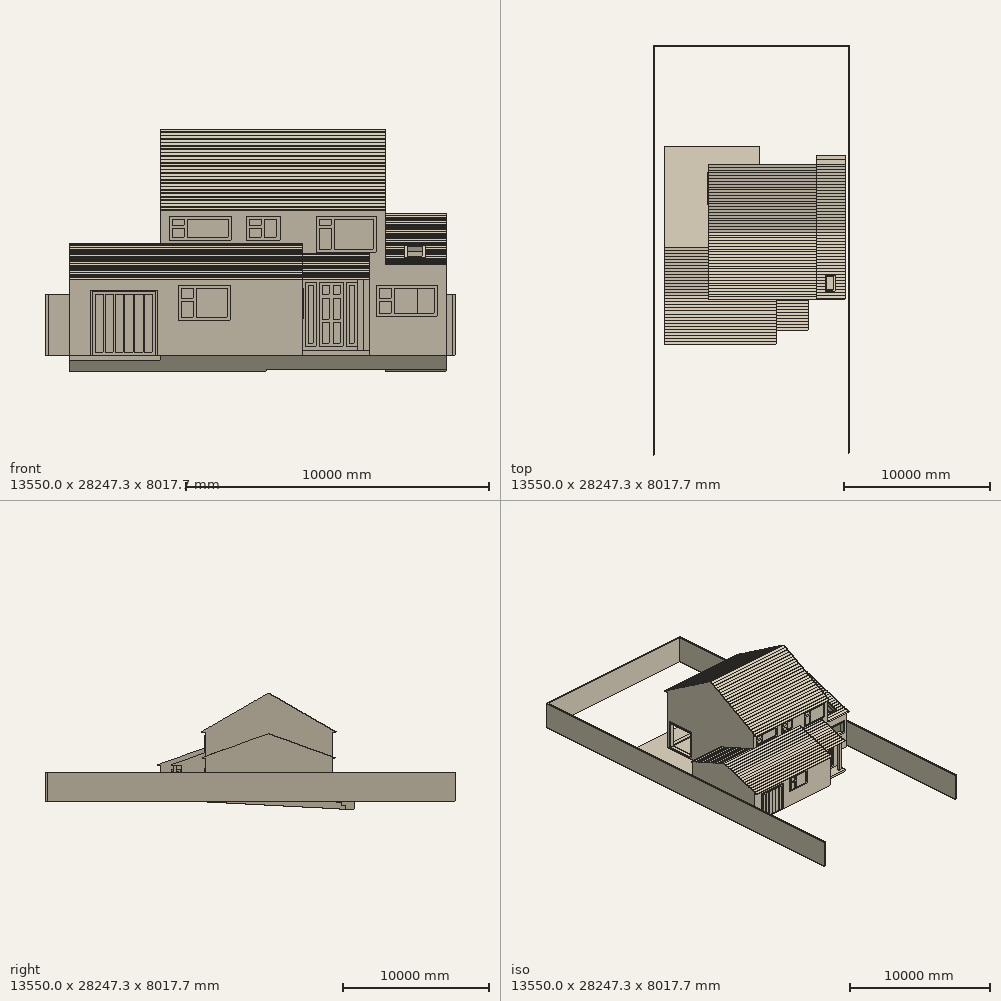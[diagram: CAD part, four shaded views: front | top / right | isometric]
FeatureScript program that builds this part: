
annotation { "Feature Type Name" : "Feature", "Feature Type Description" : "" }
export const myFeature = defineFeature(function(context is Context, id is Id, definition is map)
    precondition{}
    {
        {
            var Q0;
            Q0=qCreatedBy(makeId("Top.planeOp"),FACE);
            var sketch = newSketch(context, id + "F0", { "sketchPlane" : qUnion([Q0])});
            skLineSegment(sketch, "E0", {"start": v(-7450, 3230) * mm, "end": v(-10450, 3230) * mm});
            skLineSegment(sketch, "E1", {"start": v(-10450, 3230) * mm, "end": v(-10450, -3070) * mm});
            skLineSegment(sketch, "E2", {"start": v(-10450, -3070) * mm, "end": v(-2750, -3070) * mm});
            skLineSegment(sketch, "E3", {"start": v(-2750, -3070) * mm, "end": v(-2750, -1320) * mm});
            skLineSegment(sketch, "E4", {"start": v(-2750, 0) * mm, "end": v(0, 0) * mm});
            skLineSegment(sketch, "E5", {"start": v(0, 0) * mm, "end": v(0, 3000) * mm});
            skLineSegment(sketch, "E6", {"start": v(0, 8780) * mm, "end": v(-7450, 8780) * mm});
            skLineSegment(sketch, "E7", {"start": v(-7450, 8780) * mm, "end": v(-7450, 3230) * mm});
            skLineSegment(sketch, "E8", {"start": v(-7450, 2980) * mm, "end": v(-10200, 2980) * mm});
            skLineSegment(sketch, "E9", {"start": v(-10200, 2980) * mm, "end": v(-10200, -2820) * mm});
            skLineSegment(sketch, "E10", {"start": v(-10200, -2820) * mm, "end": v(-7450, -2820) * mm});
            skLineSegment(sketch, "E11", {"start": v(-7450, -2820) * mm, "end": v(-7450, 1280) * mm});
            skLineSegment(sketch, "E12", {"start": v(-7200, 2480) * mm, "end": v(-4870, 2480) * mm});
            skLineSegment(sketch, "E13", {"start": v(-4870, 2480) * mm, "end": v(-4870, -270) * mm});
            skLineSegment(sketch, "E14", {"start": v(-4870, -2820) * mm, "end": v(-7200, -2820) * mm});
            skLineSegment(sketch, "E15", {"start": v(-7200, -2820) * mm, "end": v(-7200, 1280) * mm});
            skLineSegment(sketch, "E16", {"start": v(-3000, -2820) * mm, "end": v(-3000, -1620) * mm});
            skLineSegment(sketch, "E17", {"start": v(-3000, -1620) * mm, "end": v(-3920, -1620) * mm});
            skLineSegment(sketch, "E18", {"start": v(-7200, 2580) * mm, "end": v(-4720, 2580) * mm});
            skLineSegment(sketch, "E19", {"start": v(-3800, 2580) * mm, "end": v(-3800, 6100) * mm});
            skLineSegment(sketch, "E20", {"start": v(-3800, 8530) * mm, "end": v(-7200, 8530) * mm});
            skLineSegment(sketch, "E21", {"start": v(-7200, 8530) * mm, "end": v(-7200, 2580) * mm});
            skLineSegment(sketch, "E22", {"start": v(-250, 8530) * mm, "end": v(-3700, 8530) * mm});
            skLineSegment(sketch, "E23", {"start": v(-3700, 6100) * mm, "end": v(-3700, 4600) * mm});
            skLineSegment(sketch, "E24", {"start": v(-3700, 4600) * mm, "end": v(-3650, 4600) * mm});
            skLineSegment(sketch, "E25", {"start": v(-250, 4600) * mm, "end": v(-250, 8530) * mm});
            skLineSegment(sketch, "E26", {"start": v(-2750, 3043.27) * mm, "end": v(-2750, 4500) * mm});
            skLineSegment(sketch, "E27", {"start": v(-2750, 4500) * mm, "end": v(-2800, 4500) * mm});
            skLineSegment(sketch, "E28", {"start": v(-3700, 4500) * mm, "end": v(-3700, 3043.27) * mm});
            skLineSegment(sketch, "E29", {"start": v(-250, 250) * mm, "end": v(-2650, 250) * mm});
            skLineSegment(sketch, "E30", {"start": v(-2650, 250) * mm, "end": v(-2650, 900) * mm});
            skLineSegment(sketch, "E31", {"start": v(-2650, 4500) * mm, "end": v(-1650, 4500) * mm});
            skLineSegment(sketch, "E32", {"start": v(-250, 4500) * mm, "end": v(-250, 3800) * mm});
            skLineSegment(sketch, "E33", {"start": v(-4770, 2480) * mm, "end": v(-4720, 2480) * mm});
            skLineSegment(sketch, "E34", {"start": v(-2750, 2480) * mm, "end": v(-2750, 1650) * mm});
            skLineSegment(sketch, "E35", {"start": v(-2750, 250) * mm, "end": v(-3000, 250) * mm});
            skLineSegment(sketch, "E36", {"start": v(-3000, -1520) * mm, "end": v(-3920, -1520) * mm});
            skLineSegment(sketch, "E37", {"start": v(-4770, -1520) * mm, "end": v(-4770, -1020) * mm});
            skLineSegment(sketch, "E38", {"start": v(-3000, -620) * mm, "end": v(-2750, -620) * mm, "construction": true});
            skLineSegment(sketch, "E39", {"start": v(-3000, -1320) * mm, "end": v(-2750, -1320) * mm, "construction": true});
            skLineSegment(sketch, "E40.trimOffspring", {"start": v(-2750, -620) * mm, "end": v(-2750, 0) * mm});
            skLineSegment(sketch, "E41.trimOffspring", {"start": v(-3000, -1320) * mm, "end": v(-3000, -1520) * mm});
            skLineSegment(sketch, "E42", {"start": v(-4720, 2580) * mm, "end": v(-4720, 2480) * mm});
            skLineSegment(sketch, "E43", {"start": v(-3970, 2580) * mm, "end": v(-3970, 2480) * mm});
            skLineSegment(sketch, "E44.trimOffspring", {"start": v(-3970, 2580) * mm, "end": v(-3800, 2580) * mm});
            skLineSegment(sketch, "E45.trimOffspring", {"start": v(-3970, 2480) * mm, "end": v(-3700, 2480) * mm});
            skLineSegment(sketch, "E46", {"start": v(-4770, -1620) * mm, "end": v(-4770, -2820) * mm});
            skLineSegment(sketch, "E47", {"start": v(-3000, -2820) * mm, "end": v(-4770, -2820) * mm});
            skLineSegment(sketch, "E48", {"start": v(-4670, -1520) * mm, "end": v(-4670, -1620) * mm});
            skLineSegment(sketch, "E49", {"start": v(-3920, -1620) * mm, "end": v(-3920, -1520) * mm});
            skLineSegment(sketch, "E50.trimOffspring", {"start": v(-4670, -1620) * mm, "end": v(-4770, -1620) * mm});
            skLineSegment(sketch, "E51.trimOffspring", {"start": v(-4670, -1520) * mm, "end": v(-4770, -1520) * mm});
            skLineSegment(sketch, "E52", {"start": v(-4870, -1020) * mm, "end": v(-4770, -1020) * mm});
            skLineSegment(sketch, "E53", {"start": v(-4870, -270) * mm, "end": v(-4770, -270) * mm});
            skLineSegment(sketch, "E54.trimOffspring", {"start": v(-4870, -1020) * mm, "end": v(-4870, -2820) * mm});
            skLineSegment(sketch, "E55.trimOffspring", {"start": v(-4770, -270) * mm, "end": v(-4770, 2480) * mm});
            skLineSegment(sketch, "E56", {"start": v(-3800, 8530) * mm, "end": v(-3700, 8530) * mm});
            skLineSegment(sketch, "E57", {"start": v(-3800, 6100) * mm, "end": v(-3700, 6100) * mm});
            skLineSegment(sketch, "E58", {"start": v(-3650, 4600) * mm, "end": v(-3650, 4500) * mm});
            skLineSegment(sketch, "E59", {"start": v(-2800, 4600) * mm, "end": v(-2800, 4500) * mm});
            skLineSegment(sketch, "E60.trimOffspring", {"start": v(-2800, 4600) * mm, "end": v(-1650, 4600) * mm});
            skLineSegment(sketch, "E61.trimOffspring", {"start": v(-3650, 4500) * mm, "end": v(-3700, 4500) * mm});
            skLineSegment(sketch, "E62", {"start": v(-1650, 4600) * mm, "end": v(-1650, 4500) * mm});
            skLineSegment(sketch, "E63", {"start": v(-950, 4600) * mm, "end": v(-950, 4500) * mm});
            skLineSegment(sketch, "E64.trimOffspring", {"start": v(-950, 4600) * mm, "end": v(-250, 4600) * mm});
            skLineSegment(sketch, "E65.trimOffspring", {"start": v(-950, 4500) * mm, "end": v(-250, 4500) * mm});
            skLineSegment(sketch, "E66", {"start": v(-3000, 250) * mm, "end": v(-3000, -620) * mm});
            skLineSegment(sketch, "E67", {"start": v(-2750, 900) * mm, "end": v(-2650, 900) * mm});
            skLineSegment(sketch, "E68", {"start": v(-2750, 1650) * mm, "end": v(-2650, 1650) * mm});
            skLineSegment(sketch, "E69.trimOffspring", {"start": v(-2750, 900) * mm, "end": v(-2750, 250) * mm});
            skLineSegment(sketch, "E70.trimOffspring", {"start": v(-2650, 1650) * mm, "end": v(-2650, 4500) * mm});
            skLineSegment(sketch, "E71", {"start": v(-7450, 2080) * mm, "end": v(-7200, 2080) * mm});
            skLineSegment(sketch, "E72", {"start": v(-7450, 1280) * mm, "end": v(-7200, 1280) * mm});
            skLineSegment(sketch, "E73.trimOffspring", {"start": v(-7200, 2080) * mm, "end": v(-7200, 2480) * mm});
            skLineSegment(sketch, "E74.trimOffspring", {"start": v(-7450, 2080) * mm, "end": v(-7450, 2980) * mm});
            skLineSegment(sketch, "E75", {"start": v(-250, 3800) * mm, "end": v(0, 3800) * mm});
            skLineSegment(sketch, "E76", {"start": v(-250, 3000) * mm, "end": v(0, 3000) * mm});
            skLineSegment(sketch, "E77.trimOffspring", {"start": v(0, 3800) * mm, "end": v(0, 8780) * mm});
            skLineSegment(sketch, "E78.trimOffspring", {"start": v(-250, 3000) * mm, "end": v(-250, 250) * mm});
            skLineSegment(sketch, "E79", {"start": v(-3000, -620) * mm, "end": v(-3000, -1320) * mm});
            skLineSegment(sketch, "E80", {"start": v(-2750, -620) * mm, "end": v(-2750, -1320) * mm});
            skLineSegment(sketch, "E81", {"start": v(-3700, 3043.27) * mm, "end": v(-3700, 2480) * mm});
            skLineSegment(sketch, "E82", {"start": v(-2750, 2480) * mm, "end": v(-2750, 3043.27) * mm});
            skSolve(sketch);
        }
        {
            var Q0;
            Q0=qSketchRegion(id+"F0",true);
            extrude(context, id + "F1", {"entities" : qUnion([Q0]), "offsetDistance" : 25 * mm, "depth" : 2500 * mm});
        }
        {
            var Q0;
            Q0=makeQuery(id+"F1.opExtrude","CAP_FACE",FACE,{"disambiguationData":[OSD([sQuery(id+"F0.wireOp",EDGE,"E0"),sQuery(id+"F0.wireOp",EDGE,"E1"),sQuery(id+"F0.wireOp",EDGE,"E2"),sQuery(id+"F0.wireOp",EDGE,"E3"),sQuery(id+"F0.wireOp",EDGE,"E6"),sQuery(id+"F0.wireOp",EDGE,"E7"),sQuery(id+"F0.wireOp",EDGE,"E8"),sQuery(id+"F0.wireOp",EDGE,"E9"),sQuery(id+"F0.wireOp",EDGE,"E10"),sQuery(id+"F0.wireOp",EDGE,"E11"),sQuery(id+"F0.wireOp",EDGE,"E12"),sQuery(id+"F0.wireOp",EDGE,"E13"),sQuery(id+"F0.wireOp",EDGE,"E14"),sQuery(id+"F0.wireOp",EDGE,"E15"),sQuery(id+"F0.wireOp",EDGE,"E16"),sQuery(id+"F0.wireOp",EDGE,"E17"),sQuery(id+"F0.wireOp",EDGE,"E18"),sQuery(id+"F0.wireOp",EDGE,"E20"),sQuery(id+"F0.wireOp",EDGE,"E21"),sQuery(id+"F0.wireOp",EDGE,"E22"),sQuery(id+"F0.wireOp",EDGE,"E25"),sQuery(id+"F0.wireOp",EDGE,"E32"),sQuery(id+"F0.wireOp",EDGE,"E33"),sQuery(id+"F0.wireOp",EDGE,"E36"),sQuery(id+"F0.wireOp",EDGE,"E37"),sQuery(id+"F0.wireOp",EDGE,"E39"),sQuery(id+"F0.wireOp",EDGE,"E41.trimOffspring"),sQuery(id+"F0.wireOp",EDGE,"E42"),sQuery(id+"F0.wireOp",EDGE,"E46"),sQuery(id+"F0.wireOp",EDGE,"E47"),sQuery(id+"F0.wireOp",EDGE,"E48"),sQuery(id+"F0.wireOp",EDGE,"E49"),sQuery(id+"F0.wireOp",EDGE,"E50.trimOffspring"),sQuery(id+"F0.wireOp",EDGE,"E51.trimOffspring"),sQuery(id+"F0.wireOp",EDGE,"E52"),sQuery(id+"F0.wireOp",EDGE,"E53"),sQuery(id+"F0.wireOp",EDGE,"E54.trimOffspring"),sQuery(id+"F0.wireOp",EDGE,"E55.trimOffspring"),sQuery(id+"F0.wireOp",EDGE,"E56"),sQuery(id+"F0.wireOp",EDGE,"E63"),sQuery(id+"F0.wireOp",EDGE,"E64.trimOffspring"),sQuery(id+"F0.wireOp",EDGE,"E65.trimOffspring"),sQuery(id+"F0.wireOp",EDGE,"E71"),sQuery(id+"F0.wireOp",EDGE,"E72"),sQuery(id+"F0.wireOp",EDGE,"E73.trimOffspring"),sQuery(id+"F0.wireOp",EDGE,"E74.trimOffspring"),sQuery(id+"F0.wireOp",EDGE,"E75"),sQuery(id+"F0.wireOp",EDGE,"E77.trimOffspring")])],"isStart":false});
            var sketch = newSketch(context, id + "F2", { "sketchPlane" : qUnion([Q0])});
            skLineSegment(sketch, "E83.bottom", {"start": v(-7450, 8780) * mm, "end": v(0, 8780) * mm});
            skLineSegment(sketch, "E83.top", {"start": v(-7450, 0) * mm, "end": v(0, 0) * mm});
            skLineSegment(sketch, "E83.left", {"start": v(-7450, 8780) * mm, "end": v(-7450, 0) * mm});
            skLineSegment(sketch, "E83.right", {"start": v(0, 8780) * mm, "end": v(0, 0) * mm});
            skLineSegment(sketch, "E84.bottom", {"start": v(-7200, 8530) * mm, "end": v(-250, 8530) * mm});
            skLineSegment(sketch, "E84.top", {"start": v(-7200, 250) * mm, "end": v(-250, 250) * mm});
            skLineSegment(sketch, "E84.left", {"start": v(-7200, 8530) * mm, "end": v(-7200, 250) * mm});
            skLineSegment(sketch, "E84.right", {"start": v(-250, 8530) * mm, "end": v(-250, 250) * mm});
            skSolve(sketch);
        }
        {
            var Q0;
            Q0 = qSketchRegion(id + "F2", true);
            extrude(context, id + "F3", {"entities" : qUnion([Q0]), "operationType" : NewBodyOperationType.ADD, "depth" : 2300 * mm, "offsetDistance" : 25 * mm});
        }
        {
            var Q0;
            Q0=makeQuery(id+"F1.opExtrude","SWEPT_FACE",FACE,{"disambiguationData":[OSD([sQuery(id+"F0.wireOp",EDGE,"E1")])]});
            var sketch = newSketch(context, id + "F4", { "sketchPlane" : qUnion([Q0])});
            skLineSegment(sketch, "E85", {"start": v(3320, 2500) * mm, "end": v(0, 3708.38) * mm, "construction": true});
            skLineSegment(sketch, "E86", {"start": v(0, 3708.38) * mm, "end": v(-3320, 2500) * mm, "construction": true});
            skLineSegment(sketch, "E87", {"start": v(-3320, 2500) * mm, "end": v(3320, 2500) * mm});
            skLineSegment(sketch, "E88", {"start": v(0, 3708.38) * mm, "end": v(207.5, 3660.48) * mm});
            skLineSegment(sketch, "E89", {"start": v(207.5, 3660.48) * mm, "end": v(207.5, 3632.86) * mm});
            skLineSegment(sketch, "E90", {"start": v(207.5, 3632.86) * mm, "end": v(415, 3584.95) * mm});
            skLineSegment(sketch, "E91", {"start": v(415, 3584.95) * mm, "end": v(415, 3557.33) * mm});
            skLineSegment(sketch, "E92", {"start": v(415, 3557.33) * mm, "end": v(622.5, 3509.43) * mm});
            skLineSegment(sketch, "E93", {"start": v(622.5, 3509.43) * mm, "end": v(622.5, 3481.8) * mm});
            skLineSegment(sketch, "E94", {"start": v(622.5, 3481.8) * mm, "end": v(830, 3433.9) * mm});
            skLineSegment(sketch, "E95", {"start": v(830, 3433.9) * mm, "end": v(830, 3406.29) * mm});
            skLineSegment(sketch, "E96", {"start": v(830, 3406.29) * mm, "end": v(1037.5, 3358.38) * mm});
            skLineSegment(sketch, "E97", {"start": v(1037.5, 3358.38) * mm, "end": v(1037.5, 3330.76) * mm});
            skLineSegment(sketch, "E98", {"start": v(1037.5, 3330.76) * mm, "end": v(1245, 3282.86) * mm});
            skLineSegment(sketch, "E99", {"start": v(1245, 3282.86) * mm, "end": v(1245, 3255.24) * mm});
            skLineSegment(sketch, "E100", {"start": v(1245, 3255.24) * mm, "end": v(1452.5, 3207.33) * mm});
            skLineSegment(sketch, "E101", {"start": v(1452.5, 3207.33) * mm, "end": v(1452.5, 3179.71) * mm});
            skLineSegment(sketch, "E102", {"start": v(1452.5, 3179.71) * mm, "end": v(1660, 3131.8) * mm});
            skLineSegment(sketch, "E103", {"start": v(1660, 3131.8) * mm, "end": v(1660, 3104.2) * mm});
            skLineSegment(sketch, "E104", {"start": v(1660, 3104.2) * mm, "end": v(1867.5, 3056.29) * mm});
            skLineSegment(sketch, "E105", {"start": v(1867.5, 3056.29) * mm, "end": v(1867.5, 3028.67) * mm});
            skLineSegment(sketch, "E106", {"start": v(1867.5, 3028.67) * mm, "end": v(2075, 2980.76) * mm});
            skLineSegment(sketch, "E107", {"start": v(2075, 2980.76) * mm, "end": v(2075, 2953.14) * mm});
            skLineSegment(sketch, "E108", {"start": v(2075, 2953.14) * mm, "end": v(2282.5, 2905.24) * mm});
            skLineSegment(sketch, "E109", {"start": v(2282.5, 2905.24) * mm, "end": v(2282.5, 2877.62) * mm});
            skLineSegment(sketch, "E110", {"start": v(2282.5, 2877.62) * mm, "end": v(2490, 2829.71) * mm});
            skLineSegment(sketch, "E111", {"start": v(2490, 2829.71) * mm, "end": v(2490, 2802.1) * mm});
            skLineSegment(sketch, "E112", {"start": v(2490, 2802.1) * mm, "end": v(2697.5, 2754.2) * mm});
            skLineSegment(sketch, "E113", {"start": v(2697.5, 2754.2) * mm, "end": v(2697.5, 2726.57) * mm});
            skLineSegment(sketch, "E114", {"start": v(2697.5, 2726.57) * mm, "end": v(2905, 2678.67) * mm});
            skLineSegment(sketch, "E115", {"start": v(2905, 2678.67) * mm, "end": v(2905, 2651.05) * mm});
            skLineSegment(sketch, "E116", {"start": v(2905, 2651.05) * mm, "end": v(3112.5, 2603.14) * mm});
            skLineSegment(sketch, "E117", {"start": v(3112.5, 2603.14) * mm, "end": v(3112.5, 2575.52) * mm});
            skLineSegment(sketch, "E118", {"start": v(3112.5, 2575.52) * mm, "end": v(3320, 2527.62) * mm});
            skLineSegment(sketch, "E119", {"start": v(3320, 2527.62) * mm, "end": v(3320, 2500) * mm});
            skLineSegment(sketch, "E120", {"start": v(0, 3708.38) * mm, "end": v(0, 3821.25) * mm, "construction": true});
            skLineSegment(sketch, "E121.MirrorCS", {"start": v(-207.5, 3660.48) * mm, "end": v(-207.5, 3632.86) * mm});
            skLineSegment(sketch, "E122.MirrorCS", {"start": v(-2905, 2678.67) * mm, "end": v(-2905, 2651.05) * mm});
            skLineSegment(sketch, "E123.MirrorCS", {"start": v(-3320, 2527.62) * mm, "end": v(-3320, 2500) * mm});
            skLineSegment(sketch, "E124.MirrorCS", {"start": v(-3112.5, 2603.14) * mm, "end": v(-3112.5, 2575.52) * mm});
            skLineSegment(sketch, "E125.MirrorCS", {"start": v(0, 3708.38) * mm, "end": v(-207.5, 3660.48) * mm});
            skLineSegment(sketch, "E126.MirrorCS", {"start": v(-1452.5, 3207.33) * mm, "end": v(-1452.5, 3179.71) * mm});
            skLineSegment(sketch, "E127.MirrorCS", {"start": v(-2697.5, 2754.2) * mm, "end": v(-2697.5, 2726.57) * mm});
            skLineSegment(sketch, "E128.MirrorCS", {"start": v(-2075, 2953.14) * mm, "end": v(-2282.5, 2905.24) * mm});
            skLineSegment(sketch, "E129.MirrorCS", {"start": v(-3112.5, 2575.52) * mm, "end": v(-3320, 2527.62) * mm});
            skLineSegment(sketch, "E130.MirrorCS", {"start": v(-1245, 3255.24) * mm, "end": v(-1452.5, 3207.33) * mm});
            skLineSegment(sketch, "E131.MirrorCS", {"start": v(-1037.5, 3358.38) * mm, "end": v(-1037.5, 3330.76) * mm});
            skLineSegment(sketch, "E132.MirrorCS", {"start": v(-830, 3406.29) * mm, "end": v(-1037.5, 3358.38) * mm});
            skLineSegment(sketch, "E133.MirrorCS", {"start": v(-2282.5, 2905.24) * mm, "end": v(-2282.5, 2877.62) * mm});
            skLineSegment(sketch, "E134.MirrorCS", {"start": v(-1037.5, 3330.76) * mm, "end": v(-1245, 3282.86) * mm});
            skLineSegment(sketch, "E135.MirrorCS", {"start": v(-2490, 2802.1) * mm, "end": v(-2697.5, 2754.2) * mm});
            skLineSegment(sketch, "E136.MirrorCS", {"start": v(-2490, 2829.71) * mm, "end": v(-2490, 2802.1) * mm});
            skLineSegment(sketch, "E137.MirrorCS", {"start": v(-830, 3433.9) * mm, "end": v(-830, 3406.29) * mm});
            skLineSegment(sketch, "E138.MirrorCS", {"start": v(-1660, 3104.2) * mm, "end": v(-1867.5, 3056.29) * mm});
            skLineSegment(sketch, "E139.MirrorCS", {"start": v(-1660, 3131.8) * mm, "end": v(-1660, 3104.2) * mm});
            skLineSegment(sketch, "E140.MirrorCS", {"start": v(-1867.5, 3056.29) * mm, "end": v(-1867.5, 3028.67) * mm});
            skLineSegment(sketch, "E141.MirrorCS", {"start": v(-622.5, 3509.43) * mm, "end": v(-622.5, 3481.8) * mm});
            skLineSegment(sketch, "E142.MirrorCS", {"start": v(-2905, 2651.05) * mm, "end": v(-3112.5, 2603.14) * mm});
            skLineSegment(sketch, "E143.MirrorCS", {"start": v(-2282.5, 2877.62) * mm, "end": v(-2490, 2829.71) * mm});
            skLineSegment(sketch, "E144.MirrorCS", {"start": v(-415, 3557.33) * mm, "end": v(-622.5, 3509.43) * mm});
            skLineSegment(sketch, "E145.MirrorCS", {"start": v(-415, 3584.95) * mm, "end": v(-415, 3557.33) * mm});
            skLineSegment(sketch, "E146.MirrorCS", {"start": v(-622.5, 3481.8) * mm, "end": v(-830, 3433.9) * mm});
            skLineSegment(sketch, "E147.MirrorCS", {"start": v(-1867.5, 3028.67) * mm, "end": v(-2075, 2980.76) * mm});
            skLineSegment(sketch, "E148.MirrorCS", {"start": v(-207.5, 3632.86) * mm, "end": v(-415, 3584.95) * mm});
            skLineSegment(sketch, "E149.MirrorCS", {"start": v(-1245, 3282.86) * mm, "end": v(-1245, 3255.24) * mm});
            skLineSegment(sketch, "E150.MirrorCS", {"start": v(-2697.5, 2726.57) * mm, "end": v(-2905, 2678.67) * mm});
            skLineSegment(sketch, "E151.MirrorCS", {"start": v(-1452.5, 3179.71) * mm, "end": v(-1660, 3131.8) * mm});
            skLineSegment(sketch, "E152.MirrorCS", {"start": v(-2075, 2980.76) * mm, "end": v(-2075, 2953.14) * mm});
            skSolve(sketch);
        }
        {
            var Q0;
            Q0 = qSketchRegion(id + "F4", true);
            var Q1;
            Q1=makeQuery(id+"F3.boolean.opBoolean","MERGE",FACE,{"derivedFrom":[makeQuery(id+"F1.opExtrude","SWEPT_FACE",FACE,{"disambiguationData":[OSD([sQuery(id+"F0.wireOp",EDGE,"E7")])]}),makeQuery(id+"F1.opExtrude","SWEPT_FACE",FACE,{"disambiguationData":[OSD([sQuery(id+"F0.wireOp",EDGE,"E11")])]}),makeQuery(id+"F1.opExtrude","SWEPT_FACE",FACE,{"disambiguationData":[OSD([sQuery(id+"F0.wireOp",EDGE,"E74.trimOffspring")])]}),makeQuery(id+"F3.opExtrude","SWEPT_FACE",FACE,{"disambiguationData":[OSD([sQuery(id+"F2.wireOp",EDGE,"E83.left")])]})]});
            extrude(context, id + "F5", {"entities" : qUnion([Q0]), "operationType" : NewBodyOperationType.ADD, "oppositeDirection" : true, "depth" : 3250 * mm, "endBoundEntityFace" : qUnion([Q1]), "offsetDistance" : 25 * mm});
        }
        {
            var Q0;
            Q0=makeQuery(id+"F5.boolean.opBoolean","MERGE",FACE,{"derivedFrom":[makeQuery(id+"F3.boolean.opBoolean","MERGE",FACE,{"derivedFrom":[makeQuery(id+"F1.opExtrude","SWEPT_FACE",FACE,{"disambiguationData":[OSD([sQuery(id+"F0.wireOp",EDGE,"E15")])]}),makeQuery(id+"F1.opExtrude","SWEPT_FACE",FACE,{"disambiguationData":[OSD([sQuery(id+"F0.wireOp",EDGE,"E21")])]}),makeQuery(id+"F1.opExtrude","SWEPT_FACE",FACE,{"disambiguationData":[OSD([sQuery(id+"F0.wireOp",EDGE,"E73.trimOffspring")])]}),makeQuery(id+"F3.opExtrude","SWEPT_FACE",FACE,{"disambiguationData":[OSD([sQuery(id+"F2.wireOp",EDGE,"E84.left")])]})]}),makeQuery(id+"F5.opExtrude","CAP_FACE",FACE,{"disambiguationData":[OSD([sQuery(id+"F4.wireOp",EDGE,"E85"),sQuery(id+"F4.wireOp",EDGE,"E86"),sQuery(id+"F4.wireOp",EDGE,"E87")])],"isStart":false})]});
            var sketch = newSketch(context, id + "F6", { "sketchPlane" : qUnion([Q0])});
            skLineSegment(sketch, "E153", {"start": v(0, 2500) * mm, "end": v(0, 3708.38) * mm});
            skLineSegment(sketch, "E154", {"start": v(0, 3708.38) * mm, "end": v(-3320, 2500) * mm, "construction": true});
            skLineSegment(sketch, "E155", {"start": v(-3320, 2500) * mm, "end": v(-3070, 2500) * mm});
            skLineSegment(sketch, "E156", {"start": v(-3070, 2500) * mm, "end": v(-3070, 2300) * mm});
            skLineSegment(sketch, "E157", {"start": v(-3070, 2300) * mm, "end": v(0, 2300) * mm});
            skLineSegment(sketch, "E158", {"start": v(0, 2300) * mm, "end": v(0, 2500) * mm});
            skLineSegment(sketch, "E159.0", {"start": v(0, 3708.38) * mm, "end": v(-207.5, 3660.48) * mm});
            skLineSegment(sketch, "E160.0", {"start": v(-207.5, 3660.48) * mm, "end": v(-207.5, 3632.86) * mm});
            skLineSegment(sketch, "E160.1", {"start": v(-207.5, 3632.86) * mm, "end": v(-415, 3584.95) * mm});
            skLineSegment(sketch, "E160.2", {"start": v(-415, 3584.95) * mm, "end": v(-415, 3557.33) * mm});
            skLineSegment(sketch, "E160.3", {"start": v(-415, 3557.33) * mm, "end": v(-622.5, 3509.43) * mm});
            skLineSegment(sketch, "E160.4", {"start": v(-622.5, 3509.43) * mm, "end": v(-622.5, 3481.8) * mm});
            skLineSegment(sketch, "E161.0", {"start": v(-622.5, 3481.8) * mm, "end": v(-830, 3433.9) * mm});
            skLineSegment(sketch, "E161.1", {"start": v(-830, 3433.9) * mm, "end": v(-830, 3406.29) * mm});
            skLineSegment(sketch, "E161.2", {"start": v(-830, 3406.29) * mm, "end": v(-1037.5, 3358.38) * mm});
            skLineSegment(sketch, "E161.3", {"start": v(-1037.5, 3358.38) * mm, "end": v(-1037.5, 3330.76) * mm});
            skLineSegment(sketch, "E162.0", {"start": v(-1037.5, 3330.76) * mm, "end": v(-1245, 3282.86) * mm});
            skLineSegment(sketch, "E162.1", {"start": v(-1245, 3282.86) * mm, "end": v(-1245, 3255.24) * mm});
            skLineSegment(sketch, "E162.2", {"start": v(-1245, 3255.24) * mm, "end": v(-1452.5, 3207.33) * mm});
            skLineSegment(sketch, "E162.3", {"start": v(-1452.5, 3207.33) * mm, "end": v(-1452.5, 3179.71) * mm});
            skLineSegment(sketch, "E163.0", {"start": v(-1452.5, 3179.71) * mm, "end": v(-1660, 3131.8) * mm});
            skLineSegment(sketch, "E163.1", {"start": v(-1660, 3131.8) * mm, "end": v(-1660, 3104.2) * mm});
            skLineSegment(sketch, "E163.2", {"start": v(-1660, 3104.2) * mm, "end": v(-1867.5, 3056.29) * mm});
            skLineSegment(sketch, "E163.3", {"start": v(-1867.5, 3056.29) * mm, "end": v(-1867.5, 3028.67) * mm});
            skLineSegment(sketch, "E164.0", {"start": v(-1867.5, 3028.67) * mm, "end": v(-2075, 2980.76) * mm});
            skLineSegment(sketch, "E164.1", {"start": v(-2075, 2980.76) * mm, "end": v(-2075, 2953.14) * mm});
            skLineSegment(sketch, "E164.2", {"start": v(-2075, 2953.14) * mm, "end": v(-2282.5, 2905.24) * mm});
            skLineSegment(sketch, "E164.3", {"start": v(-2282.5, 2905.24) * mm, "end": v(-2282.5, 2877.62) * mm});
            skLineSegment(sketch, "E164.4", {"start": v(-2282.5, 2877.62) * mm, "end": v(-2490, 2829.71) * mm});
            skLineSegment(sketch, "E164.5", {"start": v(-2490, 2829.71) * mm, "end": v(-2490, 2802.1) * mm});
            skLineSegment(sketch, "E164.6", {"start": v(-2490, 2802.1) * mm, "end": v(-2697.5, 2754.2) * mm});
            skLineSegment(sketch, "E165.0", {"start": v(-2697.5, 2754.2) * mm, "end": v(-2697.5, 2726.57) * mm});
            skLineSegment(sketch, "E165.1", {"start": v(-2697.5, 2726.57) * mm, "end": v(-2905, 2678.67) * mm});
            skLineSegment(sketch, "E165.2", {"start": v(-2905, 2678.67) * mm, "end": v(-2905, 2651.05) * mm});
            skLineSegment(sketch, "E165.3", {"start": v(-2905, 2651.05) * mm, "end": v(-3112.5, 2603.14) * mm});
            skLineSegment(sketch, "E165.4", {"start": v(-3112.5, 2603.14) * mm, "end": v(-3112.5, 2575.52) * mm});
            skLineSegment(sketch, "E165.5", {"start": v(-3112.5, 2575.52) * mm, "end": v(-3320, 2527.62) * mm});
            skLineSegment(sketch, "E165.6", {"start": v(-3320, 2527.62) * mm, "end": v(-3320, 2500) * mm});
            skSolve(sketch);
        }
        {
            var Q0;
            Q0 = qSketchRegion(id + "F6", true);
            var Q1;
            Q1=makeQuery(id+"F1.opExtrude","SWEPT_FACE",FACE,{"disambiguationData":[OSD([sQuery(id+"F0.wireOp",EDGE,"E40.trimOffspring")])]});
            extrude(context, id + "F7", {"entities" : qUnion([Q0]), "operationType" : NewBodyOperationType.ADD, "endBound" : BoundingType.UP_TO_SURFACE, "depth" : 25 * mm, "endBoundEntityFace" : qUnion([Q1]), "offsetDistance" : 25 * mm, "hasSecondDirection" : true, "secondDirectionOppositeDirection" : true, "secondDirectionDepth" : 250 * mm});
        }
        {
            var Q0;
            Q0=makeQuery(id+"F3.boolean.opBoolean","MERGE",FACE,{"derivedFrom":[makeQuery(id+"F1.opExtrude","SWEPT_FACE",FACE,{"disambiguationData":[OSD([sQuery(id+"F0.wireOp",EDGE,"E5")])]}),makeQuery(id+"F1.opExtrude","SWEPT_FACE",FACE,{"disambiguationData":[OSD([sQuery(id+"F0.wireOp",EDGE,"E77.trimOffspring")])]}),makeQuery(id+"F3.opExtrude","SWEPT_FACE",FACE,{"disambiguationData":[OSD([sQuery(id+"F2.wireOp",EDGE,"E83.right")])]})]});
            var sketch = newSketch(context, id + "F8", { "sketchPlane" : qUnion([Q0])});
            skLineSegment(sketch, "E166", {"start": v(4390, 7478.9) * mm, "end": v(-250, 4800) * mm, "construction": true});
            skLineSegment(sketch, "E167", {"start": v(-250, 4800) * mm, "end": v(9030, 4800) * mm});
            skLineSegment(sketch, "E168", {"start": v(9030, 4800) * mm, "end": v(4390, 7478.9) * mm, "construction": true});
            skLineSegment(sketch, "E169", {"start": v(4390, 7478.9) * mm, "end": v(4390, 6580.18) * mm, "construction": true});
            skLineSegment(sketch, "E170", {"start": v(4390, 7478.9) * mm, "end": v(4195.45, 7392.29) * mm});
            skLineSegment(sketch, "E171", {"start": v(4195.45, 7392.29) * mm, "end": v(4195.45, 7366.58) * mm});
            skLineSegment(sketch, "E172", {"start": v(4195.45, 7366.58) * mm, "end": v(4000.9, 7279.97) * mm});
            skLineSegment(sketch, "E173", {"start": v(4000.9, 7279.97) * mm, "end": v(4000.9, 7254.26) * mm});
            skLineSegment(sketch, "E174", {"start": v(4000.9, 7254.26) * mm, "end": v(3806.36, 7167.64) * mm});
            skLineSegment(sketch, "E175", {"start": v(3806.36, 7167.64) * mm, "end": v(3806.36, 7141.94) * mm});
            skLineSegment(sketch, "E176", {"start": v(3806.36, 7141.94) * mm, "end": v(3611.81, 7055.32) * mm});
            skLineSegment(sketch, "E177", {"start": v(3611.81, 7055.32) * mm, "end": v(3611.81, 7029.62) * mm});
            skLineSegment(sketch, "E178", {"start": v(3611.81, 7029.62) * mm, "end": v(3417.27, 6943) * mm});
            skLineSegment(sketch, "E179", {"start": v(3417.27, 6943) * mm, "end": v(3417.27, 6917.3) * mm});
            skLineSegment(sketch, "E180", {"start": v(3417.27, 6917.3) * mm, "end": v(3222.72, 6830.68) * mm});
            skLineSegment(sketch, "E181", {"start": v(3222.72, 6830.68) * mm, "end": v(3222.72, 6804.97) * mm});
            skLineSegment(sketch, "E182", {"start": v(3222.72, 6804.97) * mm, "end": v(3028.17, 6718.36) * mm});
            skLineSegment(sketch, "E183", {"start": v(3028.17, 6718.36) * mm, "end": v(3028.17, 6692.65) * mm});
            skLineSegment(sketch, "E184", {"start": v(3028.17, 6692.65) * mm, "end": v(2833.62, 6606.04) * mm});
            skLineSegment(sketch, "E185", {"start": v(2833.62, 6606.04) * mm, "end": v(2833.62, 6580.33) * mm});
            skLineSegment(sketch, "E186", {"start": v(2833.62, 6580.33) * mm, "end": v(2639.08, 6493.71) * mm});
            skLineSegment(sketch, "E187", {"start": v(2639.08, 6493.71) * mm, "end": v(2639.08, 6468) * mm});
            skLineSegment(sketch, "E188", {"start": v(2639.08, 6468) * mm, "end": v(2444.53, 6381.4) * mm});
            skLineSegment(sketch, "E189", {"start": v(2444.53, 6381.4) * mm, "end": v(2444.53, 6355.69) * mm});
            skLineSegment(sketch, "E190", {"start": v(2444.53, 6355.69) * mm, "end": v(2249.98, 6269.07) * mm});
            skLineSegment(sketch, "E191", {"start": v(2249.98, 6269.07) * mm, "end": v(2249.98, 6243.37) * mm});
            skLineSegment(sketch, "E192", {"start": v(2249.98, 6243.37) * mm, "end": v(2055.44, 6156.75) * mm});
            skLineSegment(sketch, "E193", {"start": v(2055.44, 6156.75) * mm, "end": v(2055.44, 6131.04) * mm});
            skLineSegment(sketch, "E194", {"start": v(2055.44, 6131.04) * mm, "end": v(1860.9, 6044.43) * mm});
            skLineSegment(sketch, "E195", {"start": v(1860.9, 6044.43) * mm, "end": v(1860.9, 6018.72) * mm});
            skLineSegment(sketch, "E196", {"start": v(1860.9, 6018.72) * mm, "end": v(1666.34, 5932.1) * mm});
            skLineSegment(sketch, "E197", {"start": v(1666.34, 5932.1) * mm, "end": v(1666.34, 5906.4) * mm});
            skLineSegment(sketch, "E198", {"start": v(1666.34, 5906.4) * mm, "end": v(1471.8, 5819.78) * mm});
            skLineSegment(sketch, "E199", {"start": v(1471.8, 5819.78) * mm, "end": v(1471.8, 5794.08) * mm});
            skLineSegment(sketch, "E200", {"start": v(1471.8, 5794.08) * mm, "end": v(1277.25, 5707.46) * mm});
            skLineSegment(sketch, "E201", {"start": v(1277.25, 5707.46) * mm, "end": v(1277.25, 5681.76) * mm});
            skLineSegment(sketch, "E202", {"start": v(1277.25, 5681.76) * mm, "end": v(1082.7, 5595.14) * mm});
            skLineSegment(sketch, "E203", {"start": v(1082.7, 5595.14) * mm, "end": v(1082.7, 5569.44) * mm});
            skLineSegment(sketch, "E204", {"start": v(1082.7, 5569.44) * mm, "end": v(888.16, 5482.82) * mm});
            skLineSegment(sketch, "E205", {"start": v(888.16, 5482.82) * mm, "end": v(888.16, 5457.11) * mm});
            skLineSegment(sketch, "E206", {"start": v(888.16, 5457.11) * mm, "end": v(693.6, 5370.5) * mm});
            skLineSegment(sketch, "E207", {"start": v(693.6, 5370.5) * mm, "end": v(693.6, 5344.8) * mm});
            skLineSegment(sketch, "E208", {"start": v(693.6, 5344.8) * mm, "end": v(499.06, 5258.17) * mm});
            skLineSegment(sketch, "E209", {"start": v(499.06, 5258.17) * mm, "end": v(499.06, 5232.47) * mm});
            skLineSegment(sketch, "E210", {"start": v(499.06, 5232.47) * mm, "end": v(304.51, 5145.85) * mm});
            skLineSegment(sketch, "E211", {"start": v(304.51, 5145.85) * mm, "end": v(304.51, 5120.15) * mm});
            skLineSegment(sketch, "E212", {"start": v(304.51, 5120.15) * mm, "end": v(109.97, 5033.53) * mm});
            skLineSegment(sketch, "E213", {"start": v(109.97, 5033.53) * mm, "end": v(109.97, 5007.83) * mm});
            skLineSegment(sketch, "E214", {"start": v(109.97, 5007.83) * mm, "end": v(-70.02, 4927.7) * mm});
            skLineSegment(sketch, "E215", {"start": v(-70.02, 4927.7) * mm, "end": v(-70.02, 4903.91) * mm});
            skLineSegment(sketch, "E216", {"start": v(-70.02, 4903.91) * mm, "end": v(-250, 4823.78) * mm});
            skLineSegment(sketch, "E217", {"start": v(-250, 4823.78) * mm, "end": v(-250, 4800) * mm});
            skLineSegment(sketch, "E218.MirrorCS", {"start": v(7697.3, 5595.14) * mm, "end": v(7697.3, 5569.44) * mm});
            skLineSegment(sketch, "E219.MirrorCS", {"start": v(6724.56, 6156.75) * mm, "end": v(6724.56, 6131.04) * mm});
            skLineSegment(sketch, "E220.MirrorCS", {"start": v(5751.83, 6718.36) * mm, "end": v(5751.83, 6692.65) * mm});
            skLineSegment(sketch, "E221.MirrorCS", {"start": v(9030, 4823.78) * mm, "end": v(9030, 4800) * mm});
            skLineSegment(sketch, "E222.MirrorCS", {"start": v(5557.28, 6830.68) * mm, "end": v(5557.28, 6804.97) * mm});
            skLineSegment(sketch, "E223.MirrorCS", {"start": v(4973.64, 7167.64) * mm, "end": v(4973.64, 7141.94) * mm});
            skLineSegment(sketch, "E224.MirrorCS", {"start": v(4584.55, 7392.29) * mm, "end": v(4584.55, 7366.58) * mm});
            skLineSegment(sketch, "E225.MirrorCS", {"start": v(8850.02, 4903.91) * mm, "end": v(9030, 4823.78) * mm});
            skLineSegment(sketch, "E226.MirrorCS", {"start": v(8850.02, 4927.7) * mm, "end": v(8850.02, 4903.91) * mm});
            skLineSegment(sketch, "E227.MirrorCS", {"start": v(5946.38, 6606.04) * mm, "end": v(5946.38, 6580.33) * mm});
            skLineSegment(sketch, "E228.MirrorCS", {"start": v(6919.1, 6044.43) * mm, "end": v(6919.1, 6018.72) * mm});
            skLineSegment(sketch, "E229.MirrorCS", {"start": v(7308.2, 5794.08) * mm, "end": v(7502.75, 5707.46) * mm});
            skLineSegment(sketch, "E230.MirrorCS", {"start": v(6140.92, 6468) * mm, "end": v(6335.47, 6381.4) * mm});
            skLineSegment(sketch, "E231.MirrorCS", {"start": v(6919.1, 6018.72) * mm, "end": v(7113.66, 5932.1) * mm});
            skLineSegment(sketch, "E232.MirrorCS", {"start": v(4779.1, 7279.97) * mm, "end": v(4779.1, 7254.26) * mm});
            skLineSegment(sketch, "E233.MirrorCS", {"start": v(7502.75, 5707.46) * mm, "end": v(7502.75, 5681.76) * mm});
            skLineSegment(sketch, "E234.MirrorCS", {"start": v(7113.66, 5906.4) * mm, "end": v(7308.2, 5819.78) * mm});
            skLineSegment(sketch, "E235.MirrorCS", {"start": v(4390, 7478.9) * mm, "end": v(4584.55, 7392.29) * mm});
            skLineSegment(sketch, "E236.MirrorCS", {"start": v(8280.94, 5258.17) * mm, "end": v(8280.94, 5232.47) * mm});
            skLineSegment(sketch, "E237.MirrorCS", {"start": v(5751.83, 6692.65) * mm, "end": v(5946.38, 6606.04) * mm});
            skLineSegment(sketch, "E238.MirrorCS", {"start": v(5362.73, 6943) * mm, "end": v(5362.73, 6917.3) * mm});
            skLineSegment(sketch, "E239.MirrorCS", {"start": v(4779.1, 7254.26) * mm, "end": v(4973.64, 7167.64) * mm});
            skLineSegment(sketch, "E240.MirrorCS", {"start": v(8670.03, 5033.53) * mm, "end": v(8670.03, 5007.83) * mm});
            skLineSegment(sketch, "E241.MirrorCS", {"start": v(5557.28, 6804.97) * mm, "end": v(5751.83, 6718.36) * mm});
            skLineSegment(sketch, "E242.MirrorCS", {"start": v(4584.55, 7366.58) * mm, "end": v(4779.1, 7279.97) * mm});
            skLineSegment(sketch, "E243.MirrorCS", {"start": v(4973.64, 7141.94) * mm, "end": v(5168.19, 7055.32) * mm});
            skLineSegment(sketch, "E244.MirrorCS", {"start": v(8086.4, 5370.5) * mm, "end": v(8086.4, 5344.8) * mm});
            skLineSegment(sketch, "E245.MirrorCS", {"start": v(7502.75, 5681.76) * mm, "end": v(7697.3, 5595.14) * mm});
            skLineSegment(sketch, "E246.MirrorCS", {"start": v(7308.2, 5819.78) * mm, "end": v(7308.2, 5794.08) * mm});
            skLineSegment(sketch, "E247.MirrorCS", {"start": v(5362.73, 6917.3) * mm, "end": v(5557.28, 6830.68) * mm});
            skLineSegment(sketch, "E248.MirrorCS", {"start": v(8086.4, 5344.8) * mm, "end": v(8280.94, 5258.17) * mm});
            skLineSegment(sketch, "E249.MirrorCS", {"start": v(8670.03, 5007.83) * mm, "end": v(8850.02, 4927.7) * mm});
            skLineSegment(sketch, "E250.MirrorCS", {"start": v(6530.02, 6269.07) * mm, "end": v(6530.02, 6243.37) * mm});
            skLineSegment(sketch, "E251.MirrorCS", {"start": v(8475.49, 5145.85) * mm, "end": v(8475.49, 5120.15) * mm});
            skLineSegment(sketch, "E252.MirrorCS", {"start": v(6140.92, 6493.71) * mm, "end": v(6140.92, 6468) * mm});
            skLineSegment(sketch, "E253.MirrorCS", {"start": v(5168.19, 7055.32) * mm, "end": v(5168.19, 7029.62) * mm});
            skLineSegment(sketch, "E254.MirrorCS", {"start": v(7891.84, 5482.82) * mm, "end": v(7891.84, 5457.11) * mm});
            skLineSegment(sketch, "E255.MirrorCS", {"start": v(6530.02, 6243.37) * mm, "end": v(6724.56, 6156.75) * mm});
            skLineSegment(sketch, "E256.MirrorCS", {"start": v(7891.84, 5457.11) * mm, "end": v(8086.4, 5370.5) * mm});
            skLineSegment(sketch, "E257.MirrorCS", {"start": v(7113.66, 5932.1) * mm, "end": v(7113.66, 5906.4) * mm});
            skLineSegment(sketch, "E258.MirrorCS", {"start": v(6335.47, 6355.69) * mm, "end": v(6530.02, 6269.07) * mm});
            skLineSegment(sketch, "E259.MirrorCS", {"start": v(6335.47, 6381.4) * mm, "end": v(6335.47, 6355.69) * mm});
            skLineSegment(sketch, "E260.MirrorCS", {"start": v(8280.94, 5232.47) * mm, "end": v(8475.49, 5145.85) * mm});
            skLineSegment(sketch, "E261.MirrorCS", {"start": v(7697.3, 5569.44) * mm, "end": v(7891.84, 5482.82) * mm});
            skLineSegment(sketch, "E262.MirrorCS", {"start": v(8475.49, 5120.15) * mm, "end": v(8670.03, 5033.53) * mm});
            skLineSegment(sketch, "E263.MirrorCS", {"start": v(5168.19, 7029.62) * mm, "end": v(5362.73, 6943) * mm});
            skLineSegment(sketch, "E264.MirrorCS", {"start": v(6724.56, 6131.04) * mm, "end": v(6919.1, 6044.43) * mm});
            skLineSegment(sketch, "E265.MirrorCS", {"start": v(5946.38, 6580.33) * mm, "end": v(6140.92, 6493.71) * mm});
            skSolve(sketch);
        }
        {
            var Q0;
            Q0 = qSketchRegion(id + "F8", true);
            var Q1;
            {var subQ0=sQuery(id+"F0.wireOp",EDGE,"E74.trimOffspring");var subQ1=sQuery(id+"F0.wireOp",EDGE,"E11");var subQ2=sQuery(id+"F0.wireOp",EDGE,"E7");var subQ4=sQuery(id+"F0.wireOp",EDGE,"E0");var subQ6=sQuery(id+"F2.wireOp",EDGE,"E83.left");Q1=makeQuery(id+"F5.boolean.opBoolean","SPLIT",FACE,{"disambiguationData":[TD([makeQuery(id+"F1.opExtrude","SWEPT_FACE",FACE,{"disambiguationData":[OSD([subQ4])]})])],"derivedFrom":makeQuery(id+"F3.boolean.opBoolean","MERGE",FACE,{"derivedFrom":[makeQuery(id+"F1.opExtrude","SWEPT_FACE",FACE,{"disambiguationData":[OSD([subQ2])]}),makeQuery(id+"F1.opExtrude","SWEPT_FACE",FACE,{"disambiguationData":[OSD([subQ1])]}),makeQuery(id+"F1.opExtrude","SWEPT_FACE",FACE,{"disambiguationData":[OSD([subQ0])]}),makeQuery(id+"F3.opExtrude","SWEPT_FACE",FACE,{"disambiguationData":[OSD([subQ6])]})]})});}
            extrude(context, id + "F9", {"entities" : qUnion([Q0]), "operationType" : NewBodyOperationType.ADD, "endBound" : BoundingType.UP_TO_SURFACE, "oppositeDirection" : true, "depth" : 25 * mm, "endBoundEntityFace" : qUnion([Q1]), "offsetDistance" : 25 * mm});
        }
        {
            var Q0;
            Q0=qCreatedBy(makeId("Top.planeOp"),FACE);
            var sketch = newSketch(context, id + "F10", { "sketchPlane" : qUnion([Q0])});
            skLineSegment(sketch, "E266.bottom", {"start": v(0, 0) * mm, "end": v(2000, 0) * mm});
            skLineSegment(sketch, "E266.top", {"start": v(0, 8780) * mm, "end": v(2000, 8780) * mm});
            skLineSegment(sketch, "E266.right", {"start": v(2000, 0) * mm, "end": v(2000, 8780) * mm});
            skLineSegment(sketch, "E267.bottom", {"start": v(0, 8530) * mm, "end": v(1750, 8530) * mm});
            skLineSegment(sketch, "E267.top", {"start": v(0, 250) * mm, "end": v(1750, 250) * mm});
            skLineSegment(sketch, "E267.right", {"start": v(1750, 8530) * mm, "end": v(1750, 250) * mm});
            skLineSegment(sketch, "E268", {"start": v(0, 8530) * mm, "end": v(0, 8780) * mm});
            skLineSegment(sketch, "E269", {"start": v(0, 0) * mm, "end": v(0, 250) * mm});
            skSolve(sketch);
        }
        {
            var Q0;
            Q0 = qSketchRegion(id + "F10", true);
            extrude(context, id + "F11", {"entities" : qUnion([Q0]), "operationType" : NewBodyOperationType.ADD, "depth" : 3000 * mm, "offsetDistance" : 25 * mm});
        }
        {
            var Q0;
            Q0=makeQuery(id+"F11.opExtrude","SWEPT_FACE",FACE,{"disambiguationData":[OSD([sQuery(id+"F10.wireOp",EDGE,"E266.right")])]});
            var sketch = newSketch(context, id + "F12", { "sketchPlane" : qUnion([Q0])});
            skLineSegment(sketch, "E270", {"start": v(4390, 4688.82) * mm, "end": v(-250, 3000) * mm, "construction": true});
            skLineSegment(sketch, "E271", {"start": v(-250, 3000) * mm, "end": v(9030, 3000) * mm});
            skLineSegment(sketch, "E272", {"start": v(9030, 3000) * mm, "end": v(4390, 4688.82) * mm, "construction": true});
            skLineSegment(sketch, "E273", {"start": v(4390, 4688.82) * mm, "end": v(4390, 3754.6) * mm, "construction": true});
            skLineSegment(sketch, "E274", {"start": v(4390, 4688.82) * mm, "end": v(4183.37, 4637.3) * mm});
            skLineSegment(sketch, "E275", {"start": v(4183.37, 4637.3) * mm, "end": v(4183.37, 4613.61) * mm});
            skLineSegment(sketch, "E276", {"start": v(4183.37, 4613.61) * mm, "end": v(3976.74, 4562.1) * mm});
            skLineSegment(sketch, "E277", {"start": v(3976.74, 4562.1) * mm, "end": v(3976.74, 4538.4) * mm});
            skLineSegment(sketch, "E278", {"start": v(3976.74, 4538.4) * mm, "end": v(3770.1, 4486.89) * mm});
            skLineSegment(sketch, "E279", {"start": v(3770.1, 4486.89) * mm, "end": v(3770.1, 4463.2) * mm});
            skLineSegment(sketch, "E280", {"start": v(3770.1, 4463.2) * mm, "end": v(3563.47, 4411.68) * mm});
            skLineSegment(sketch, "E281", {"start": v(3563.47, 4411.68) * mm, "end": v(3563.47, 4387.99) * mm});
            skLineSegment(sketch, "E282", {"start": v(3563.47, 4387.99) * mm, "end": v(3356.84, 4336.47) * mm});
            skLineSegment(sketch, "E283", {"start": v(3356.84, 4336.47) * mm, "end": v(3356.84, 4312.78) * mm});
            skLineSegment(sketch, "E284", {"start": v(3356.84, 4312.78) * mm, "end": v(3150.2, 4261.26) * mm});
            skLineSegment(sketch, "E285", {"start": v(3150.2, 4261.26) * mm, "end": v(3150.2, 4237.57) * mm});
            skLineSegment(sketch, "E286", {"start": v(3150.2, 4237.57) * mm, "end": v(2943.57, 4186.05) * mm});
            skLineSegment(sketch, "E287", {"start": v(2943.57, 4186.05) * mm, "end": v(2943.57, 4162.37) * mm});
            skLineSegment(sketch, "E288", {"start": v(2943.57, 4162.37) * mm, "end": v(2736.94, 4110.85) * mm});
            skLineSegment(sketch, "E289", {"start": v(2736.94, 4110.85) * mm, "end": v(2736.94, 4087.16) * mm});
            skLineSegment(sketch, "E290", {"start": v(2736.94, 4087.16) * mm, "end": v(2530.3, 4035.64) * mm});
            skLineSegment(sketch, "E291", {"start": v(2530.3, 4035.64) * mm, "end": v(2530.3, 4011.95) * mm});
            skLineSegment(sketch, "E292", {"start": v(2530.3, 4011.95) * mm, "end": v(2323.68, 3960.43) * mm});
            skLineSegment(sketch, "E293", {"start": v(2323.68, 3960.43) * mm, "end": v(2323.68, 3936.74) * mm});
            skLineSegment(sketch, "E294", {"start": v(2323.68, 3936.74) * mm, "end": v(2117.04, 3885.22) * mm});
            skLineSegment(sketch, "E295", {"start": v(2117.04, 3885.22) * mm, "end": v(2117.04, 3861.53) * mm});
            skLineSegment(sketch, "E296", {"start": v(2117.04, 3861.53) * mm, "end": v(1910.41, 3810.01) * mm});
            skLineSegment(sketch, "E297", {"start": v(1910.41, 3810.01) * mm, "end": v(1910.41, 3786.33) * mm});
            skLineSegment(sketch, "E298", {"start": v(1910.41, 3786.33) * mm, "end": v(1703.78, 3734.8) * mm});
            skLineSegment(sketch, "E299", {"start": v(1703.78, 3734.8) * mm, "end": v(1703.78, 3711.12) * mm});
            skLineSegment(sketch, "E300", {"start": v(1703.78, 3711.12) * mm, "end": v(1497.15, 3659.6) * mm});
            skLineSegment(sketch, "E301", {"start": v(1497.15, 3659.6) * mm, "end": v(1497.15, 3635.9) * mm});
            skLineSegment(sketch, "E302", {"start": v(1497.15, 3635.9) * mm, "end": v(1290.51, 3584.4) * mm});
            skLineSegment(sketch, "E303", {"start": v(1290.51, 3584.4) * mm, "end": v(1290.51, 3560.7) * mm});
            skLineSegment(sketch, "E304", {"start": v(1290.51, 3560.7) * mm, "end": v(1083.88, 3509.18) * mm});
            skLineSegment(sketch, "E305", {"start": v(1083.88, 3509.18) * mm, "end": v(1083.88, 3485.5) * mm});
            skLineSegment(sketch, "E306", {"start": v(1083.88, 3485.5) * mm, "end": v(877.25, 3433.97) * mm});
            skLineSegment(sketch, "E307", {"start": v(877.25, 3433.97) * mm, "end": v(877.25, 3410.29) * mm});
            skLineSegment(sketch, "E308", {"start": v(877.25, 3410.29) * mm, "end": v(670.62, 3358.77) * mm});
            skLineSegment(sketch, "E309", {"start": v(670.62, 3358.77) * mm, "end": v(670.62, 3335.08) * mm});
            skLineSegment(sketch, "E310", {"start": v(670.62, 3335.08) * mm, "end": v(463.99, 3283.56) * mm});
            skLineSegment(sketch, "E311", {"start": v(463.99, 3283.56) * mm, "end": v(463.99, 3259.87) * mm});
            skLineSegment(sketch, "E312", {"start": v(463.99, 3259.87) * mm, "end": v(257.35, 3208.35) * mm});
            skLineSegment(sketch, "E313", {"start": v(257.35, 3208.35) * mm, "end": v(257.35, 3184.66) * mm});
            skLineSegment(sketch, "E314", {"start": v(257.35, 3184.66) * mm, "end": v(50.72, 3133.14) * mm});
            skLineSegment(sketch, "E315", {"start": v(50.72, 3133.14) * mm, "end": v(50.72, 3109.45) * mm});
            skLineSegment(sketch, "E316", {"start": v(50.72, 3109.45) * mm, "end": v(-155.91, 3057.93) * mm});
            skLineSegment(sketch, "E317", {"start": v(-155.91, 3057.93) * mm, "end": v(-155.91, 3034.25) * mm});
            skLineSegment(sketch, "E318", {"start": v(-155.91, 3034.25) * mm, "end": v(-250, 3010.79) * mm});
            skLineSegment(sketch, "E319", {"start": v(-250, 3010.79) * mm, "end": v(-250, 3000) * mm});
            skLineSegment(sketch, "E320.MirrorCS", {"start": v(6456.32, 3960.43) * mm, "end": v(6456.32, 3936.74) * mm});
            skLineSegment(sketch, "E321.MirrorCS", {"start": v(5423.16, 4312.78) * mm, "end": v(5629.8, 4261.26) * mm});
            skLineSegment(sketch, "E322.MirrorCS", {"start": v(5629.8, 4261.26) * mm, "end": v(5629.8, 4237.57) * mm});
            skLineSegment(sketch, "E323.MirrorCS", {"start": v(6456.32, 3936.74) * mm, "end": v(6662.96, 3885.22) * mm});
            skLineSegment(sketch, "E324.MirrorCS", {"start": v(5836.43, 4162.37) * mm, "end": v(6043.06, 4110.85) * mm});
            skLineSegment(sketch, "E325.MirrorCS", {"start": v(9030, 3010.79) * mm, "end": v(9030, 3000) * mm});
            skLineSegment(sketch, "E326.MirrorCS", {"start": v(6043.06, 4110.85) * mm, "end": v(6043.06, 4087.16) * mm});
            skLineSegment(sketch, "E327.MirrorCS", {"start": v(6249.7, 4011.95) * mm, "end": v(6456.32, 3960.43) * mm});
            skLineSegment(sketch, "E328.MirrorCS", {"start": v(5423.16, 4336.47) * mm, "end": v(5423.16, 4312.78) * mm});
            skLineSegment(sketch, "E329.MirrorCS", {"start": v(6869.59, 3786.33) * mm, "end": v(7076.22, 3734.8) * mm});
            skLineSegment(sketch, "E330.MirrorCS", {"start": v(6662.96, 3885.22) * mm, "end": v(6662.96, 3861.53) * mm});
            skLineSegment(sketch, "E331.MirrorCS", {"start": v(5216.53, 4411.68) * mm, "end": v(5216.53, 4387.99) * mm});
            skLineSegment(sketch, "E332.MirrorCS", {"start": v(6869.59, 3810.01) * mm, "end": v(6869.59, 3786.33) * mm});
            skLineSegment(sketch, "E333.MirrorCS", {"start": v(7076.22, 3734.8) * mm, "end": v(7076.22, 3711.12) * mm});
            skLineSegment(sketch, "E334.MirrorCS", {"start": v(5216.53, 4387.99) * mm, "end": v(5423.16, 4336.47) * mm});
            skLineSegment(sketch, "E335.MirrorCS", {"start": v(5836.43, 4186.05) * mm, "end": v(5836.43, 4162.37) * mm});
            skLineSegment(sketch, "E336.MirrorCS", {"start": v(5629.8, 4237.57) * mm, "end": v(5836.43, 4186.05) * mm});
            skLineSegment(sketch, "E337.MirrorCS", {"start": v(6043.06, 4087.16) * mm, "end": v(6249.7, 4035.64) * mm});
            skLineSegment(sketch, "E338.MirrorCS", {"start": v(6249.7, 4035.64) * mm, "end": v(6249.7, 4011.95) * mm});
            skLineSegment(sketch, "E339.MirrorCS", {"start": v(6662.96, 3861.53) * mm, "end": v(6869.59, 3810.01) * mm});
            skLineSegment(sketch, "E340.MirrorCS", {"start": v(8109.38, 3358.77) * mm, "end": v(8109.38, 3335.08) * mm});
            skLineSegment(sketch, "E341.MirrorCS", {"start": v(8935.91, 3034.25) * mm, "end": v(9030, 3010.79) * mm});
            skLineSegment(sketch, "E342.MirrorCS", {"start": v(8522.65, 3208.35) * mm, "end": v(8522.65, 3184.66) * mm});
            skLineSegment(sketch, "E343.MirrorCS", {"start": v(7902.75, 3433.97) * mm, "end": v(7902.75, 3410.29) * mm});
            skLineSegment(sketch, "E344.MirrorCS", {"start": v(8935.91, 3057.93) * mm, "end": v(8935.91, 3034.25) * mm});
            skLineSegment(sketch, "E345.MirrorCS", {"start": v(8316.01, 3283.56) * mm, "end": v(8316.01, 3259.87) * mm});
            skLineSegment(sketch, "E346.MirrorCS", {"start": v(8109.38, 3335.08) * mm, "end": v(8316.01, 3283.56) * mm});
            skLineSegment(sketch, "E347.MirrorCS", {"start": v(7489.49, 3584.4) * mm, "end": v(7489.49, 3560.7) * mm});
            skLineSegment(sketch, "E348.MirrorCS", {"start": v(7076.22, 3711.12) * mm, "end": v(7282.85, 3659.6) * mm});
            skLineSegment(sketch, "E349.MirrorCS", {"start": v(4596.63, 4637.3) * mm, "end": v(4596.63, 4613.61) * mm});
            skLineSegment(sketch, "E350.MirrorCS", {"start": v(7489.49, 3560.7) * mm, "end": v(7696.12, 3509.18) * mm});
            skLineSegment(sketch, "E351.MirrorCS", {"start": v(4390, 4688.82) * mm, "end": v(4596.63, 4637.3) * mm});
            skLineSegment(sketch, "E352.MirrorCS", {"start": v(5009.9, 4463.2) * mm, "end": v(5216.53, 4411.68) * mm});
            skLineSegment(sketch, "E353.MirrorCS", {"start": v(7696.12, 3485.5) * mm, "end": v(7902.75, 3433.97) * mm});
            skLineSegment(sketch, "E354.MirrorCS", {"start": v(8729.28, 3133.14) * mm, "end": v(8729.28, 3109.45) * mm});
            skLineSegment(sketch, "E355.MirrorCS", {"start": v(7282.85, 3635.9) * mm, "end": v(7489.49, 3584.4) * mm});
            skLineSegment(sketch, "E356.MirrorCS", {"start": v(8729.28, 3109.45) * mm, "end": v(8935.91, 3057.93) * mm});
            skLineSegment(sketch, "E357.MirrorCS", {"start": v(5009.9, 4486.89) * mm, "end": v(5009.9, 4463.2) * mm});
            skLineSegment(sketch, "E358.MirrorCS", {"start": v(8316.01, 3259.87) * mm, "end": v(8522.65, 3208.35) * mm});
            skLineSegment(sketch, "E359.MirrorCS", {"start": v(4596.63, 4613.61) * mm, "end": v(4803.26, 4562.1) * mm});
            skLineSegment(sketch, "E360.MirrorCS", {"start": v(4803.26, 4538.4) * mm, "end": v(5009.9, 4486.89) * mm});
            skLineSegment(sketch, "E361.MirrorCS", {"start": v(8522.65, 3184.66) * mm, "end": v(8729.28, 3133.14) * mm});
            skLineSegment(sketch, "E362.MirrorCS", {"start": v(7696.12, 3509.18) * mm, "end": v(7696.12, 3485.5) * mm});
            skLineSegment(sketch, "E363.MirrorCS", {"start": v(4803.26, 4562.1) * mm, "end": v(4803.26, 4538.4) * mm});
            skLineSegment(sketch, "E364.MirrorCS", {"start": v(7282.85, 3659.6) * mm, "end": v(7282.85, 3635.9) * mm});
            skLineSegment(sketch, "E365.MirrorCS", {"start": v(7902.75, 3410.29) * mm, "end": v(8109.38, 3358.77) * mm});
            skSolve(sketch);
        }
        {
            var Q0;
            Q0 = qSketchRegion(id + "F12", true);
            var Q1;
            Q1=makeQuery(id+"F9.boolean.opBoolean","MERGE",FACE,{"derivedFrom":[makeQuery(id+"F3.boolean.opBoolean","MERGE",FACE,{"derivedFrom":[makeQuery(id+"F1.opExtrude","SWEPT_FACE",FACE,{"disambiguationData":[OSD([sQuery(id+"F0.wireOp",EDGE,"E5")])]}),makeQuery(id+"F1.opExtrude","SWEPT_FACE",FACE,{"disambiguationData":[OSD([sQuery(id+"F0.wireOp",EDGE,"E77.trimOffspring")])]}),makeQuery(id+"F3.opExtrude","SWEPT_FACE",FACE,{"disambiguationData":[OSD([sQuery(id+"F2.wireOp",EDGE,"E83.right")])]})]}),makeQuery(id+"F9.opExtrude","CAP_FACE",FACE,{"disambiguationData":[OSD([sQuery(id+"F8.wireOp",EDGE,"E166"),sQuery(id+"F8.wireOp",EDGE,"E167"),sQuery(id+"F8.wireOp",EDGE,"E168")])],"isStart":true})]});
            extrude(context, id + "F13", {"entities" : qUnion([Q0]), "operationType" : NewBodyOperationType.ADD, "endBound" : BoundingType.UP_TO_SURFACE, "oppositeDirection" : true, "depth" : 25 * mm, "endBoundEntityFace" : qUnion([Q1]), "offsetDistance" : 25 * mm});
        }
        {
            var Q0;
            Q0=makeQuery(id+"F3.boolean.opBoolean","MERGE",FACE,{"derivedFrom":[makeQuery(id+"F1.opExtrude","SWEPT_FACE",FACE,{"disambiguationData":[OSD([sQuery(id+"F0.wireOp",EDGE,"E4")])]}),makeQuery(id+"F3.opExtrude","SWEPT_FACE",FACE,{"disambiguationData":[OSD([sQuery(id+"F2.wireOp",EDGE,"E83.top")])]})]});
            var sketch = newSketch(context, id + "F14", { "sketchPlane" : qUnion([Q0])});
            skLineSegment(sketch, "E366.bottom", {"start": v(-7150, 4600) * mm, "end": v(-5100, 4600) * mm});
            skLineSegment(sketch, "E366.top", {"start": v(-7150, 3800) * mm, "end": v(-5100, 3800) * mm});
            skLineSegment(sketch, "E366.left", {"start": v(-7150, 4600) * mm, "end": v(-7150, 3800) * mm});
            skLineSegment(sketch, "E366.right", {"start": v(-5100, 4600) * mm, "end": v(-5100, 3800) * mm});
            skLineSegment(sketch, "E367.bottom", {"start": v(-4600, 4600) * mm, "end": v(-3500, 4600) * mm});
            skLineSegment(sketch, "E367.top", {"start": v(-4600, 3800) * mm, "end": v(-3500, 3800) * mm});
            skLineSegment(sketch, "E367.left", {"start": v(-4600, 4600) * mm, "end": v(-4600, 3800) * mm});
            skLineSegment(sketch, "E367.right", {"start": v(-3500, 4600) * mm, "end": v(-3500, 3800) * mm});
            skLineSegment(sketch, "E368.bottom", {"start": v(-2300, 4600) * mm, "end": v(-300, 4600) * mm});
            skLineSegment(sketch, "E368.top", {"start": v(-2300, 3400) * mm, "end": v(-300, 3400) * mm});
            skLineSegment(sketch, "E368.left", {"start": v(-2300, 4600) * mm, "end": v(-2300, 3400) * mm});
            skLineSegment(sketch, "E368.right", {"start": v(-300, 4600) * mm, "end": v(-300, 3400) * mm});
            skLineSegment(sketch, "E369.bottom", {"start": v(-300, 2300) * mm, "end": v(1700, 2300) * mm});
            skLineSegment(sketch, "E369.top", {"start": v(-300, 1300) * mm, "end": v(1700, 1300) * mm});
            skLineSegment(sketch, "E369.left", {"start": v(-300, 2300) * mm, "end": v(-300, 1300) * mm});
            skLineSegment(sketch, "E369.right", {"start": v(1700, 2300) * mm, "end": v(1700, 1300) * mm});
            skPoint(sketch, "E370", {"position": v(-5100, 3708.38) * mm});
            skLineSegment(sketch, "E371.bottom", {"start": v(-7050, 4500) * mm, "end": v(-6650, 4500) * mm});
            skLineSegment(sketch, "E371.top", {"start": v(-7050, 4300) * mm, "end": v(-6650, 4300) * mm});
            skLineSegment(sketch, "E371.left", {"start": v(-7050, 4500) * mm, "end": v(-7050, 4300) * mm});
            skLineSegment(sketch, "E371.right", {"start": v(-6650, 4500) * mm, "end": v(-6650, 4300) * mm});
            skPoint(sketch, "E372.firstSnap0", {"position": v(-7150, 4200) * mm});
            skLineSegment(sketch, "E372.bottom", {"start": v(-7050, 4200) * mm, "end": v(-6650, 4200) * mm});
            skLineSegment(sketch, "E372.top", {"start": v(-7050, 3900) * mm, "end": v(-6650, 3900) * mm});
            skLineSegment(sketch, "E372.left", {"start": v(-7050, 4200) * mm, "end": v(-7050, 3900) * mm});
            skLineSegment(sketch, "E372.right", {"start": v(-6650, 4200) * mm, "end": v(-6650, 3900) * mm});
            skLineSegment(sketch, "E373.bottom", {"start": v(-6550, 4500) * mm, "end": v(-5200, 4500) * mm});
            skLineSegment(sketch, "E373.top", {"start": v(-6550, 3900) * mm, "end": v(-5200, 3900) * mm});
            skLineSegment(sketch, "E373.left", {"start": v(-6550, 4500) * mm, "end": v(-6550, 3900) * mm});
            skLineSegment(sketch, "E373.right", {"start": v(-5200, 4500) * mm, "end": v(-5200, 3900) * mm});
            skLineSegment(sketch, "E374.bottom", {"start": v(-4500, 4500) * mm, "end": v(-4100, 4500) * mm});
            skLineSegment(sketch, "E374.top", {"start": v(-4500, 4300) * mm, "end": v(-4100, 4300) * mm});
            skLineSegment(sketch, "E374.left", {"start": v(-4500, 4500) * mm, "end": v(-4500, 4300) * mm});
            skLineSegment(sketch, "E374.right", {"start": v(-4100, 4500) * mm, "end": v(-4100, 4300) * mm});
            skLineSegment(sketch, "E375.bottom", {"start": v(-4500, 4200) * mm, "end": v(-4100, 4200) * mm});
            skLineSegment(sketch, "E375.top", {"start": v(-4500, 3900) * mm, "end": v(-4100, 3900) * mm});
            skLineSegment(sketch, "E375.left", {"start": v(-4500, 4200) * mm, "end": v(-4500, 3900) * mm});
            skLineSegment(sketch, "E375.right", {"start": v(-4100, 4200) * mm, "end": v(-4100, 3900) * mm});
            skLineSegment(sketch, "E376.bottom", {"start": v(-4000, 4500) * mm, "end": v(-3600, 4500) * mm});
            skLineSegment(sketch, "E376.top", {"start": v(-4000, 3900) * mm, "end": v(-3600, 3900) * mm});
            skLineSegment(sketch, "E376.left", {"start": v(-4000, 4500) * mm, "end": v(-4000, 3900) * mm});
            skLineSegment(sketch, "E376.right", {"start": v(-3600, 4500) * mm, "end": v(-3600, 3900) * mm});
            skLineSegment(sketch, "E377.bottom", {"start": v(-2200, 4500) * mm, "end": v(-1800, 4500) * mm});
            skLineSegment(sketch, "E377.top", {"start": v(-2200, 4300) * mm, "end": v(-1800, 4300) * mm});
            skLineSegment(sketch, "E377.left", {"start": v(-2200, 4500) * mm, "end": v(-2200, 4300) * mm});
            skLineSegment(sketch, "E377.right", {"start": v(-1800, 4500) * mm, "end": v(-1800, 4300) * mm});
            skLineSegment(sketch, "E378.bottom", {"start": v(-2200, 4200) * mm, "end": v(-1800, 4200) * mm});
            skLineSegment(sketch, "E378.top", {"start": v(-2200, 3500) * mm, "end": v(-1800, 3500) * mm});
            skLineSegment(sketch, "E378.left", {"start": v(-2200, 4200) * mm, "end": v(-2200, 3500) * mm});
            skLineSegment(sketch, "E378.right", {"start": v(-1800, 4200) * mm, "end": v(-1800, 3500) * mm});
            skLineSegment(sketch, "E379.bottom", {"start": v(-1700, 4500) * mm, "end": v(-400, 4500) * mm});
            skLineSegment(sketch, "E379.top", {"start": v(-1700, 3500) * mm, "end": v(-400, 3500) * mm});
            skLineSegment(sketch, "E379.left", {"start": v(-1700, 4500) * mm, "end": v(-1700, 3500) * mm});
            skLineSegment(sketch, "E379.right", {"start": v(-400, 4500) * mm, "end": v(-400, 3500) * mm});
            skLineSegment(sketch, "E380.bottom", {"start": v(-200, 2200) * mm, "end": v(200, 2200) * mm});
            skLineSegment(sketch, "E380.top", {"start": v(-200, 1900) * mm, "end": v(200, 1900) * mm});
            skLineSegment(sketch, "E380.left", {"start": v(-200, 2200) * mm, "end": v(-200, 1900) * mm});
            skLineSegment(sketch, "E380.right", {"start": v(200, 2200) * mm, "end": v(200, 1900) * mm});
            skLineSegment(sketch, "E381.bottom", {"start": v(-200, 1800) * mm, "end": v(200, 1800) * mm});
            skLineSegment(sketch, "E381.top", {"start": v(-200, 1400) * mm, "end": v(200, 1400) * mm});
            skLineSegment(sketch, "E381.left", {"start": v(-200, 1800) * mm, "end": v(-200, 1400) * mm});
            skLineSegment(sketch, "E381.right", {"start": v(200, 1800) * mm, "end": v(200, 1400) * mm});
            skLineSegment(sketch, "E382.bottom", {"start": v(300, 2200) * mm, "end": v(1600, 2200) * mm});
            skLineSegment(sketch, "E382.top", {"start": v(300, 1400) * mm, "end": v(1600, 1400) * mm});
            skLineSegment(sketch, "E382.left", {"start": v(300, 2200) * mm, "end": v(300, 1400) * mm});
            skLineSegment(sketch, "E382.right", {"start": v(1600, 2200) * mm, "end": v(1600, 1400) * mm});
            skSolve(sketch);
        }
        {
            var Q0;
            Q0 = qSketchRegion(id + "F14", true);
            extrude(context, id + "F15", {"entities" : qUnion([Q0]), "operationType" : NewBodyOperationType.ADD, "depth" : 25 * mm, "offsetDistance" : 25 * mm});
        }
        {
            var Q0;
            Q0=makeQuery(id+"F1.opExtrude","SWEPT_FACE",FACE,{"disambiguationData":[OSD([sQuery(id+"F0.wireOp",EDGE,"E2")])]});
            var sketch = newSketch(context, id + "F16", { "sketchPlane" : qUnion([Q0])});
            skLineSegment(sketch, "E383.bottom", {"start": v(-6850, 2300) * mm, "end": v(-5130, 2300) * mm});
            skLineSegment(sketch, "E383.top", {"start": v(-6850, 1160) * mm, "end": v(-5130, 1160) * mm});
            skLineSegment(sketch, "E383.left", {"start": v(-6850, 2300) * mm, "end": v(-6850, 1160) * mm});
            skLineSegment(sketch, "E383.right", {"start": v(-5130, 2300) * mm, "end": v(-5130, 1160) * mm});
            skLineSegment(sketch, "E384", {"start": v(-9750, 0) * mm, "end": v(-9750, 2150) * mm});
            skLineSegment(sketch, "E385", {"start": v(-9750, 2150) * mm, "end": v(-7550, 2150) * mm});
            skLineSegment(sketch, "E386", {"start": v(-7550, 2150) * mm, "end": v(-7550, 0) * mm});
            skLineSegment(sketch, "E387", {"start": v(-7550, 0) * mm, "end": v(-7600, 0) * mm});
            skLineSegment(sketch, "E388", {"start": v(-7600, 0) * mm, "end": v(-7600, 2100) * mm});
            skLineSegment(sketch, "E389", {"start": v(-7600, 2100) * mm, "end": v(-9700, 2100) * mm});
            skLineSegment(sketch, "E390", {"start": v(-9700, 2100) * mm, "end": v(-9700, 0) * mm});
            skLineSegment(sketch, "E391", {"start": v(-9700, 0) * mm, "end": v(-9750, 0) * mm});
            skLineSegment(sketch, "E392.bottom", {"start": v(-6750, 2200) * mm, "end": v(-6350, 2200) * mm});
            skLineSegment(sketch, "E392.top", {"start": v(-6750, 1900) * mm, "end": v(-6350, 1900) * mm});
            skLineSegment(sketch, "E392.left", {"start": v(-6750, 2200) * mm, "end": v(-6750, 1900) * mm});
            skLineSegment(sketch, "E392.right", {"start": v(-6350, 2200) * mm, "end": v(-6350, 1900) * mm});
            skLineSegment(sketch, "E393.bottom", {"start": v(-6750, 1800) * mm, "end": v(-6350, 1800) * mm});
            skLineSegment(sketch, "E393.top", {"start": v(-6750, 1260) * mm, "end": v(-6350, 1260) * mm});
            skLineSegment(sketch, "E393.left", {"start": v(-6750, 1800) * mm, "end": v(-6750, 1260) * mm});
            skLineSegment(sketch, "E393.right", {"start": v(-6350, 1800) * mm, "end": v(-6350, 1260) * mm});
            skLineSegment(sketch, "E394.bottom", {"start": v(-6250, 2200) * mm, "end": v(-5230, 2200) * mm});
            skLineSegment(sketch, "E394.top", {"start": v(-6250, 1260) * mm, "end": v(-5230, 1260) * mm});
            skLineSegment(sketch, "E394.left", {"start": v(-6250, 2200) * mm, "end": v(-6250, 1260) * mm});
            skLineSegment(sketch, "E394.right", {"start": v(-5230, 2200) * mm, "end": v(-5230, 1260) * mm});
            skLineSegment(sketch, "E395.bottom", {"start": v(-9600, 2000) * mm, "end": v(-9325, 2000) * mm});
            skLineSegment(sketch, "E395.top", {"start": v(-9600, 100) * mm, "end": v(-9325, 100) * mm});
            skLineSegment(sketch, "E395.left", {"start": v(-9600, 2000) * mm, "end": v(-9600, 100) * mm});
            skLineSegment(sketch, "E395.right", {"start": v(-9325, 2000) * mm, "end": v(-9325, 100) * mm});
            skLineSegment(sketch, "E396.bottom", {"start": v(-9275, 2000) * mm, "end": v(-9000, 2000) * mm});
            skLineSegment(sketch, "E396.top", {"start": v(-9275, 100) * mm, "end": v(-9000, 100) * mm});
            skLineSegment(sketch, "E396.left", {"start": v(-9275, 2000) * mm, "end": v(-9275, 100) * mm});
            skLineSegment(sketch, "E396.right", {"start": v(-9000, 2000) * mm, "end": v(-9000, 100) * mm});
            skLineSegment(sketch, "E397.bottom", {"start": v(-8950, 2000) * mm, "end": v(-8675, 2000) * mm});
            skLineSegment(sketch, "E397.top", {"start": v(-8950, 100) * mm, "end": v(-8675, 100) * mm});
            skLineSegment(sketch, "E397.left", {"start": v(-8950, 2000) * mm, "end": v(-8950, 100) * mm});
            skLineSegment(sketch, "E397.right", {"start": v(-8675, 2000) * mm, "end": v(-8675, 100) * mm});
            skLineSegment(sketch, "E398.bottom", {"start": v(-8625, 2000) * mm, "end": v(-8350, 2000) * mm});
            skLineSegment(sketch, "E398.top", {"start": v(-8625, 100) * mm, "end": v(-8350, 100) * mm});
            skLineSegment(sketch, "E398.left", {"start": v(-8625, 2000) * mm, "end": v(-8625, 100) * mm});
            skLineSegment(sketch, "E398.right", {"start": v(-8350, 2000) * mm, "end": v(-8350, 100) * mm});
            skLineSegment(sketch, "E399.bottom", {"start": v(-8300, 2000) * mm, "end": v(-8025, 2000) * mm});
            skLineSegment(sketch, "E399.top", {"start": v(-8300, 100) * mm, "end": v(-8025, 100) * mm});
            skLineSegment(sketch, "E399.left", {"start": v(-8300, 2000) * mm, "end": v(-8300, 100) * mm});
            skLineSegment(sketch, "E399.right", {"start": v(-8025, 2000) * mm, "end": v(-8025, 100) * mm});
            skLineSegment(sketch, "E400.bottom", {"start": v(-7975, 2000) * mm, "end": v(-7700, 2000) * mm});
            skLineSegment(sketch, "E400.top", {"start": v(-7975, 100) * mm, "end": v(-7700, 100) * mm});
            skLineSegment(sketch, "E400.left", {"start": v(-7975, 2000) * mm, "end": v(-7975, 100) * mm});
            skLineSegment(sketch, "E400.right", {"start": v(-7700, 2000) * mm, "end": v(-7700, 100) * mm});
            skSolve(sketch);
        }
        {
            var Q0;
            Q0 = qSketchRegion(id + "F16", true);
            extrude(context, id + "F17", {"entities" : qUnion([Q0]), "operationType" : NewBodyOperationType.ADD, "depth" : 25 * mm, "offsetDistance" : 25 * mm});
        }
        {
            var Q0;
            Q0=makeQuery(id+"F3.boolean.opBoolean","MERGE",FACE,{"derivedFrom":[makeQuery(id+"F1.opExtrude","SWEPT_FACE",FACE,{"disambiguationData":[OSD([sQuery(id+"F0.wireOp",EDGE,"E6")])]}),makeQuery(id+"F3.opExtrude","SWEPT_FACE",FACE,{"disambiguationData":[OSD([sQuery(id+"F2.wireOp",EDGE,"E83.bottom")])]})]});
            var sketch = newSketch(context, id + "F18", { "sketchPlane" : qUnion([Q0])});
            skLineSegment(sketch, "E401.bottom", {"start": v(300, 4600) * mm, "end": v(2650, 4600) * mm});
            skLineSegment(sketch, "E401.top", {"start": v(300, 3600) * mm, "end": v(2650, 3600) * mm});
            skLineSegment(sketch, "E401.left", {"start": v(300, 4600) * mm, "end": v(300, 3600) * mm});
            skLineSegment(sketch, "E401.right", {"start": v(2650, 4600) * mm, "end": v(2650, 3600) * mm});
            skLineSegment(sketch, "E402.bottom", {"start": v(4800, 4600) * mm, "end": v(7150, 4600) * mm});
            skLineSegment(sketch, "E402.top", {"start": v(4800, 3600) * mm, "end": v(7150, 3600) * mm});
            skLineSegment(sketch, "E402.left", {"start": v(4800, 4600) * mm, "end": v(4800, 3600) * mm});
            skLineSegment(sketch, "E402.right", {"start": v(7150, 4600) * mm, "end": v(7150, 3600) * mm});
            skLineSegment(sketch, "E403.bottom", {"start": v(300, 2500) * mm, "end": v(2640, 2500) * mm});
            skLineSegment(sketch, "E403.top", {"start": v(300, 1350) * mm, "end": v(2640, 1350) * mm});
            skLineSegment(sketch, "E403.left", {"start": v(300, 2500) * mm, "end": v(300, 1350) * mm});
            skLineSegment(sketch, "E403.right", {"start": v(2640, 2500) * mm, "end": v(2640, 1350) * mm});
            skLineSegment(sketch, "E404.bottom", {"start": v(4800, 300) * mm, "end": v(7150, 300) * mm});
            skLineSegment(sketch, "E404.top", {"start": v(4800, 2500) * mm, "end": v(7150, 2500) * mm});
            skLineSegment(sketch, "E404.left", {"start": v(4800, 300) * mm, "end": v(4800, 2500) * mm});
            skLineSegment(sketch, "E404.right", {"start": v(7150, 300) * mm, "end": v(7150, 2500) * mm});
            skLineSegment(sketch, "E405.bottom", {"start": v(7050, 4500) * mm, "end": v(6650, 4500) * mm});
            skLineSegment(sketch, "E405.top", {"start": v(7050, 4300) * mm, "end": v(6650, 4300) * mm});
            skLineSegment(sketch, "E405.left", {"start": v(7050, 4500) * mm, "end": v(7050, 4300) * mm});
            skLineSegment(sketch, "E405.right", {"start": v(6650, 4500) * mm, "end": v(6650, 4300) * mm});
            skLineSegment(sketch, "E406.bottom", {"start": v(7050, 4200) * mm, "end": v(6650, 4200) * mm});
            skLineSegment(sketch, "E406.top", {"start": v(7050, 3700) * mm, "end": v(6650, 3700) * mm});
            skLineSegment(sketch, "E406.left", {"start": v(7050, 4200) * mm, "end": v(7050, 3700) * mm});
            skLineSegment(sketch, "E406.right", {"start": v(6650, 4200) * mm, "end": v(6650, 3700) * mm});
            skLineSegment(sketch, "E407.bottom", {"start": v(4900, 4500) * mm, "end": v(5300, 4500) * mm});
            skLineSegment(sketch, "E407.top", {"start": v(4900, 4300) * mm, "end": v(5300, 4300) * mm});
            skLineSegment(sketch, "E407.left", {"start": v(4900, 4500) * mm, "end": v(4900, 4300) * mm});
            skLineSegment(sketch, "E407.right", {"start": v(5300, 4500) * mm, "end": v(5300, 4300) * mm});
            skLineSegment(sketch, "E408.bottom", {"start": v(4900, 4200) * mm, "end": v(5300, 4200) * mm});
            skLineSegment(sketch, "E408.top", {"start": v(4900, 3700) * mm, "end": v(5300, 3700) * mm});
            skLineSegment(sketch, "E408.left", {"start": v(4900, 4200) * mm, "end": v(4900, 3700) * mm});
            skLineSegment(sketch, "E408.right", {"start": v(5300, 4200) * mm, "end": v(5300, 3700) * mm});
            skLineSegment(sketch, "E409.bottom", {"start": v(5400, 4500) * mm, "end": v(6550, 4500) * mm});
            skLineSegment(sketch, "E409.top", {"start": v(5400, 3700) * mm, "end": v(6550, 3700) * mm});
            skLineSegment(sketch, "E409.left", {"start": v(5400, 4500) * mm, "end": v(5400, 3700) * mm});
            skLineSegment(sketch, "E409.right", {"start": v(6550, 4500) * mm, "end": v(6550, 3700) * mm});
            skLineSegment(sketch, "E410.bottom", {"start": v(400, 4500) * mm, "end": v(800, 4500) * mm});
            skLineSegment(sketch, "E410.top", {"start": v(400, 4300) * mm, "end": v(800, 4300) * mm});
            skLineSegment(sketch, "E410.left", {"start": v(400, 4500) * mm, "end": v(400, 4300) * mm});
            skLineSegment(sketch, "E410.right", {"start": v(800, 4500) * mm, "end": v(800, 4300) * mm});
            skLineSegment(sketch, "E411.bottom", {"start": v(400, 4200) * mm, "end": v(800, 4200) * mm});
            skLineSegment(sketch, "E411.top", {"start": v(400, 3700) * mm, "end": v(800, 3700) * mm});
            skLineSegment(sketch, "E411.left", {"start": v(400, 4200) * mm, "end": v(400, 3700) * mm});
            skLineSegment(sketch, "E411.right", {"start": v(800, 4200) * mm, "end": v(800, 3700) * mm});
            skLineSegment(sketch, "E412.bottom", {"start": v(900, 4500) * mm, "end": v(2050, 4500) * mm});
            skLineSegment(sketch, "E412.top", {"start": v(900, 3700) * mm, "end": v(2050, 3700) * mm});
            skLineSegment(sketch, "E412.left", {"start": v(900, 4500) * mm, "end": v(900, 3700) * mm});
            skLineSegment(sketch, "E412.right", {"start": v(2050, 4500) * mm, "end": v(2050, 3700) * mm});
            skLineSegment(sketch, "E413.bottom", {"start": v(2150, 4500) * mm, "end": v(2550, 4500) * mm});
            skLineSegment(sketch, "E413.top", {"start": v(2150, 4300) * mm, "end": v(2550, 4300) * mm});
            skLineSegment(sketch, "E413.left", {"start": v(2150, 4500) * mm, "end": v(2150, 4300) * mm});
            skLineSegment(sketch, "E413.right", {"start": v(2550, 4500) * mm, "end": v(2550, 4300) * mm});
            skLineSegment(sketch, "E414.bottom", {"start": v(2150, 4200) * mm, "end": v(2550, 4200) * mm});
            skLineSegment(sketch, "E414.top", {"start": v(2150, 3700) * mm, "end": v(2550, 3700) * mm});
            skLineSegment(sketch, "E414.left", {"start": v(2150, 4200) * mm, "end": v(2150, 3700) * mm});
            skLineSegment(sketch, "E414.right", {"start": v(2550, 4200) * mm, "end": v(2550, 3700) * mm});
            skLineSegment(sketch, "E415.bottom", {"start": v(400, 2400) * mm, "end": v(800, 2400) * mm});
            skLineSegment(sketch, "E415.top", {"start": v(400, 2200) * mm, "end": v(800, 2200) * mm});
            skLineSegment(sketch, "E415.left", {"start": v(400, 2400) * mm, "end": v(400, 2200) * mm});
            skLineSegment(sketch, "E415.right", {"start": v(800, 2400) * mm, "end": v(800, 2200) * mm});
            skLineSegment(sketch, "E416.bottom", {"start": v(400, 2100) * mm, "end": v(800, 2100) * mm});
            skLineSegment(sketch, "E416.top", {"start": v(400, 1450) * mm, "end": v(800, 1450) * mm});
            skLineSegment(sketch, "E416.left", {"start": v(400, 2100) * mm, "end": v(400, 1450) * mm});
            skLineSegment(sketch, "E416.right", {"start": v(800, 2100) * mm, "end": v(800, 1450) * mm});
            skLineSegment(sketch, "E417.bottom", {"start": v(900, 2400) * mm, "end": v(2040, 2400) * mm});
            skLineSegment(sketch, "E417.top", {"start": v(900, 1450) * mm, "end": v(2040, 1450) * mm});
            skLineSegment(sketch, "E417.left", {"start": v(900, 2400) * mm, "end": v(900, 1450) * mm});
            skLineSegment(sketch, "E417.right", {"start": v(2040, 2400) * mm, "end": v(2040, 1450) * mm});
            skLineSegment(sketch, "E418.bottom", {"start": v(2140, 2400) * mm, "end": v(2540, 2400) * mm});
            skLineSegment(sketch, "E418.top", {"start": v(2140, 2200) * mm, "end": v(2540, 2200) * mm});
            skLineSegment(sketch, "E418.left", {"start": v(2140, 2400) * mm, "end": v(2140, 2200) * mm});
            skLineSegment(sketch, "E418.right", {"start": v(2540, 2400) * mm, "end": v(2540, 2200) * mm});
            skLineSegment(sketch, "E419.bottom", {"start": v(2140, 2100) * mm, "end": v(2540, 2100) * mm});
            skLineSegment(sketch, "E419.top", {"start": v(2140, 1450) * mm, "end": v(2540, 1450) * mm});
            skLineSegment(sketch, "E419.left", {"start": v(2140, 2100) * mm, "end": v(2140, 1450) * mm});
            skLineSegment(sketch, "E419.right", {"start": v(2540, 2100) * mm, "end": v(2540, 1450) * mm});
            skLineSegment(sketch, "E420.bottom", {"start": v(4900, 2400) * mm, "end": v(7050, 2400) * mm});
            skLineSegment(sketch, "E420.top", {"start": v(4900, 400) * mm, "end": v(7050, 400) * mm});
            skLineSegment(sketch, "E420.left", {"start": v(4900, 2400) * mm, "end": v(4900, 400) * mm});
            skLineSegment(sketch, "E420.right", {"start": v(7050, 2400) * mm, "end": v(7050, 400) * mm});
            skSolve(sketch);
        }
        {
            var Q0;
            Q0 = qSketchRegion(id + "F18", true);
            extrude(context, id + "F19", {"entities" : qUnion([Q0]), "operationType" : NewBodyOperationType.ADD, "depth" : 25 * mm, "offsetDistance" : 25 * mm});
        }
        {
            var Q0;
            {var subQ0=sQuery(id+"F0.wireOp",EDGE,"E55.trimOffspring");var subQ1=sQuery(id+"F0.wireOp",EDGE,"E29");var subQ2=sQuery(id+"F0.wireOp",EDGE,"E42");var subQ3=sQuery(id+"F0.wireOp",EDGE,"E18");var subQ4=sQuery(id+"F0.wireOp",EDGE,"E21");var subQ5=sQuery(id+"F0.wireOp",EDGE,"E12");var subQ6=sQuery(id+"F0.wireOp",EDGE,"E33");var subQ7=sQuery(id+"F0.wireOp",EDGE,"E13");var subQ8=sQuery(id+"F0.wireOp",EDGE,"E35");var subQ9=sQuery(id+"F0.wireOp",EDGE,"E15");var subQ10=sQuery(id+"F0.wireOp",EDGE,"E73.trimOffspring");Q0=makeQuery(id+"F3.boolean.opBoolean","SPLIT",FACE,{"disambiguationData":[TD([makeQuery(id+"F1.opExtrude","SWEPT_FACE",FACE,{"disambiguationData":[OSD([subQ5])]})])],"derivedFrom":makeQuery(id+"F1.opExtrude","CAP_FACE",FACE,{"disambiguationData":[OSD([sQuery(id+"F0.wireOp",EDGE,"E0"),sQuery(id+"F0.wireOp",EDGE,"E1"),sQuery(id+"F0.wireOp",EDGE,"E2"),sQuery(id+"F0.wireOp",EDGE,"E3"),sQuery(id+"F0.wireOp",EDGE,"E4"),sQuery(id+"F0.wireOp",EDGE,"E5"),sQuery(id+"F0.wireOp",EDGE,"E6"),sQuery(id+"F0.wireOp",EDGE,"E7"),sQuery(id+"F0.wireOp",EDGE,"E8"),sQuery(id+"F0.wireOp",EDGE,"E9"),sQuery(id+"F0.wireOp",EDGE,"E10"),sQuery(id+"F0.wireOp",EDGE,"E11"),subQ5,subQ7,sQuery(id+"F0.wireOp",EDGE,"E14"),subQ9,sQuery(id+"F0.wireOp",EDGE,"E16"),sQuery(id+"F0.wireOp",EDGE,"E17"),subQ3,sQuery(id+"F0.wireOp",EDGE,"E20"),subQ4,sQuery(id+"F0.wireOp",EDGE,"E22"),sQuery(id+"F0.wireOp",EDGE,"E25"),subQ1,sQuery(id+"F0.wireOp",EDGE,"E30"),sQuery(id+"F0.wireOp",EDGE,"E32"),subQ6,subQ8,sQuery(id+"F0.wireOp",EDGE,"E36"),sQuery(id+"F0.wireOp",EDGE,"E37"),sQuery(id+"F0.wireOp",EDGE,"E40.trimOffspring"),sQuery(id+"F0.wireOp",EDGE,"E41.trimOffspring"),subQ2,sQuery(id+"F0.wireOp",EDGE,"E46"),sQuery(id+"F0.wireOp",EDGE,"E47"),sQuery(id+"F0.wireOp",EDGE,"E48"),sQuery(id+"F0.wireOp",EDGE,"E49"),sQuery(id+"F0.wireOp",EDGE,"E50.trimOffspring"),sQuery(id+"F0.wireOp",EDGE,"E51.trimOffspring"),sQuery(id+"F0.wireOp",EDGE,"E52"),sQuery(id+"F0.wireOp",EDGE,"E53"),sQuery(id+"F0.wireOp",EDGE,"E54.trimOffspring"),subQ0,sQuery(id+"F0.wireOp",EDGE,"E56"),sQuery(id+"F0.wireOp",EDGE,"E63"),sQuery(id+"F0.wireOp",EDGE,"E64.trimOffspring"),sQuery(id+"F0.wireOp",EDGE,"E65.trimOffspring"),sQuery(id+"F0.wireOp",EDGE,"E66"),sQuery(id+"F0.wireOp",EDGE,"E67"),sQuery(id+"F0.wireOp",EDGE,"E69.trimOffspring"),sQuery(id+"F0.wireOp",EDGE,"E71"),sQuery(id+"F0.wireOp",EDGE,"E72"),subQ10,sQuery(id+"F0.wireOp",EDGE,"E74.trimOffspring"),sQuery(id+"F0.wireOp",EDGE,"E75"),sQuery(id+"F0.wireOp",EDGE,"E76"),sQuery(id+"F0.wireOp",EDGE,"E77.trimOffspring"),sQuery(id+"F0.wireOp",EDGE,"E78.trimOffspring"),sQuery(id+"F0.wireOp",EDGE,"E79"),sQuery(id+"F0.wireOp",EDGE,"E80")])],"isStart":false})});}
            var sketch = newSketch(context, id + "F20", { "sketchPlane" : qUnion([Q0])});
            skLineSegment(sketch, "E421.bottom", {"start": v(-7300, 8680) * mm, "end": v(-150, 8680) * mm});
            skLineSegment(sketch, "E421.top", {"start": v(-7300, 150) * mm, "end": v(-150, 150) * mm});
            skLineSegment(sketch, "E421.left", {"start": v(-7300, 8680) * mm, "end": v(-7300, 150) * mm});
            skLineSegment(sketch, "E421.right", {"start": v(-150, 8680) * mm, "end": v(-150, 150) * mm});
            skLineSegment(sketch, "E422.bottom", {"start": v(-2750, 2350) * mm, "end": v(-3750, 2350) * mm});
            skLineSegment(sketch, "E422.top", {"start": v(-2750, 4850) * mm, "end": v(-3750, 4850) * mm});
            skLineSegment(sketch, "E422.left", {"start": v(-2750, 2350) * mm, "end": v(-2750, 4850) * mm});
            skLineSegment(sketch, "E422.right", {"start": v(-3750, 2350) * mm, "end": v(-3750, 4850) * mm});
            skSolve(sketch);
        }
        {
            var Q0;
            Q0 = qSketchRegion(id + "F20", true);
            extrude(context, id + "F21", {"entities" : qUnion([Q0]), "operationType" : NewBodyOperationType.ADD, "depth" : 200 * mm, "offsetDistance" : 25 * mm});
        }
        {
            var Q0;
            {var subQ0=sQuery(id+"F0.wireOp",EDGE,"E52");var subQ1=sQuery(id+"F0.wireOp",EDGE,"E7");var subQ2=sQuery(id+"F0.wireOp",EDGE,"E50.trimOffspring");var subQ3=sQuery(id+"F0.wireOp",EDGE,"E49");var subQ4=sQuery(id+"F0.wireOp",EDGE,"E48");var subQ5=sQuery(id+"F0.wireOp",EDGE,"E47");var subQ6=sQuery(id+"F0.wireOp",EDGE,"E46");var subQ7=sQuery(id+"F0.wireOp",EDGE,"E3");var subQ8=sQuery(id+"F0.wireOp",EDGE,"E41.trimOffspring");var subQ9=sQuery(id+"F0.wireOp",EDGE,"E39");var subQ10=sQuery(id+"F0.wireOp",EDGE,"E51.trimOffspring");var subQ11=sQuery(id+"F0.wireOp",EDGE,"E10");var subQ12=sQuery(id+"F0.wireOp",EDGE,"E21");var subQ13=sQuery(id+"F0.wireOp",EDGE,"E2");var subQ14=sQuery(id+"F0.wireOp",EDGE,"E11");var subQ15=sQuery(id+"F0.wireOp",EDGE,"E14");var subQ16=sQuery(id+"F0.wireOp",EDGE,"E36");var subQ17=sQuery(id+"F0.wireOp",EDGE,"E15");var subQ18=sQuery(id+"F0.wireOp",EDGE,"E37");var subQ19=sQuery(id+"F0.wireOp",EDGE,"E16");var subQ20=sQuery(id+"F0.wireOp",EDGE,"E17");var subQ21=sQuery(id+"F0.wireOp",EDGE,"E54.trimOffspring");var subQ22=sQuery(id+"F0.wireOp",EDGE,"E72");var subQ23=sQuery(id+"F0.wireOp",EDGE,"E73.trimOffspring");var subQ24=sQuery(id+"F0.wireOp",EDGE,"E74.trimOffspring");Q0=makeQuery(id+"F17.boolean.opBoolean","SPLIT",FACE,{"disambiguationData":[TD([makeQuery(id+"F1.opExtrude","SWEPT_FACE",FACE,{"disambiguationData":[OSD([subQ7])]})])],"derivedFrom":makeQuery(id+"F1.opExtrude","CAP_FACE",FACE,{"disambiguationData":[OSD([sQuery(id+"F0.wireOp",EDGE,"E0"),sQuery(id+"F0.wireOp",EDGE,"E1"),subQ13,subQ7,sQuery(id+"F0.wireOp",EDGE,"E6"),subQ1,sQuery(id+"F0.wireOp",EDGE,"E8"),sQuery(id+"F0.wireOp",EDGE,"E9"),subQ11,subQ14,sQuery(id+"F0.wireOp",EDGE,"E12"),sQuery(id+"F0.wireOp",EDGE,"E13"),subQ15,subQ17,subQ19,subQ20,sQuery(id+"F0.wireOp",EDGE,"E18"),sQuery(id+"F0.wireOp",EDGE,"E20"),subQ12,sQuery(id+"F0.wireOp",EDGE,"E22"),sQuery(id+"F0.wireOp",EDGE,"E25"),sQuery(id+"F0.wireOp",EDGE,"E32"),sQuery(id+"F0.wireOp",EDGE,"E33"),subQ16,subQ18,subQ9,subQ8,sQuery(id+"F0.wireOp",EDGE,"E42"),subQ6,subQ5,subQ4,subQ3,subQ2,subQ10,subQ0,sQuery(id+"F0.wireOp",EDGE,"E53"),subQ21,sQuery(id+"F0.wireOp",EDGE,"E55.trimOffspring"),sQuery(id+"F0.wireOp",EDGE,"E56"),sQuery(id+"F0.wireOp",EDGE,"E63"),sQuery(id+"F0.wireOp",EDGE,"E64.trimOffspring"),sQuery(id+"F0.wireOp",EDGE,"E65.trimOffspring"),sQuery(id+"F0.wireOp",EDGE,"E71"),subQ22,subQ23,subQ24,sQuery(id+"F0.wireOp",EDGE,"E75"),sQuery(id+"F0.wireOp",EDGE,"E77.trimOffspring")])],"isStart":true})});}
            var sketch = newSketch(context, id + "F22", { "sketchPlane" : qUnion([Q0])});
            skLineSegment(sketch, "E423", {"start": v(-7450, 3070) * mm, "end": v(-7450, -8780) * mm});
            skLineSegment(sketch, "E424", {"start": v(-7450, -8780) * mm, "end": v(2000, -8780) * mm});
            skLineSegment(sketch, "E425", {"start": v(2000, -8780) * mm, "end": v(2000, 0) * mm});
            skLineSegment(sketch, "E426", {"start": v(2000, 0) * mm, "end": v(-1150, 0) * mm});
            skLineSegment(sketch, "E427", {"start": v(-2750, 1600) * mm, "end": v(-2750, 3070) * mm});
            skLineSegment(sketch, "E428", {"start": v(-2750, 3070) * mm, "end": v(-7450, 3070) * mm});
            skLineSegment(sketch, "E429.top", {"start": v(-2750, 1600) * mm, "end": v(-1150, 1600) * mm});
            skLineSegment(sketch, "E429.right", {"start": v(-1150, 0) * mm, "end": v(-1150, 1600) * mm});
            skPoint(sketch, "E430.orphan", {"position": v(-2750, 0) * mm});
            skSolve(sketch);
        }
        {
            var Q0;
            Q0 = qSketchRegion(id + "F22", true);
            extrude(context, id + "F23", {"entities" : qUnion([Q0]), "operationType" : NewBodyOperationType.ADD, "oppositeDirection" : true, "depth" : 300 * mm, "offsetDistance" : 25 * mm});
        }
        {
            var Q0;
            Q0=makeQuery(id+"F23.opExtrude","SWEPT_FACE",FACE,{"disambiguationData":[OSD([sQuery(id+"F22.wireOp",EDGE,"E429.top")])]});
            var sketch = newSketch(context, id + "F24", { "sketchPlane" : qUnion([Q0])});
            skLineSegment(sketch, "E431.bottom", {"start": v(-2200, 300) * mm, "end": v(-1400, 300) * mm});
            skLineSegment(sketch, "E431.top", {"start": v(-2200, 2400) * mm, "end": v(-1400, 2400) * mm});
            skLineSegment(sketch, "E431.left", {"start": v(-2200, 300) * mm, "end": v(-2200, 2400) * mm});
            skLineSegment(sketch, "E431.right", {"start": v(-1400, 300) * mm, "end": v(-1400, 2400) * mm});
            skLineSegment(sketch, "E432.bottom", {"start": v(-2100, 2300) * mm, "end": v(-1875, 2300) * mm});
            skLineSegment(sketch, "E432.top", {"start": v(-2100, 2000) * mm, "end": v(-1875, 2000) * mm});
            skLineSegment(sketch, "E432.left", {"start": v(-2100, 2300) * mm, "end": v(-2100, 2000) * mm});
            skLineSegment(sketch, "E432.right", {"start": v(-1875, 2300) * mm, "end": v(-1875, 2000) * mm});
            skLineSegment(sketch, "E433.bottom", {"start": v(-1725, 2300) * mm, "end": v(-1500, 2300) * mm});
            skLineSegment(sketch, "E433.top", {"start": v(-1725, 2000) * mm, "end": v(-1500, 2000) * mm});
            skLineSegment(sketch, "E433.left", {"start": v(-1725, 2300) * mm, "end": v(-1725, 2000) * mm});
            skLineSegment(sketch, "E433.right", {"start": v(-1500, 2300) * mm, "end": v(-1500, 2000) * mm});
            skLineSegment(sketch, "E434.bottom", {"start": v(-2100, 1900) * mm, "end": v(-1875, 1900) * mm});
            skLineSegment(sketch, "E434.top", {"start": v(-2100, 1200) * mm, "end": v(-1875, 1200) * mm});
            skLineSegment(sketch, "E434.left", {"start": v(-2100, 1900) * mm, "end": v(-2100, 1200) * mm});
            skLineSegment(sketch, "E434.right", {"start": v(-1875, 1900) * mm, "end": v(-1875, 1200) * mm});
            skLineSegment(sketch, "E435.bottom", {"start": v(-1725, 1900) * mm, "end": v(-1500, 1900) * mm});
            skLineSegment(sketch, "E435.top", {"start": v(-1725, 1200) * mm, "end": v(-1500, 1200) * mm});
            skLineSegment(sketch, "E435.left", {"start": v(-1725, 1900) * mm, "end": v(-1725, 1200) * mm});
            skLineSegment(sketch, "E435.right", {"start": v(-1500, 1900) * mm, "end": v(-1500, 1200) * mm});
            skLineSegment(sketch, "E436.bottom", {"start": v(-2100, 1100) * mm, "end": v(-1875, 1100) * mm});
            skLineSegment(sketch, "E436.top", {"start": v(-2100, 400) * mm, "end": v(-1875, 400) * mm});
            skLineSegment(sketch, "E436.left", {"start": v(-2100, 1100) * mm, "end": v(-2100, 400) * mm});
            skLineSegment(sketch, "E436.right", {"start": v(-1875, 1100) * mm, "end": v(-1875, 400) * mm});
            skLineSegment(sketch, "E437.bottom", {"start": v(-1725, 1100) * mm, "end": v(-1500, 1100) * mm});
            skLineSegment(sketch, "E437.top", {"start": v(-1725, 400) * mm, "end": v(-1500, 400) * mm});
            skLineSegment(sketch, "E437.left", {"start": v(-1725, 1100) * mm, "end": v(-1725, 400) * mm});
            skLineSegment(sketch, "E437.right", {"start": v(-1500, 1100) * mm, "end": v(-1500, 400) * mm});
            skLineSegment(sketch, "E438.bottom", {"start": v(-2650, 2400) * mm, "end": v(-2300, 2400) * mm});
            skLineSegment(sketch, "E438.top", {"start": v(-2650, 300) * mm, "end": v(-2300, 300) * mm});
            skLineSegment(sketch, "E438.left", {"start": v(-2650, 2400) * mm, "end": v(-2650, 300) * mm});
            skLineSegment(sketch, "E438.right", {"start": v(-2300, 2400) * mm, "end": v(-2300, 300) * mm});
            skLineSegment(sketch, "E439.bottom", {"start": v(-1300, 2400) * mm, "end": v(-950, 2400) * mm});
            skLineSegment(sketch, "E439.top", {"start": v(-1300, 300) * mm, "end": v(-950, 300) * mm});
            skLineSegment(sketch, "E439.left", {"start": v(-1300, 2400) * mm, "end": v(-1300, 300) * mm});
            skLineSegment(sketch, "E439.right", {"start": v(-950, 2400) * mm, "end": v(-950, 300) * mm});
            skLineSegment(sketch, "E440.bottom", {"start": v(-2550, 2300) * mm, "end": v(-2400, 2300) * mm});
            skLineSegment(sketch, "E440.top", {"start": v(-2550, 400) * mm, "end": v(-2400, 400) * mm});
            skLineSegment(sketch, "E440.left", {"start": v(-2550, 2300) * mm, "end": v(-2550, 400) * mm});
            skLineSegment(sketch, "E440.right", {"start": v(-2400, 2300) * mm, "end": v(-2400, 400) * mm});
            skLineSegment(sketch, "E441.bottom", {"start": v(-1200, 2300) * mm, "end": v(-1050, 2300) * mm});
            skLineSegment(sketch, "E441.top", {"start": v(-1200, 400) * mm, "end": v(-1050, 400) * mm});
            skLineSegment(sketch, "E441.left", {"start": v(-1200, 2300) * mm, "end": v(-1200, 400) * mm});
            skLineSegment(sketch, "E441.right", {"start": v(-1050, 2300) * mm, "end": v(-1050, 400) * mm});
            skSolve(sketch);
        }
        {
            var Q0;
            Q0 = qSketchRegion(id + "F24", true);
            extrude(context, id + "F25", {"entities" : qUnion([Q0]), "operationType" : NewBodyOperationType.ADD, "depth" : 25 * mm, "offsetDistance" : 25 * mm});
        }
        {
            var Q0;
            Q0=qCreatedBy(makeId("Top.planeOp"),FACE);
            var sketch = newSketch(context, id + "F26", { "sketchPlane" : qUnion([Q0])});
            skLineSegment(sketch, "E442.bottom", {"start": v(-950, -2200) * mm, "end": v(-750, -2200) * mm});
            skLineSegment(sketch, "E442.top", {"start": v(-950, -2000) * mm, "end": v(-750, -2000) * mm});
            skLineSegment(sketch, "E442.left", {"start": v(-950, -2200) * mm, "end": v(-950, -2000) * mm});
            skLineSegment(sketch, "E442.right", {"start": v(-750, -2200) * mm, "end": v(-750, -2000) * mm});
            skSolve(sketch);
        }
        {
            var Q0;
            Q0 = qSketchRegion(id + "F26", true);
            var Q1;
            {var subQ0=sQuery(id+"F0.wireOp",EDGE,"E2");var subQ69=sQuery(id+"F4.wireOp",EDGE,"E87");Q1=makeQuery(id+"F7.boolean.opBoolean","MERGE",FACE,{"derivedFrom":[makeQuery(id+"F5.boolean.opBoolean","SPLIT",FACE,{"disambiguationData":[TD([makeQuery(id+"F1.opExtrude","SWEPT_FACE",FACE,{"disambiguationData":[OSD([subQ0])]})])],"derivedFrom":makeQuery(id+"F5.opExtrude","SWEPT_FACE",FACE,{"disambiguationData":[OSD([subQ69])]})}),makeQuery(id+"F7.opExtrude","SWEPT_FACE",FACE,{"disambiguationData":[OSD([sQuery(id+"F6.wireOp",EDGE,"E155")])]})]});}
            extrude(context, id + "F27", {"entities" : qUnion([Q0]), "endBound" : BoundingType.UP_TO_SURFACE, "depth" : 2600 * mm, "endBoundEntityFace" : qUnion([Q1]), "offsetDistance" : 25 * mm});
        }
        {
            var Q0;
            Q0=makeQuery(id+"F27.opExtrude","SWEPT_FACE",FACE,{"disambiguationData":[OSD([sQuery(id+"F26.wireOp",EDGE,"E442.right")])]});
            var sketch = newSketch(context, id + "F28", { "sketchPlane" : qUnion([Q0])});
            skLineSegment(sketch, "E443", {"start": v(0, 2500) * mm, "end": v(-2400, 2500) * mm});
            skLineSegment(sketch, "E444", {"start": v(-2400, 2500) * mm, "end": v(-2400, 2523.69) * mm});
            skLineSegment(sketch, "E445", {"start": v(-2400, 2523.69) * mm, "end": v(-2193.37, 2575.2) * mm});
            skLineSegment(sketch, "E446", {"start": v(-2193.37, 2575.2) * mm, "end": v(-2193.37, 2598.9) * mm});
            skLineSegment(sketch, "E447", {"start": v(-2193.37, 2598.9) * mm, "end": v(-1986.74, 2650.42) * mm});
            skLineSegment(sketch, "E448", {"start": v(-1986.74, 2650.42) * mm, "end": v(-1986.74, 2674.1) * mm});
            skLineSegment(sketch, "E449", {"start": v(-1986.74, 2674.1) * mm, "end": v(-1780.1, 2725.62) * mm});
            skLineSegment(sketch, "E450", {"start": v(-1780.1, 2725.62) * mm, "end": v(-1780.1, 2749.31) * mm});
            skLineSegment(sketch, "E451", {"start": v(-1780.1, 2749.31) * mm, "end": v(-1573.47, 2800.83) * mm});
            skLineSegment(sketch, "E452", {"start": v(-1573.47, 2800.83) * mm, "end": v(-1573.47, 2824.52) * mm});
            skLineSegment(sketch, "E453", {"start": v(-1573.47, 2824.52) * mm, "end": v(-1366.84, 2876.04) * mm});
            skLineSegment(sketch, "E454", {"start": v(-2400, 2500) * mm, "end": v(0, 3373.53) * mm, "construction": true});
            skLineSegment(sketch, "E455", {"start": v(-1366.84, 2876.04) * mm, "end": v(-1366.84, 2899.73) * mm});
            skLineSegment(sketch, "E456", {"start": v(-1366.84, 2899.73) * mm, "end": v(-1160.2, 2951.25) * mm});
            skLineSegment(sketch, "E457", {"start": v(-1160.2, 2951.25) * mm, "end": v(-1160.2, 2974.94) * mm});
            skLineSegment(sketch, "E458", {"start": v(0, 3373.53) * mm, "end": v(0, 2500) * mm});
            skLineSegment(sketch, "E459.bottom", {"start": v(0, 0) * mm, "end": v(-2400, 0) * mm});
            skLineSegment(sketch, "E459.top", {"start": v(-1600, 150) * mm, "end": v(-2400, 150) * mm});
            skLineSegment(sketch, "E459.left", {"start": v(0, 0) * mm, "end": v(0, 150) * mm});
            skLineSegment(sketch, "E459.right", {"start": v(-2400, 0) * mm, "end": v(-2400, 150) * mm});
            skLineSegment(sketch, "E460", {"start": v(0, 150) * mm, "end": v(0, 300) * mm});
            skLineSegment(sketch, "E461", {"start": v(0, 300) * mm, "end": v(-1600, 300) * mm});
            skLineSegment(sketch, "E462", {"start": v(-1600, 300) * mm, "end": v(-1600, 150) * mm});
            skLineSegment(sketch, "E463", {"start": v(-1160.2, 2974.94) * mm, "end": v(-953.57, 3026.46) * mm});
            skLineSegment(sketch, "E464", {"start": v(-953.57, 3026.46) * mm, "end": v(-953.57, 3050.14) * mm});
            skLineSegment(sketch, "E465", {"start": v(-953.57, 3050.14) * mm, "end": v(-746.94, 3101.66) * mm});
            skLineSegment(sketch, "E466", {"start": v(-746.94, 3101.66) * mm, "end": v(-746.94, 3125.35) * mm});
            skLineSegment(sketch, "E467", {"start": v(-746.94, 3125.35) * mm, "end": v(-540.3, 3176.87) * mm});
            skLineSegment(sketch, "E468", {"start": v(-540.3, 3176.87) * mm, "end": v(-540.3, 3200.56) * mm});
            skLineSegment(sketch, "E469", {"start": v(-540.3, 3200.56) * mm, "end": v(-333.68, 3252.08) * mm});
            skLineSegment(sketch, "E470", {"start": v(-333.68, 3252.08) * mm, "end": v(-333.68, 3275.77) * mm});
            skLineSegment(sketch, "E471", {"start": v(-333.68, 3275.77) * mm, "end": v(-127.04, 3327.29) * mm});
            skLineSegment(sketch, "E472", {"start": v(-127.04, 3327.29) * mm, "end": v(-127.04, 3350.98) * mm});
            skLineSegment(sketch, "E473", {"start": v(-127.04, 3350.98) * mm, "end": v(0, 3382.65) * mm});
            skLineSegment(sketch, "E474", {"start": v(0, 3382.65) * mm, "end": v(0, 3373.53) * mm});
            skSolve(sketch);
        }
        {
            var Q0;
            Q0 = qSketchRegion(id + "F28", true);
            extrude(context, id + "F29", {"entities" : qUnion([Q0]), "operationType" : NewBodyOperationType.ADD, "endBound" : BoundingType.UP_TO_NEXT, "oppositeDirection" : true, "depth" : 25 * mm, "offsetDistance" : 25 * mm, "hasSecondDirection" : true, "secondDirectionOppositeDirection" : false, "secondDirectionDepth" : 200 * mm});
        }
        {
            var Q0;
            Q0=makeQuery(id+"F23.opExtrude","CAP_FACE",FACE,{"disambiguationData":[OSD([sQuery(id+"F22.wireOp",EDGE,"E423"),sQuery(id+"F22.wireOp",EDGE,"E424"),sQuery(id+"F22.wireOp",EDGE,"E425"),sQuery(id+"F22.wireOp",EDGE,"E426"),sQuery(id+"F22.wireOp",EDGE,"E427"),sQuery(id+"F22.wireOp",EDGE,"E428")])],"isStart":false});
            var sketch = newSketch(context, id + "F30", { "sketchPlane" : qUnion([Q0])});
            skLineSegment(sketch, "E475.bottom", {"start": v(-250, 250) * mm, "end": v(0, 250) * mm});
            skLineSegment(sketch, "E475.top", {"start": v(-250, 3000) * mm, "end": v(0, 3000) * mm});
            skLineSegment(sketch, "E475.left", {"start": v(-250, 250) * mm, "end": v(-250, 3000) * mm});
            skLineSegment(sketch, "E475.right", {"start": v(0, 250) * mm, "end": v(0, 3000) * mm});
            skLineSegment(sketch, "E476.bottom", {"start": v(-2650, 4500) * mm, "end": v(-250, 4500) * mm});
            skLineSegment(sketch, "E476.top", {"start": v(-2650, 4600) * mm, "end": v(-250, 4600) * mm});
            skLineSegment(sketch, "E476.left", {"start": v(-2650, 4500) * mm, "end": v(-2650, 4600) * mm});
            skLineSegment(sketch, "E476.right", {"start": v(-250, 4500) * mm, "end": v(-250, 4600) * mm});
            skLineSegment(sketch, "E477.bottom", {"start": v(-250, 3800) * mm, "end": v(0, 3800) * mm});
            skLineSegment(sketch, "E477.top", {"start": v(-250, 4400) * mm, "end": v(0, 4400) * mm});
            skLineSegment(sketch, "E477.left", {"start": v(-250, 3800) * mm, "end": v(-250, 4400) * mm});
            skLineSegment(sketch, "E477.right", {"start": v(0, 3800) * mm, "end": v(0, 4400) * mm});
            skLineSegment(sketch, "E478.bottom", {"start": v(-3132.03, 0) * mm, "end": v(-2694.66, 0) * mm});
            skLineSegment(sketch, "E478.top", {"start": v(-3132.03, -1503.3) * mm, "end": v(-2694.66, -1503.3) * mm});
            skLineSegment(sketch, "E478.left", {"start": v(-3132.03, 0) * mm, "end": v(-3132.03, -1503.3) * mm});
            skLineSegment(sketch, "E478.right", {"start": v(-2694.66, 0) * mm, "end": v(-2694.66, -1503.3) * mm});
            skSolve(sketch);
        }
        {
            var Q0;
            Q0 = qSketchRegion(id + "F30", true);
            var Q1;
            {var subQ9=sQuery(id+"F0.wireOp",EDGE,"E55.trimOffspring");var subQ13=sQuery(id+"F0.wireOp",EDGE,"E5");var subQ14=sQuery(id+"F2.wireOp",EDGE,"E83.top");var subQ15=sQuery(id+"F2.wireOp",EDGE,"E84.top");var subQ16=sQuery(id+"F2.wireOp",EDGE,"E84.right");var subQ17=sQuery(id+"F2.wireOp",EDGE,"E83.right");var subQ18=makeQuery(id+"F3.opExtrude","CAP_FACE",FACE,{"disambiguationData":[OSD([sQuery(id+"F2.wireOp",EDGE,"E83.bottom"),subQ14,sQuery(id+"F2.wireOp",EDGE,"E83.left"),subQ17,sQuery(id+"F2.wireOp",EDGE,"E84.bottom"),subQ15,sQuery(id+"F2.wireOp",EDGE,"E84.left"),subQ16])],"isStart":true});Q1=makeQuery(id+"F21.boolean.opBoolean","MERGE",FACE,{"derivedFrom":[makeQuery(id+"F3.boolean.opBoolean","SPLIT",FACE,{"disambiguationData":[TD([makeQuery(id+"F1.opExtrude","SWEPT_FACE",FACE,{"disambiguationData":[OSD([subQ13])]})])],"derivedFrom":subQ18}),makeQuery(id+"F3.boolean.opBoolean","SPLIT",FACE,{"disambiguationData":[TD([makeQuery(id+"F1.opExtrude","SWEPT_FACE",FACE,{"disambiguationData":[OSD([subQ9])]})])],"derivedFrom":subQ18}),makeQuery(id+"F21.opExtrude","CAP_FACE",FACE,{"disambiguationData":[OSD([sQuery(id+"F20.wireOp",EDGE,"E421.bottom"),sQuery(id+"F20.wireOp",EDGE,"E421.top"),sQuery(id+"F20.wireOp",EDGE,"E421.left"),sQuery(id+"F20.wireOp",EDGE,"E421.right"),sQuery(id+"F20.wireOp",EDGE,"E422.bottom"),sQuery(id+"F20.wireOp",EDGE,"E422.top"),sQuery(id+"F20.wireOp",EDGE,"E422.left"),sQuery(id+"F20.wireOp",EDGE,"E422.right")])],"isStart":true})]});}
            extrude(context, id + "F31", {"entities" : qUnion([Q0]), "operationType" : NewBodyOperationType.REMOVE, "endBound" : BoundingType.UP_TO_SURFACE, "depth" : 25 * mm, "endBoundEntityFace" : qUnion([Q1]), "offsetDistance" : 25 * mm});
        }
        {
            var Q0;
            Q0=makeQuery(id+"F31.boolean.opBoolean","MERGE",FACE,{"derivedFrom":[makeQuery(id+"F23.opExtrude","CAP_FACE",FACE,{"disambiguationData":[OSD([sQuery(id+"F22.wireOp",EDGE,"E423"),sQuery(id+"F22.wireOp",EDGE,"E424"),sQuery(id+"F22.wireOp",EDGE,"E425"),sQuery(id+"F22.wireOp",EDGE,"E426"),sQuery(id+"F22.wireOp",EDGE,"E427"),sQuery(id+"F22.wireOp",EDGE,"E428")])],"isStart":false})],"fromTools":[makeQuery(id+"F31.opExtrude","CAP_FACE",FACE,{"disambiguationData":[OSD([sQuery(id+"F30.wireOp",EDGE,"E475.bottom"),sQuery(id+"F30.wireOp",EDGE,"E475.top"),sQuery(id+"F30.wireOp",EDGE,"E475.left"),sQuery(id+"F30.wireOp",EDGE,"E475.right")])],"isStart":true}),makeQuery(id+"F31.opExtrude","CAP_FACE",FACE,{"disambiguationData":[OSD([sQuery(id+"F30.wireOp",EDGE,"E476.bottom"),sQuery(id+"F30.wireOp",EDGE,"E476.top"),sQuery(id+"F30.wireOp",EDGE,"E476.left"),sQuery(id+"F30.wireOp",EDGE,"E476.right")])],"isStart":true})]});
            var sketch = newSketch(context, id + "F32", { "sketchPlane" : qUnion([Q0])});
            skLineSegment(sketch, "E479.bottom", {"start": v(-950, 250) * mm, "end": v(-850, 250) * mm, "construction": true});
            skLineSegment(sketch, "E479.top", {"start": v(-950, 1750) * mm, "end": v(-850, 1750) * mm, "construction": true});
            skLineSegment(sketch, "E479.left", {"start": v(-950, 250) * mm, "end": v(-950, 1750) * mm, "construction": true});
            skLineSegment(sketch, "E479.right", {"start": v(-850, 250) * mm, "end": v(-850, 1750) * mm, "construction": true});
            skPoint(sketch, "E480.firstSnap0", {"position": v(-2750, 1750) * mm});
            skLineSegment(sketch, "E480.bottom", {"start": v(-2650, 1750) * mm, "end": v(-1700, 1750) * mm, "construction": true});
            skLineSegment(sketch, "E480.top", {"start": v(-2650, 1650) * mm, "end": v(-1700, 1650) * mm, "construction": true});
            skLineSegment(sketch, "E480.left", {"start": v(-2650, 1750) * mm, "end": v(-2650, 1650) * mm, "construction": true});
            skLineSegment(sketch, "E480.right", {"start": v(-1700, 1750) * mm, "end": v(-1700, 1650) * mm, "construction": true});
            skLineSegment(sketch, "E481.bottom", {"start": v(0, 4400) * mm, "end": v(250, 4400) * mm});
            skLineSegment(sketch, "E481.top", {"start": v(0, 4500) * mm, "end": v(250, 4500) * mm});
            skLineSegment(sketch, "E481.left", {"start": v(0, 4400) * mm, "end": v(0, 4500) * mm});
            skLineSegment(sketch, "E481.right", {"start": v(250, 4400) * mm, "end": v(250, 4500) * mm});
            skLineSegment(sketch, "E482.bottom", {"start": v(1750, 4400) * mm, "end": v(1050, 4400) * mm});
            skLineSegment(sketch, "E482.top", {"start": v(1750, 4500) * mm, "end": v(1050, 4500) * mm});
            skLineSegment(sketch, "E482.left", {"start": v(1750, 4400) * mm, "end": v(1750, 4500) * mm});
            skLineSegment(sketch, "E482.right", {"start": v(1050, 4400) * mm, "end": v(1050, 4500) * mm});
            skLineSegment(sketch, "E483.bottom", {"start": v(-550, -1600) * mm, "end": v(-3000, -1600) * mm});
            skLineSegment(sketch, "E483.right", {"start": v(-3000, -1600) * mm, "end": v(-3000, -1350) * mm});
            skLineSegment(sketch, "E484.top", {"start": v(-550, 0) * mm, "end": v(-800, 0) * mm});
            skLineSegment(sketch, "E484.left", {"start": v(-550, -1600) * mm, "end": v(-550, 0) * mm});
            skLineSegment(sketch, "E484.right", {"start": v(-800, -1350) * mm, "end": v(-800, 0) * mm});
            skLineSegment(sketch, "E485", {"start": v(-3000, -1350) * mm, "end": v(-800, -1350) * mm});
            skSolve(sketch);
        }
        {
            var Q0;
            Q0 = qSketchRegion(id + "F32", true);
            var Q1;
            {var subQ9=sQuery(id+"F0.wireOp",EDGE,"E55.trimOffspring");var subQ13=sQuery(id+"F0.wireOp",EDGE,"E5");var subQ14=sQuery(id+"F2.wireOp",EDGE,"E83.top");var subQ15=sQuery(id+"F2.wireOp",EDGE,"E84.top");var subQ16=sQuery(id+"F2.wireOp",EDGE,"E84.right");var subQ17=sQuery(id+"F2.wireOp",EDGE,"E83.right");var subQ18=makeQuery(id+"F3.opExtrude","CAP_FACE",FACE,{"disambiguationData":[OSD([sQuery(id+"F2.wireOp",EDGE,"E83.bottom"),subQ14,sQuery(id+"F2.wireOp",EDGE,"E83.left"),subQ17,sQuery(id+"F2.wireOp",EDGE,"E84.bottom"),subQ15,sQuery(id+"F2.wireOp",EDGE,"E84.left"),subQ16])],"isStart":true});Q1=makeQuery(id+"F31.boolean.opBoolean","MERGE",FACE,{"derivedFrom":[makeQuery(id+"F21.boolean.opBoolean","MERGE",FACE,{"derivedFrom":[makeQuery(id+"F3.boolean.opBoolean","SPLIT",FACE,{"disambiguationData":[TD([makeQuery(id+"F1.opExtrude","SWEPT_FACE",FACE,{"disambiguationData":[OSD([subQ13])]})])],"derivedFrom":subQ18}),makeQuery(id+"F3.boolean.opBoolean","SPLIT",FACE,{"disambiguationData":[TD([makeQuery(id+"F1.opExtrude","SWEPT_FACE",FACE,{"disambiguationData":[OSD([subQ9])]})])],"derivedFrom":subQ18}),makeQuery(id+"F21.opExtrude","CAP_FACE",FACE,{"disambiguationData":[OSD([sQuery(id+"F20.wireOp",EDGE,"E421.bottom"),sQuery(id+"F20.wireOp",EDGE,"E421.top"),sQuery(id+"F20.wireOp",EDGE,"E421.left"),sQuery(id+"F20.wireOp",EDGE,"E421.right"),sQuery(id+"F20.wireOp",EDGE,"E422.bottom"),sQuery(id+"F20.wireOp",EDGE,"E422.top"),sQuery(id+"F20.wireOp",EDGE,"E422.left"),sQuery(id+"F20.wireOp",EDGE,"E422.right")])],"isStart":true})]}),makeQuery(id+"F29.opExtrude","SWEPT_FACE",FACE,{"disambiguationData":[OSD([sQuery(id+"F28.wireOp",EDGE,"E443")])]})],"fromTools":[makeQuery(id+"F31.opExtrude","CAP_FACE",FACE,{"disambiguationData":[OSD([sQuery(id+"F30.wireOp",EDGE,"E475.bottom"),sQuery(id+"F30.wireOp",EDGE,"E475.top"),sQuery(id+"F30.wireOp",EDGE,"E475.left"),sQuery(id+"F30.wireOp",EDGE,"E475.right")])],"isStart":false}),makeQuery(id+"F31.opExtrude","CAP_FACE",FACE,{"disambiguationData":[OSD([sQuery(id+"F30.wireOp",EDGE,"E476.bottom"),sQuery(id+"F30.wireOp",EDGE,"E476.top"),sQuery(id+"F30.wireOp",EDGE,"E476.left"),sQuery(id+"F30.wireOp",EDGE,"E476.right")])],"isStart":false}),makeQuery(id+"F31.opExtrude","CAP_FACE",FACE,{"disambiguationData":[OSD([sQuery(id+"F30.wireOp",EDGE,"E477.bottom"),sQuery(id+"F30.wireOp",EDGE,"E477.top"),sQuery(id+"F30.wireOp",EDGE,"E477.left"),sQuery(id+"F30.wireOp",EDGE,"E477.right")])],"isStart":false}),makeQuery(id+"F31.opExtrude","CAP_FACE",FACE,{"disambiguationData":[OSD([sQuery(id+"F30.wireOp",EDGE,"E478.bottom"),sQuery(id+"F30.wireOp",EDGE,"E478.top"),sQuery(id+"F30.wireOp",EDGE,"E478.left"),sQuery(id+"F30.wireOp",EDGE,"E478.right")])],"isStart":false})]});}
            extrude(context, id + "F33", {"entities" : qUnion([Q0]), "operationType" : NewBodyOperationType.ADD, "endBound" : BoundingType.UP_TO_SURFACE, "depth" : 25 * mm, "endBoundEntityFace" : qUnion([Q1]), "offsetDistance" : 25 * mm});
        }
        {
            var Q0;
            {var subQ97=sQuery(id+"F10.wireOp",EDGE,"E266.top");var subQ196=sQuery(id+"F0.wireOp",EDGE,"E6");var subQ197=sQuery(id+"F0.wireOp",EDGE,"E5");Q0=makeQuery(id+"F19.boolean.opBoolean","SPLIT",FACE,{"disambiguationData":[TD([makeQuery(id+"F1.opExtrude","SWEPT_FACE",FACE,{"disambiguationData":[OSD([subQ197])]})])],"derivedFrom":makeQuery(id+"F11.boolean.opBoolean","MERGE",FACE,{"derivedFrom":[makeQuery(id+"F3.boolean.opBoolean","MERGE",FACE,{"derivedFrom":[makeQuery(id+"F1.opExtrude","SWEPT_FACE",FACE,{"disambiguationData":[OSD([subQ196])]}),makeQuery(id+"F3.opExtrude","SWEPT_FACE",FACE,{"disambiguationData":[OSD([sQuery(id+"F2.wireOp",EDGE,"E83.bottom")])]})]}),makeQuery(id+"F11.opExtrude","SWEPT_FACE",FACE,{"disambiguationData":[OSD([subQ97])]})]})});}
            var sketch = newSketch(context, id + "F34", { "sketchPlane" : qUnion([Q0])});
            skLineSegment(sketch, "E486.bottom", {"start": v(-1450, 300) * mm, "end": v(-550, 300) * mm});
            skLineSegment(sketch, "E486.top", {"start": v(-1450, 2400) * mm, "end": v(-550, 2400) * mm});
            skLineSegment(sketch, "E486.left", {"start": v(-1450, 300) * mm, "end": v(-1450, 2400) * mm});
            skLineSegment(sketch, "E486.right", {"start": v(-550, 300) * mm, "end": v(-550, 2400) * mm});
            skLineSegment(sketch, "E487.bottom", {"start": v(-1350, 2300) * mm, "end": v(-650, 2300) * mm});
            skLineSegment(sketch, "E487.top", {"start": v(-1350, 1100) * mm, "end": v(-650, 1100) * mm});
            skLineSegment(sketch, "E487.left", {"start": v(-1350, 2300) * mm, "end": v(-1350, 1100) * mm});
            skLineSegment(sketch, "E487.right", {"start": v(-650, 2300) * mm, "end": v(-650, 1100) * mm});
            skSolve(sketch);
        }
        {
            var Q0;
            Q0 = qSketchRegion(id + "F34", true);
            extrude(context, id + "F35", {"entities" : qUnion([Q0]), "operationType" : NewBodyOperationType.ADD, "depth" : 25 * mm, "offsetDistance" : 25 * mm});
        }
        {
            var Q0;
            Q0=makeQuery(id+"F7.boolean.opBoolean","MERGE",FACE,{"derivedFrom":[makeQuery(id+"F1.opExtrude","SWEPT_FACE",FACE,{"disambiguationData":[OSD([sQuery(id+"F0.wireOp",EDGE,"E3"),sQuery(id+"F0.wireOp",EDGE,"E40.trimOffspring"),sQuery(id+"F0.wireOp",EDGE,"E80")])]}),makeQuery(id+"F7.opExtrude","CAP_FACE",FACE,{"disambiguationData":[OSD([sQuery(id+"F6.wireOp",EDGE,"E153"),sQuery(id+"F6.wireOp",EDGE,"E155"),sQuery(id+"F6.wireOp",EDGE,"E156"),sQuery(id+"F6.wireOp",EDGE,"E157"),sQuery(id+"F6.wireOp",EDGE,"E158"),sQuery(id+"F6.wireOp",EDGE,"E159.0"),sQuery(id+"F6.wireOp",EDGE,"E160.0"),sQuery(id+"F6.wireOp",EDGE,"E160.1"),sQuery(id+"F6.wireOp",EDGE,"E160.2"),sQuery(id+"F6.wireOp",EDGE,"E160.3"),sQuery(id+"F6.wireOp",EDGE,"E160.4"),sQuery(id+"F6.wireOp",EDGE,"E161.0"),sQuery(id+"F6.wireOp",EDGE,"E161.1"),sQuery(id+"F6.wireOp",EDGE,"E161.2"),sQuery(id+"F6.wireOp",EDGE,"E161.3"),sQuery(id+"F6.wireOp",EDGE,"E162.0"),sQuery(id+"F6.wireOp",EDGE,"E162.1"),sQuery(id+"F6.wireOp",EDGE,"E162.2"),sQuery(id+"F6.wireOp",EDGE,"E162.3"),sQuery(id+"F6.wireOp",EDGE,"E163.0"),sQuery(id+"F6.wireOp",EDGE,"E163.1"),sQuery(id+"F6.wireOp",EDGE,"E163.2"),sQuery(id+"F6.wireOp",EDGE,"E163.3"),sQuery(id+"F6.wireOp",EDGE,"E164.0"),sQuery(id+"F6.wireOp",EDGE,"E164.1"),sQuery(id+"F6.wireOp",EDGE,"E164.2"),sQuery(id+"F6.wireOp",EDGE,"E164.3"),sQuery(id+"F6.wireOp",EDGE,"E164.4"),sQuery(id+"F6.wireOp",EDGE,"E164.5"),sQuery(id+"F6.wireOp",EDGE,"E164.6"),sQuery(id+"F6.wireOp",EDGE,"E165.0"),sQuery(id+"F6.wireOp",EDGE,"E165.1"),sQuery(id+"F6.wireOp",EDGE,"E165.2"),sQuery(id+"F6.wireOp",EDGE,"E165.3"),sQuery(id+"F6.wireOp",EDGE,"E165.4"),sQuery(id+"F6.wireOp",EDGE,"E165.5"),sQuery(id+"F6.wireOp",EDGE,"E165.6")])],"isStart":false})]});
            var sketch = newSketch(context, id + "F36", { "sketchPlane" : qUnion([Q0])});
            skLineSegment(sketch, "E488.bottom", {"start": v(-2320, 2200) * mm, "end": v(-1720, 2200) * mm});
            skLineSegment(sketch, "E488.top", {"start": v(-2320, 1200) * mm, "end": v(-1720, 1200) * mm});
            skLineSegment(sketch, "E488.left", {"start": v(-2320, 2200) * mm, "end": v(-2320, 1200) * mm});
            skLineSegment(sketch, "E488.right", {"start": v(-1720, 2200) * mm, "end": v(-1720, 1200) * mm});
            skLineSegment(sketch, "E489.bottom", {"start": v(-2220, 2100) * mm, "end": v(-1820, 2100) * mm});
            skLineSegment(sketch, "E489.top", {"start": v(-2220, 1900) * mm, "end": v(-1820, 1900) * mm});
            skLineSegment(sketch, "E489.left", {"start": v(-2220, 2100) * mm, "end": v(-2220, 1900) * mm});
            skLineSegment(sketch, "E489.right", {"start": v(-1820, 2100) * mm, "end": v(-1820, 1900) * mm});
            skLineSegment(sketch, "E490.bottom", {"start": v(-2220, 1800) * mm, "end": v(-1820, 1800) * mm});
            skLineSegment(sketch, "E490.top", {"start": v(-2220, 1300) * mm, "end": v(-1820, 1300) * mm});
            skLineSegment(sketch, "E490.left", {"start": v(-2220, 1800) * mm, "end": v(-2220, 1300) * mm});
            skLineSegment(sketch, "E490.right", {"start": v(-1820, 1800) * mm, "end": v(-1820, 1300) * mm});
            skSolve(sketch);
        }
        {
            var Q0;
            Q0 = qSketchRegion(id + "F36", true);
            extrude(context, id + "F37", {"entities" : qUnion([Q0]), "operationType" : NewBodyOperationType.ADD, "depth" : 25 * mm, "offsetDistance" : 25 * mm});
        }
        {
            var Q0;
            Q0=qCreatedBy(makeId("Top.planeOp"),FACE);
            var sketch = newSketch(context, id + "F38", { "sketchPlane" : qUnion([Q0])});
            skLineSegment(sketch, "E491.bottom", {"start": v(2200, 17253.85) * mm, "end": v(2300, 17253.85) * mm});
            skLineSegment(sketch, "E491.top", {"start": v(2200, -10844.78) * mm, "end": v(2300, -10844.78) * mm});
            skLineSegment(sketch, "E491.left", {"start": v(2200, 17153.85) * mm, "end": v(2200, -10844.78) * mm});
            skLineSegment(sketch, "E491.right", {"start": v(2300, 17253.85) * mm, "end": v(2300, -10844.78) * mm});
            skLineSegment(sketch, "E492.bottom", {"start": v(2200, 17253.85) * mm, "end": v(-11250, 17253.85) * mm});
            skLineSegment(sketch, "E492.top", {"start": v(2200, 17153.85) * mm, "end": v(-11150, 17153.85) * mm});
            skLineSegment(sketch, "E492.right", {"start": v(-11250, 17253.85) * mm, "end": v(-11250, 17153.85) * mm});
            skLineSegment(sketch, "E493.top", {"start": v(-11250, -10993.43) * mm, "end": v(-11150, -10993.43) * mm});
            skLineSegment(sketch, "E493.left", {"start": v(-11250, 17153.85) * mm, "end": v(-11250, -10993.43) * mm});
            skLineSegment(sketch, "E493.right", {"start": v(-11150, 17153.85) * mm, "end": v(-11150, -10993.43) * mm});
            skSolve(sketch);
        }
        {
            var Q0;
            Q0 = qSketchRegion(id + "F38", true);
            extrude(context, id + "F39", {"entities" : qUnion([Q0]), "depth" : 2000 * mm, "offsetDistance" : 25 * mm});
        }
        {
            var Q0;
            Q0=makeQuery(id+"F1.opExtrude","SWEPT_FACE",FACE,{"disambiguationData":[OSD([sQuery(id+"F0.wireOp",EDGE,"E0")])]});
            var sketch = newSketch(context, id + "F40", { "sketchPlane" : qUnion([Q0])});
            skLineSegment(sketch, "E494.bottom", {"start": v(7650, 2300) * mm, "end": v(8450, 2300) * mm});
            skLineSegment(sketch, "E494.top", {"start": v(7650, 300) * mm, "end": v(8450, 300) * mm});
            skLineSegment(sketch, "E494.left", {"start": v(7650, 2300) * mm, "end": v(7650, 300) * mm});
            skLineSegment(sketch, "E494.right", {"start": v(8450, 2300) * mm, "end": v(8450, 300) * mm});
            skLineSegment(sketch, "E495.bottom", {"start": v(8750, 2300) * mm, "end": v(10200, 2300) * mm});
            skLineSegment(sketch, "E495.top", {"start": v(8750, 1300) * mm, "end": v(10200, 1300) * mm});
            skLineSegment(sketch, "E495.left", {"start": v(8750, 2300) * mm, "end": v(8750, 1300) * mm});
            skLineSegment(sketch, "E495.right", {"start": v(10200, 2300) * mm, "end": v(10200, 1300) * mm});
            skLineSegment(sketch, "E496.bottom", {"start": v(8850, 2200) * mm, "end": v(10100, 2200) * mm});
            skLineSegment(sketch, "E496.top", {"start": v(8850, 1900) * mm, "end": v(10100, 1900) * mm});
            skLineSegment(sketch, "E496.left", {"start": v(8850, 2200) * mm, "end": v(8850, 1900) * mm});
            skLineSegment(sketch, "E496.right", {"start": v(10100, 2200) * mm, "end": v(10100, 1900) * mm});
            skLineSegment(sketch, "E497.bottom", {"start": v(8850, 1800) * mm, "end": v(10100, 1800) * mm});
            skLineSegment(sketch, "E497.top", {"start": v(8850, 1400) * mm, "end": v(10100, 1400) * mm});
            skLineSegment(sketch, "E497.left", {"start": v(8850, 1800) * mm, "end": v(8850, 1400) * mm});
            skLineSegment(sketch, "E497.right", {"start": v(10100, 1800) * mm, "end": v(10100, 1400) * mm});
            skLineSegment(sketch, "E498.bottom", {"start": v(7750, 2200) * mm, "end": v(8350, 2200) * mm});
            skLineSegment(sketch, "E498.top", {"start": v(7750, 1000) * mm, "end": v(8350, 1000) * mm});
            skLineSegment(sketch, "E498.left", {"start": v(7750, 2200) * mm, "end": v(7750, 1000) * mm});
            skLineSegment(sketch, "E498.right", {"start": v(8350, 2200) * mm, "end": v(8350, 1000) * mm});
            skSolve(sketch);
        }
        {
            var Q0;
            Q0 = qSketchRegion(id + "F40", true);
            extrude(context, id + "F41", {"entities" : qUnion([Q0]), "operationType" : NewBodyOperationType.ADD, "depth" : 25 * mm, "offsetDistance" : 25 * mm});
        }
        {
            var Q0;
            {var subQ1=sQuery(id+"F2.wireOp",EDGE,"E83.left");var subQ4=sQuery(id+"F0.wireOp",EDGE,"E74.trimOffspring");var subQ5=sQuery(id+"F0.wireOp",EDGE,"E11");var subQ6=sQuery(id+"F0.wireOp",EDGE,"E7");var subQ8=sQuery(id+"F0.wireOp",EDGE,"E0");Q0=makeQuery(id+"F9.boolean.opBoolean","MERGE",FACE,{"derivedFrom":[makeQuery(id+"F5.boolean.opBoolean","SPLIT",FACE,{"disambiguationData":[TD([makeQuery(id+"F1.opExtrude","SWEPT_FACE",FACE,{"disambiguationData":[OSD([subQ8])]})])],"derivedFrom":makeQuery(id+"F3.boolean.opBoolean","MERGE",FACE,{"derivedFrom":[makeQuery(id+"F1.opExtrude","SWEPT_FACE",FACE,{"disambiguationData":[OSD([subQ6])]}),makeQuery(id+"F1.opExtrude","SWEPT_FACE",FACE,{"disambiguationData":[OSD([subQ5])]}),makeQuery(id+"F1.opExtrude","SWEPT_FACE",FACE,{"disambiguationData":[OSD([subQ4])]}),makeQuery(id+"F3.opExtrude","SWEPT_FACE",FACE,{"disambiguationData":[OSD([subQ1])]})]})}),makeQuery(id+"F9.opExtrude","CAP_FACE",FACE,{"disambiguationData":[OSD([sQuery(id+"F8.wireOp",EDGE,"E167"),sQuery(id+"F8.wireOp",EDGE,"E170"),sQuery(id+"F8.wireOp",EDGE,"E171"),sQuery(id+"F8.wireOp",EDGE,"E172"),sQuery(id+"F8.wireOp",EDGE,"E173"),sQuery(id+"F8.wireOp",EDGE,"E174"),sQuery(id+"F8.wireOp",EDGE,"E175"),sQuery(id+"F8.wireOp",EDGE,"E176"),sQuery(id+"F8.wireOp",EDGE,"E177"),sQuery(id+"F8.wireOp",EDGE,"E178"),sQuery(id+"F8.wireOp",EDGE,"E179"),sQuery(id+"F8.wireOp",EDGE,"E180"),sQuery(id+"F8.wireOp",EDGE,"E181"),sQuery(id+"F8.wireOp",EDGE,"E182"),sQuery(id+"F8.wireOp",EDGE,"E183"),sQuery(id+"F8.wireOp",EDGE,"E184"),sQuery(id+"F8.wireOp",EDGE,"E185"),sQuery(id+"F8.wireOp",EDGE,"E186"),sQuery(id+"F8.wireOp",EDGE,"E187"),sQuery(id+"F8.wireOp",EDGE,"E188"),sQuery(id+"F8.wireOp",EDGE,"E189"),sQuery(id+"F8.wireOp",EDGE,"E190"),sQuery(id+"F8.wireOp",EDGE,"E191"),sQuery(id+"F8.wireOp",EDGE,"E192"),sQuery(id+"F8.wireOp",EDGE,"E193"),sQuery(id+"F8.wireOp",EDGE,"E194"),sQuery(id+"F8.wireOp",EDGE,"E195"),sQuery(id+"F8.wireOp",EDGE,"E196"),sQuery(id+"F8.wireOp",EDGE,"E197"),sQuery(id+"F8.wireOp",EDGE,"E198"),sQuery(id+"F8.wireOp",EDGE,"E199"),sQuery(id+"F8.wireOp",EDGE,"E200"),sQuery(id+"F8.wireOp",EDGE,"E201"),sQuery(id+"F8.wireOp",EDGE,"E202"),sQuery(id+"F8.wireOp",EDGE,"E203"),sQuery(id+"F8.wireOp",EDGE,"E204"),sQuery(id+"F8.wireOp",EDGE,"E205"),sQuery(id+"F8.wireOp",EDGE,"E206"),sQuery(id+"F8.wireOp",EDGE,"E207"),sQuery(id+"F8.wireOp",EDGE,"E208"),sQuery(id+"F8.wireOp",EDGE,"E209"),sQuery(id+"F8.wireOp",EDGE,"E210"),sQuery(id+"F8.wireOp",EDGE,"E211"),sQuery(id+"F8.wireOp",EDGE,"E212"),sQuery(id+"F8.wireOp",EDGE,"E213"),sQuery(id+"F8.wireOp",EDGE,"E214"),sQuery(id+"F8.wireOp",EDGE,"E215"),sQuery(id+"F8.wireOp",EDGE,"E216"),sQuery(id+"F8.wireOp",EDGE,"E217"),sQuery(id+"F8.wireOp",EDGE,"E218.MirrorCS"),sQuery(id+"F8.wireOp",EDGE,"E219.MirrorCS"),sQuery(id+"F8.wireOp",EDGE,"E220.MirrorCS"),sQuery(id+"F8.wireOp",EDGE,"E221.MirrorCS"),sQuery(id+"F8.wireOp",EDGE,"E222.MirrorCS"),sQuery(id+"F8.wireOp",EDGE,"E223.MirrorCS"),sQuery(id+"F8.wireOp",EDGE,"E224.MirrorCS"),sQuery(id+"F8.wireOp",EDGE,"E225.MirrorCS"),sQuery(id+"F8.wireOp",EDGE,"E226.MirrorCS"),sQuery(id+"F8.wireOp",EDGE,"E227.MirrorCS"),sQuery(id+"F8.wireOp",EDGE,"E228.MirrorCS"),sQuery(id+"F8.wireOp",EDGE,"E229.MirrorCS"),sQuery(id+"F8.wireOp",EDGE,"E230.MirrorCS"),sQuery(id+"F8.wireOp",EDGE,"E231.MirrorCS"),sQuery(id+"F8.wireOp",EDGE,"E232.MirrorCS"),sQuery(id+"F8.wireOp",EDGE,"E233.MirrorCS"),sQuery(id+"F8.wireOp",EDGE,"E234.MirrorCS"),sQuery(id+"F8.wireOp",EDGE,"E235.MirrorCS"),sQuery(id+"F8.wireOp",EDGE,"E236.MirrorCS"),sQuery(id+"F8.wireOp",EDGE,"E237.MirrorCS"),sQuery(id+"F8.wireOp",EDGE,"E238.MirrorCS"),sQuery(id+"F8.wireOp",EDGE,"E239.MirrorCS"),sQuery(id+"F8.wireOp",EDGE,"E240.MirrorCS"),sQuery(id+"F8.wireOp",EDGE,"E241.MirrorCS"),sQuery(id+"F8.wireOp",EDGE,"E242.MirrorCS"),sQuery(id+"F8.wireOp",EDGE,"E243.MirrorCS"),sQuery(id+"F8.wireOp",EDGE,"E244.MirrorCS"),sQuery(id+"F8.wireOp",EDGE,"E245.MirrorCS"),sQuery(id+"F8.wireOp",EDGE,"E246.MirrorCS"),sQuery(id+"F8.wireOp",EDGE,"E247.MirrorCS"),sQuery(id+"F8.wireOp",EDGE,"E248.MirrorCS"),sQuery(id+"F8.wireOp",EDGE,"E249.MirrorCS"),sQuery(id+"F8.wireOp",EDGE,"E250.MirrorCS"),sQuery(id+"F8.wireOp",EDGE,"E251.MirrorCS"),sQuery(id+"F8.wireOp",EDGE,"E252.MirrorCS"),sQuery(id+"F8.wireOp",EDGE,"E253.MirrorCS"),sQuery(id+"F8.wireOp",EDGE,"E254.MirrorCS"),sQuery(id+"F8.wireOp",EDGE,"E255.MirrorCS"),sQuery(id+"F8.wireOp",EDGE,"E256.MirrorCS"),sQuery(id+"F8.wireOp",EDGE,"E257.MirrorCS"),sQuery(id+"F8.wireOp",EDGE,"E258.MirrorCS"),sQuery(id+"F8.wireOp",EDGE,"E259.MirrorCS"),sQuery(id+"F8.wireOp",EDGE,"E260.MirrorCS"),sQuery(id+"F8.wireOp",EDGE,"E261.MirrorCS"),sQuery(id+"F8.wireOp",EDGE,"E262.MirrorCS"),sQuery(id+"F8.wireOp",EDGE,"E263.MirrorCS"),sQuery(id+"F8.wireOp",EDGE,"E264.MirrorCS"),sQuery(id+"F8.wireOp",EDGE,"E265.MirrorCS")])],"isStart":false})]});}
            var sketch = newSketch(context, id + "F42", { "sketchPlane" : qUnion([Q0])});
            skLineSegment(sketch, "E499.bottom", {"start": v(-8530, 300) * mm, "end": v(-6330, 300) * mm});
            skLineSegment(sketch, "E499.top", {"start": v(-8530, 2500) * mm, "end": v(-6330, 2500) * mm});
            skLineSegment(sketch, "E499.left", {"start": v(-8530, 300) * mm, "end": v(-8530, 2500) * mm});
            skLineSegment(sketch, "E499.right", {"start": v(-6330, 300) * mm, "end": v(-6330, 2500) * mm});
            skLineSegment(sketch, "E500.bottom", {"start": v(-8430, 2400) * mm, "end": v(-6430, 2400) * mm});
            skLineSegment(sketch, "E500.top", {"start": v(-8430, 400) * mm, "end": v(-6430, 400) * mm});
            skLineSegment(sketch, "E500.left", {"start": v(-8430, 2400) * mm, "end": v(-8430, 400) * mm});
            skLineSegment(sketch, "E500.right", {"start": v(-6430, 2400) * mm, "end": v(-6430, 400) * mm});
            skSolve(sketch);
        }
        {
            var Q0;
            Q0 = qSketchRegion(id + "F42", true);
            extrude(context, id + "F43", {"entities" : qUnion([Q0]), "operationType" : NewBodyOperationType.ADD, "depth" : 25 * mm, "offsetDistance" : 25 * mm});
        }
        {
            var Q0;
            Q0=makeQuery(id+"F13.boolean.opBoolean","MERGE",FACE,{"derivedFrom":[makeQuery(id+"F11.opExtrude","SWEPT_FACE",FACE,{"disambiguationData":[OSD([sQuery(id+"F10.wireOp",EDGE,"E266.right")])]}),makeQuery(id+"F13.opExtrude","CAP_FACE",FACE,{"disambiguationData":[OSD([sQuery(id+"F12.wireOp",EDGE,"E271"),sQuery(id+"F12.wireOp",EDGE,"E274"),sQuery(id+"F12.wireOp",EDGE,"E275"),sQuery(id+"F12.wireOp",EDGE,"E276"),sQuery(id+"F12.wireOp",EDGE,"E277"),sQuery(id+"F12.wireOp",EDGE,"E278"),sQuery(id+"F12.wireOp",EDGE,"E279"),sQuery(id+"F12.wireOp",EDGE,"E280"),sQuery(id+"F12.wireOp",EDGE,"E281"),sQuery(id+"F12.wireOp",EDGE,"E282"),sQuery(id+"F12.wireOp",EDGE,"E283"),sQuery(id+"F12.wireOp",EDGE,"E284"),sQuery(id+"F12.wireOp",EDGE,"E285"),sQuery(id+"F12.wireOp",EDGE,"E286"),sQuery(id+"F12.wireOp",EDGE,"E287"),sQuery(id+"F12.wireOp",EDGE,"E288"),sQuery(id+"F12.wireOp",EDGE,"E289"),sQuery(id+"F12.wireOp",EDGE,"E290"),sQuery(id+"F12.wireOp",EDGE,"E291"),sQuery(id+"F12.wireOp",EDGE,"E292"),sQuery(id+"F12.wireOp",EDGE,"E293"),sQuery(id+"F12.wireOp",EDGE,"E294"),sQuery(id+"F12.wireOp",EDGE,"E295"),sQuery(id+"F12.wireOp",EDGE,"E296"),sQuery(id+"F12.wireOp",EDGE,"E297"),sQuery(id+"F12.wireOp",EDGE,"E298"),sQuery(id+"F12.wireOp",EDGE,"E299"),sQuery(id+"F12.wireOp",EDGE,"E300"),sQuery(id+"F12.wireOp",EDGE,"E301"),sQuery(id+"F12.wireOp",EDGE,"E302"),sQuery(id+"F12.wireOp",EDGE,"E303"),sQuery(id+"F12.wireOp",EDGE,"E304"),sQuery(id+"F12.wireOp",EDGE,"E305"),sQuery(id+"F12.wireOp",EDGE,"E306"),sQuery(id+"F12.wireOp",EDGE,"E307"),sQuery(id+"F12.wireOp",EDGE,"E308"),sQuery(id+"F12.wireOp",EDGE,"E309"),sQuery(id+"F12.wireOp",EDGE,"E310"),sQuery(id+"F12.wireOp",EDGE,"E311"),sQuery(id+"F12.wireOp",EDGE,"E312"),sQuery(id+"F12.wireOp",EDGE,"E313"),sQuery(id+"F12.wireOp",EDGE,"E314"),sQuery(id+"F12.wireOp",EDGE,"E315"),sQuery(id+"F12.wireOp",EDGE,"E316"),sQuery(id+"F12.wireOp",EDGE,"E317"),sQuery(id+"F12.wireOp",EDGE,"E318"),sQuery(id+"F12.wireOp",EDGE,"E319"),sQuery(id+"F12.wireOp",EDGE,"E320.MirrorCS"),sQuery(id+"F12.wireOp",EDGE,"E321.MirrorCS"),sQuery(id+"F12.wireOp",EDGE,"E322.MirrorCS"),sQuery(id+"F12.wireOp",EDGE,"E323.MirrorCS"),sQuery(id+"F12.wireOp",EDGE,"E324.MirrorCS"),sQuery(id+"F12.wireOp",EDGE,"E325.MirrorCS"),sQuery(id+"F12.wireOp",EDGE,"E326.MirrorCS"),sQuery(id+"F12.wireOp",EDGE,"E327.MirrorCS"),sQuery(id+"F12.wireOp",EDGE,"E328.MirrorCS"),sQuery(id+"F12.wireOp",EDGE,"E329.MirrorCS"),sQuery(id+"F12.wireOp",EDGE,"E330.MirrorCS"),sQuery(id+"F12.wireOp",EDGE,"E331.MirrorCS"),sQuery(id+"F12.wireOp",EDGE,"E332.MirrorCS"),sQuery(id+"F12.wireOp",EDGE,"E333.MirrorCS"),sQuery(id+"F12.wireOp",EDGE,"E334.MirrorCS"),sQuery(id+"F12.wireOp",EDGE,"E335.MirrorCS"),sQuery(id+"F12.wireOp",EDGE,"E336.MirrorCS"),sQuery(id+"F12.wireOp",EDGE,"E337.MirrorCS"),sQuery(id+"F12.wireOp",EDGE,"E338.MirrorCS"),sQuery(id+"F12.wireOp",EDGE,"E339.MirrorCS"),sQuery(id+"F12.wireOp",EDGE,"E340.MirrorCS"),sQuery(id+"F12.wireOp",EDGE,"E341.MirrorCS"),sQuery(id+"F12.wireOp",EDGE,"E342.MirrorCS"),sQuery(id+"F12.wireOp",EDGE,"E343.MirrorCS"),sQuery(id+"F12.wireOp",EDGE,"E344.MirrorCS"),sQuery(id+"F12.wireOp",EDGE,"E345.MirrorCS"),sQuery(id+"F12.wireOp",EDGE,"E346.MirrorCS"),sQuery(id+"F12.wireOp",EDGE,"E347.MirrorCS"),sQuery(id+"F12.wireOp",EDGE,"E348.MirrorCS"),sQuery(id+"F12.wireOp",EDGE,"E349.MirrorCS"),sQuery(id+"F12.wireOp",EDGE,"E350.MirrorCS"),sQuery(id+"F12.wireOp",EDGE,"E351.MirrorCS"),sQuery(id+"F12.wireOp",EDGE,"E352.MirrorCS"),sQuery(id+"F12.wireOp",EDGE,"E353.MirrorCS"),sQuery(id+"F12.wireOp",EDGE,"E354.MirrorCS"),sQuery(id+"F12.wireOp",EDGE,"E355.MirrorCS"),sQuery(id+"F12.wireOp",EDGE,"E356.MirrorCS"),sQuery(id+"F12.wireOp",EDGE,"E357.MirrorCS"),sQuery(id+"F12.wireOp",EDGE,"E358.MirrorCS"),sQuery(id+"F12.wireOp",EDGE,"E359.MirrorCS"),sQuery(id+"F12.wireOp",EDGE,"E360.MirrorCS"),sQuery(id+"F12.wireOp",EDGE,"E361.MirrorCS"),sQuery(id+"F12.wireOp",EDGE,"E362.MirrorCS"),sQuery(id+"F12.wireOp",EDGE,"E363.MirrorCS"),sQuery(id+"F12.wireOp",EDGE,"E364.MirrorCS"),sQuery(id+"F12.wireOp",EDGE,"E365.MirrorCS")])],"isStart":true})]});
            var sketch = newSketch(context, id + "F44", { "sketchPlane" : qUnion([Q0])});
            skLineSegment(sketch, "E501", {"start": v(8780, 0) * mm, "end": v(8780, -460.14) * mm});
            skLineSegment(sketch, "E502", {"start": v(8780, -460.14) * mm, "end": v(0, 0) * mm});
            skLineSegment(sketch, "E503", {"start": v(0, 0) * mm, "end": v(8780, 0) * mm});
            skSolve(sketch);
        }
        {
            var Q0;
            Q0 = qSketchRegion(id + "F44", true);
            var Q1;
            {var subQ0=sQuery(id+"F8.wireOp",EDGE,"E222.MirrorCS");var subQ1=sQuery(id+"F8.wireOp",EDGE,"E221.MirrorCS");var subQ2=sQuery(id+"F8.wireOp",EDGE,"E220.MirrorCS");var subQ3=sQuery(id+"F8.wireOp",EDGE,"E218.MirrorCS");var subQ4=sQuery(id+"F8.wireOp",EDGE,"E217");var subQ5=sQuery(id+"F8.wireOp",EDGE,"E215");var subQ6=sQuery(id+"F8.wireOp",EDGE,"E214");var subQ7=sQuery(id+"F8.wireOp",EDGE,"E213");var subQ8=sQuery(id+"F8.wireOp",EDGE,"E212");var subQ9=sQuery(id+"F8.wireOp",EDGE,"E211");var subQ10=sQuery(id+"F8.wireOp",EDGE,"E210");var subQ11=sQuery(id+"F8.wireOp",EDGE,"E209");var subQ12=sQuery(id+"F8.wireOp",EDGE,"E208");var subQ13=sQuery(id+"F8.wireOp",EDGE,"E207");var subQ14=sQuery(id+"F8.wireOp",EDGE,"E206");var subQ16=sQuery(id+"F8.wireOp",EDGE,"E205");var subQ17=sQuery(id+"F8.wireOp",EDGE,"E204");var subQ19=sQuery(id+"F8.wireOp",EDGE,"E203");var subQ20=sQuery(id+"F8.wireOp",EDGE,"E202");var subQ21=sQuery(id+"F8.wireOp",EDGE,"E201");var subQ22=sQuery(id+"F8.wireOp",EDGE,"E200");var subQ23=sQuery(id+"F8.wireOp",EDGE,"E199");var subQ24=sQuery(id+"F8.wireOp",EDGE,"E198");var subQ25=sQuery(id+"F8.wireOp",EDGE,"E197");var subQ26=sQuery(id+"F8.wireOp",EDGE,"E194");var subQ27=sQuery(id+"F8.wireOp",EDGE,"E193");var subQ28=sQuery(id+"F8.wireOp",EDGE,"E191");var subQ29=sQuery(id+"F8.wireOp",EDGE,"E190");var subQ30=sQuery(id+"F8.wireOp",EDGE,"E189");var subQ31=sQuery(id+"F8.wireOp",EDGE,"E188");var subQ32=sQuery(id+"F8.wireOp",EDGE,"E187");var subQ33=sQuery(id+"F8.wireOp",EDGE,"E186");var subQ35=sQuery(id+"F8.wireOp",EDGE,"E216");var subQ39=sQuery(id+"F8.wireOp",EDGE,"E195");var subQ42=sQuery(id+"F8.wireOp",EDGE,"E261.MirrorCS");var subQ46=sQuery(id+"F8.wireOp",EDGE,"E192");var subQ49=sQuery(id+"F8.wireOp",EDGE,"E258.MirrorCS");var subQ55=sQuery(id+"F8.wireOp",EDGE,"E196");var subQ56=sQuery(id+"F8.wireOp",EDGE,"E253.MirrorCS");var subQ57=sQuery(id+"F8.wireOp",EDGE,"E185");var subQ60=sQuery(id+"F8.wireOp",EDGE,"E180");var subQ63=sQuery(id+"F8.wireOp",EDGE,"E237.MirrorCS");var subQ65=sQuery(id+"F8.wireOp",EDGE,"E179");var subQ68=sQuery(id+"F8.wireOp",EDGE,"E219.MirrorCS");var subQ72=sQuery(id+"F8.wireOp",EDGE,"E173");var subQ74=sQuery(id+"F8.wireOp",EDGE,"E174");var subQ75=sQuery(id+"F0.wireOp",EDGE,"E0");var subQ76=makeQuery(id+"F1.opExtrude","SWEPT_FACE",FACE,{"disambiguationData":[OSD([subQ75])]});var subQ77=sQuery(id+"F8.wireOp",EDGE,"E231.MirrorCS");var subQ79=sQuery(id+"F8.wireOp",EDGE,"E175");var subQ80=sQuery(id+"F0.wireOp",EDGE,"E74.trimOffspring");var subQ81=sQuery(id+"F0.wireOp",EDGE,"E11");var subQ82=sQuery(id+"F0.wireOp",EDGE,"E7");var subQ85=sQuery(id+"F8.wireOp",EDGE,"E232.MirrorCS");var subQ87=sQuery(id+"F8.wireOp",EDGE,"E176");var subQ89=sQuery(id+"F8.wireOp",EDGE,"E177");var subQ91=sQuery(id+"F8.wireOp",EDGE,"E178");var subQ94=sQuery(id+"F8.wireOp",EDGE,"E167");var subQ95=sQuery(id+"F8.wireOp",EDGE,"E181");var subQ98=sQuery(id+"F8.wireOp",EDGE,"E170");var subQ99=sQuery(id+"F8.wireOp",EDGE,"E182");var subQ101=sQuery(id+"F8.wireOp",EDGE,"E239.MirrorCS");var subQ104=sQuery(id+"F8.wireOp",EDGE,"E171");var subQ105=sQuery(id+"F8.wireOp",EDGE,"E183");var subQ108=sQuery(id+"F8.wireOp",EDGE,"E172");var subQ109=sQuery(id+"F8.wireOp",EDGE,"E184");var subQ111=sQuery(id+"F8.wireOp",EDGE,"E223.MirrorCS");var subQ112=sQuery(id+"F8.wireOp",EDGE,"E224.MirrorCS");var subQ113=sQuery(id+"F8.wireOp",EDGE,"E225.MirrorCS");var subQ114=sQuery(id+"F8.wireOp",EDGE,"E226.MirrorCS");var subQ115=sQuery(id+"F8.wireOp",EDGE,"E227.MirrorCS");var subQ116=sQuery(id+"F8.wireOp",EDGE,"E228.MirrorCS");var subQ117=sQuery(id+"F8.wireOp",EDGE,"E229.MirrorCS");var subQ118=sQuery(id+"F8.wireOp",EDGE,"E230.MirrorCS");var subQ119=sQuery(id+"F8.wireOp",EDGE,"E233.MirrorCS");var subQ120=sQuery(id+"F8.wireOp",EDGE,"E234.MirrorCS");var subQ121=sQuery(id+"F8.wireOp",EDGE,"E235.MirrorCS");var subQ122=sQuery(id+"F8.wireOp",EDGE,"E236.MirrorCS");var subQ123=sQuery(id+"F8.wireOp",EDGE,"E238.MirrorCS");var subQ124=sQuery(id+"F8.wireOp",EDGE,"E240.MirrorCS");var subQ125=sQuery(id+"F8.wireOp",EDGE,"E241.MirrorCS");var subQ126=sQuery(id+"F8.wireOp",EDGE,"E242.MirrorCS");var subQ127=sQuery(id+"F8.wireOp",EDGE,"E243.MirrorCS");var subQ128=sQuery(id+"F8.wireOp",EDGE,"E244.MirrorCS");var subQ129=sQuery(id+"F8.wireOp",EDGE,"E245.MirrorCS");var subQ130=sQuery(id+"F8.wireOp",EDGE,"E246.MirrorCS");var subQ131=sQuery(id+"F8.wireOp",EDGE,"E247.MirrorCS");var subQ132=sQuery(id+"F8.wireOp",EDGE,"E248.MirrorCS");var subQ133=sQuery(id+"F8.wireOp",EDGE,"E249.MirrorCS");var subQ134=sQuery(id+"F8.wireOp",EDGE,"E250.MirrorCS");var subQ135=sQuery(id+"F8.wireOp",EDGE,"E251.MirrorCS");var subQ136=sQuery(id+"F8.wireOp",EDGE,"E252.MirrorCS");var subQ137=sQuery(id+"F8.wireOp",EDGE,"E254.MirrorCS");var subQ138=sQuery(id+"F8.wireOp",EDGE,"E255.MirrorCS");var subQ139=sQuery(id+"F8.wireOp",EDGE,"E256.MirrorCS");var subQ140=sQuery(id+"F8.wireOp",EDGE,"E257.MirrorCS");var subQ141=sQuery(id+"F8.wireOp",EDGE,"E259.MirrorCS");var subQ142=sQuery(id+"F8.wireOp",EDGE,"E260.MirrorCS");var subQ143=sQuery(id+"F8.wireOp",EDGE,"E262.MirrorCS");var subQ144=sQuery(id+"F8.wireOp",EDGE,"E263.MirrorCS");var subQ145=sQuery(id+"F8.wireOp",EDGE,"E264.MirrorCS");var subQ146=sQuery(id+"F8.wireOp",EDGE,"E265.MirrorCS");var subQ147=sQuery(id+"F2.wireOp",EDGE,"E83.left");Q1=makeQuery(id+"F43.boolean.opBoolean","SPLIT",FACE,{"disambiguationData":[TD([subQ76])],"derivedFrom":makeQuery(id+"F9.boolean.opBoolean","MERGE",FACE,{"derivedFrom":[makeQuery(id+"F5.boolean.opBoolean","SPLIT",FACE,{"disambiguationData":[TD([subQ76])],"derivedFrom":makeQuery(id+"F3.boolean.opBoolean","MERGE",FACE,{"derivedFrom":[makeQuery(id+"F1.opExtrude","SWEPT_FACE",FACE,{"disambiguationData":[OSD([subQ82])]}),makeQuery(id+"F1.opExtrude","SWEPT_FACE",FACE,{"disambiguationData":[OSD([subQ81])]}),makeQuery(id+"F1.opExtrude","SWEPT_FACE",FACE,{"disambiguationData":[OSD([subQ80])]}),makeQuery(id+"F3.opExtrude","SWEPT_FACE",FACE,{"disambiguationData":[OSD([subQ147])]})]})}),makeQuery(id+"F9.opExtrude","CAP_FACE",FACE,{"disambiguationData":[OSD([subQ94,subQ98,subQ104,subQ108,subQ72,subQ74,subQ79,subQ87,subQ89,subQ91,subQ65,subQ60,subQ95,subQ99,subQ105,subQ109,subQ57,subQ33,subQ32,subQ31,subQ30,subQ29,subQ28,subQ46,subQ27,subQ26,subQ39,subQ55,subQ25,subQ24,subQ23,subQ22,subQ21,subQ20,subQ19,subQ17,subQ16,subQ14,subQ13,subQ12,subQ11,subQ10,subQ9,subQ8,subQ7,subQ6,subQ5,subQ35,subQ4,subQ3,subQ68,subQ2,subQ1,subQ0,subQ111,subQ112,subQ113,subQ114,subQ115,subQ116,subQ117,subQ118,subQ77,subQ85,subQ119,subQ120,subQ121,subQ122,subQ63,subQ123,subQ101,subQ124,subQ125,subQ126,subQ127,subQ128,subQ129,subQ130,subQ131,subQ132,subQ133,subQ134,subQ135,subQ136,subQ56,subQ137,subQ138,subQ139,subQ140,subQ49,subQ141,subQ142,subQ42,subQ143,subQ144,subQ145,subQ146])],"isStart":false})]})});}
            extrude(context, id + "F45", {"entities" : qUnion([Q0]), "operationType" : NewBodyOperationType.ADD, "endBound" : BoundingType.UP_TO_SURFACE, "oppositeDirection" : true, "depth" : 25 * mm, "endBoundEntityFace" : qUnion([Q1]), "offsetDistance" : 25 * mm});
        }
        {
            var Q0;
            Q0=qCreatedBy(makeId("Top.planeOp"),FACE);
            var sketch = newSketch(context, id + "F46", { "sketchPlane" : qUnion([Q0])});
            skLineSegment(sketch, "E504", {"start": v(-7450, 8780) * mm, "end": v(-3950, 8780) * mm});
            skLineSegment(sketch, "E505", {"start": v(-3950, 8780) * mm, "end": v(-3950, 10280) * mm});
            skLineSegment(sketch, "E506", {"start": v(-3950, 10280) * mm, "end": v(-10450, 10280) * mm});
            skLineSegment(sketch, "E507", {"start": v(-10450, 10280) * mm, "end": v(-10450, 3230) * mm});
            skLineSegment(sketch, "E508", {"start": v(-10450, 3230) * mm, "end": v(-7450, 3230) * mm});
            skLineSegment(sketch, "E509", {"start": v(-7450, 3230) * mm, "end": v(-7450, 8780) * mm});
            skSolve(sketch);
        }
        {
            var Q0;
            Q0 = qSketchRegion(id + "F46", true);
            var Q1;
            Q1=makeQuery(id+"F45.opExtrude","SWEPT_FACE",FACE,{"disambiguationData":[OSD([sQuery(id+"F44.wireOp",EDGE,"E502")])]});
            extrude(context, id + "F47", {"entities" : qUnion([Q0]), "operationType" : NewBodyOperationType.ADD, "depth" : 250 * mm, "offsetDistance" : 25 * mm, "hasSecondDirection" : true, "secondDirectionBound" : SecondDirectionBoundingType.UP_TO_SURFACE, "secondDirectionOppositeDirection" : true, "secondDirectionDepth" : 25 * mm, "secondDirectionBoundEntityFace" : qUnion([Q1])});
        }
        {
            var Q0;
            {var subQ1=sQuery(id+"F2.wireOp",EDGE,"E83.left");var subQ4=sQuery(id+"F0.wireOp",EDGE,"E74.trimOffspring");var subQ5=sQuery(id+"F0.wireOp",EDGE,"E11");var subQ6=sQuery(id+"F0.wireOp",EDGE,"E7");var subQ8=sQuery(id+"F0.wireOp",EDGE,"E0");Q0=makeQuery(id+"F43.boolean.opBoolean","SPLIT",FACE,{"disambiguationData":[TD([makeQuery(id+"F43.opExtrude","SWEPT_FACE",FACE,{"disambiguationData":[OSD([sQuery(id+"F42.wireOp",EDGE,"E500.bottom")])]})])],"derivedFrom":makeQuery(id+"F9.boolean.opBoolean","MERGE",FACE,{"derivedFrom":[makeQuery(id+"F5.boolean.opBoolean","SPLIT",FACE,{"disambiguationData":[TD([makeQuery(id+"F1.opExtrude","SWEPT_FACE",FACE,{"disambiguationData":[OSD([subQ8])]})])],"derivedFrom":makeQuery(id+"F3.boolean.opBoolean","MERGE",FACE,{"derivedFrom":[makeQuery(id+"F1.opExtrude","SWEPT_FACE",FACE,{"disambiguationData":[OSD([subQ6])]}),makeQuery(id+"F1.opExtrude","SWEPT_FACE",FACE,{"disambiguationData":[OSD([subQ5])]}),makeQuery(id+"F1.opExtrude","SWEPT_FACE",FACE,{"disambiguationData":[OSD([subQ4])]}),makeQuery(id+"F3.opExtrude","SWEPT_FACE",FACE,{"disambiguationData":[OSD([subQ1])]})]})}),makeQuery(id+"F9.opExtrude","CAP_FACE",FACE,{"disambiguationData":[OSD([sQuery(id+"F8.wireOp",EDGE,"E167"),sQuery(id+"F8.wireOp",EDGE,"E170"),sQuery(id+"F8.wireOp",EDGE,"E171"),sQuery(id+"F8.wireOp",EDGE,"E172"),sQuery(id+"F8.wireOp",EDGE,"E173"),sQuery(id+"F8.wireOp",EDGE,"E174"),sQuery(id+"F8.wireOp",EDGE,"E175"),sQuery(id+"F8.wireOp",EDGE,"E176"),sQuery(id+"F8.wireOp",EDGE,"E177"),sQuery(id+"F8.wireOp",EDGE,"E178"),sQuery(id+"F8.wireOp",EDGE,"E179"),sQuery(id+"F8.wireOp",EDGE,"E180"),sQuery(id+"F8.wireOp",EDGE,"E181"),sQuery(id+"F8.wireOp",EDGE,"E182"),sQuery(id+"F8.wireOp",EDGE,"E183"),sQuery(id+"F8.wireOp",EDGE,"E184"),sQuery(id+"F8.wireOp",EDGE,"E185"),sQuery(id+"F8.wireOp",EDGE,"E186"),sQuery(id+"F8.wireOp",EDGE,"E187"),sQuery(id+"F8.wireOp",EDGE,"E188"),sQuery(id+"F8.wireOp",EDGE,"E189"),sQuery(id+"F8.wireOp",EDGE,"E190"),sQuery(id+"F8.wireOp",EDGE,"E191"),sQuery(id+"F8.wireOp",EDGE,"E192"),sQuery(id+"F8.wireOp",EDGE,"E193"),sQuery(id+"F8.wireOp",EDGE,"E194"),sQuery(id+"F8.wireOp",EDGE,"E195"),sQuery(id+"F8.wireOp",EDGE,"E196"),sQuery(id+"F8.wireOp",EDGE,"E197"),sQuery(id+"F8.wireOp",EDGE,"E198"),sQuery(id+"F8.wireOp",EDGE,"E199"),sQuery(id+"F8.wireOp",EDGE,"E200"),sQuery(id+"F8.wireOp",EDGE,"E201"),sQuery(id+"F8.wireOp",EDGE,"E202"),sQuery(id+"F8.wireOp",EDGE,"E203"),sQuery(id+"F8.wireOp",EDGE,"E204"),sQuery(id+"F8.wireOp",EDGE,"E205"),sQuery(id+"F8.wireOp",EDGE,"E206"),sQuery(id+"F8.wireOp",EDGE,"E207"),sQuery(id+"F8.wireOp",EDGE,"E208"),sQuery(id+"F8.wireOp",EDGE,"E209"),sQuery(id+"F8.wireOp",EDGE,"E210"),sQuery(id+"F8.wireOp",EDGE,"E211"),sQuery(id+"F8.wireOp",EDGE,"E212"),sQuery(id+"F8.wireOp",EDGE,"E213"),sQuery(id+"F8.wireOp",EDGE,"E214"),sQuery(id+"F8.wireOp",EDGE,"E215"),sQuery(id+"F8.wireOp",EDGE,"E216"),sQuery(id+"F8.wireOp",EDGE,"E217"),sQuery(id+"F8.wireOp",EDGE,"E218.MirrorCS"),sQuery(id+"F8.wireOp",EDGE,"E219.MirrorCS"),sQuery(id+"F8.wireOp",EDGE,"E220.MirrorCS"),sQuery(id+"F8.wireOp",EDGE,"E221.MirrorCS"),sQuery(id+"F8.wireOp",EDGE,"E222.MirrorCS"),sQuery(id+"F8.wireOp",EDGE,"E223.MirrorCS"),sQuery(id+"F8.wireOp",EDGE,"E224.MirrorCS"),sQuery(id+"F8.wireOp",EDGE,"E225.MirrorCS"),sQuery(id+"F8.wireOp",EDGE,"E226.MirrorCS"),sQuery(id+"F8.wireOp",EDGE,"E227.MirrorCS"),sQuery(id+"F8.wireOp",EDGE,"E228.MirrorCS"),sQuery(id+"F8.wireOp",EDGE,"E229.MirrorCS"),sQuery(id+"F8.wireOp",EDGE,"E230.MirrorCS"),sQuery(id+"F8.wireOp",EDGE,"E231.MirrorCS"),sQuery(id+"F8.wireOp",EDGE,"E232.MirrorCS"),sQuery(id+"F8.wireOp",EDGE,"E233.MirrorCS"),sQuery(id+"F8.wireOp",EDGE,"E234.MirrorCS"),sQuery(id+"F8.wireOp",EDGE,"E235.MirrorCS"),sQuery(id+"F8.wireOp",EDGE,"E236.MirrorCS"),sQuery(id+"F8.wireOp",EDGE,"E237.MirrorCS"),sQuery(id+"F8.wireOp",EDGE,"E238.MirrorCS"),sQuery(id+"F8.wireOp",EDGE,"E239.MirrorCS"),sQuery(id+"F8.wireOp",EDGE,"E240.MirrorCS"),sQuery(id+"F8.wireOp",EDGE,"E241.MirrorCS"),sQuery(id+"F8.wireOp",EDGE,"E242.MirrorCS"),sQuery(id+"F8.wireOp",EDGE,"E243.MirrorCS"),sQuery(id+"F8.wireOp",EDGE,"E244.MirrorCS"),sQuery(id+"F8.wireOp",EDGE,"E245.MirrorCS"),sQuery(id+"F8.wireOp",EDGE,"E246.MirrorCS"),sQuery(id+"F8.wireOp",EDGE,"E247.MirrorCS"),sQuery(id+"F8.wireOp",EDGE,"E248.MirrorCS"),sQuery(id+"F8.wireOp",EDGE,"E249.MirrorCS"),sQuery(id+"F8.wireOp",EDGE,"E250.MirrorCS"),sQuery(id+"F8.wireOp",EDGE,"E251.MirrorCS"),sQuery(id+"F8.wireOp",EDGE,"E252.MirrorCS"),sQuery(id+"F8.wireOp",EDGE,"E253.MirrorCS"),sQuery(id+"F8.wireOp",EDGE,"E254.MirrorCS"),sQuery(id+"F8.wireOp",EDGE,"E255.MirrorCS"),sQuery(id+"F8.wireOp",EDGE,"E256.MirrorCS"),sQuery(id+"F8.wireOp",EDGE,"E257.MirrorCS"),sQuery(id+"F8.wireOp",EDGE,"E258.MirrorCS"),sQuery(id+"F8.wireOp",EDGE,"E259.MirrorCS"),sQuery(id+"F8.wireOp",EDGE,"E260.MirrorCS"),sQuery(id+"F8.wireOp",EDGE,"E261.MirrorCS"),sQuery(id+"F8.wireOp",EDGE,"E262.MirrorCS"),sQuery(id+"F8.wireOp",EDGE,"E263.MirrorCS"),sQuery(id+"F8.wireOp",EDGE,"E264.MirrorCS"),sQuery(id+"F8.wireOp",EDGE,"E265.MirrorCS")])],"isStart":false})]})});}
            var sketch = newSketch(context, id + "F48", { "sketchPlane" : qUnion([Q0])});
            skLineSegment(sketch, "E510.0.0", {"start": v(-8430, 400) * mm, "end": v(-6430, 400) * mm});
            skLineSegment(sketch, "E510.0.1", {"start": v(-6430, 400) * mm, "end": v(-6430, 2400) * mm});
            skLineSegment(sketch, "E510.0.2", {"start": v(-6430, 2400) * mm, "end": v(-8430, 2400) * mm});
            skLineSegment(sketch, "E510.0.3", {"start": v(-8430, 2400) * mm, "end": v(-8430, 400) * mm});
            skSolve(sketch);
        }
        {
            var Q0;
            Q0 = qSketchRegion(id + "F48", true);
            extrude(context, id + "F49", {"entities" : qUnion([Q0]), "operationType" : NewBodyOperationType.REMOVE, "endBound" : BoundingType.UP_TO_NEXT, "oppositeDirection" : true, "depth" : 25 * mm, "offsetDistance" : 25 * mm});
        }
        {
            var Q0;
            {var subQ111=sQuery(id+"F10.wireOp",EDGE,"E266.top");var subQ215=sQuery(id+"F0.wireOp",EDGE,"E6");var subQ216=sQuery(id+"F0.wireOp",EDGE,"E5");var subQ219=makeQuery(id+"F1.opExtrude","SWEPT_FACE",FACE,{"disambiguationData":[OSD([subQ216])]});Q0=makeQuery(id+"F45.boolean.opBoolean","MERGE",FACE,{"derivedFrom":[makeQuery(id+"F35.boolean.opBoolean","SPLIT",FACE,{"disambiguationData":[TD([subQ219])],"derivedFrom":makeQuery(id+"F19.boolean.opBoolean","SPLIT",FACE,{"disambiguationData":[TD([subQ219])],"derivedFrom":makeQuery(id+"F11.boolean.opBoolean","MERGE",FACE,{"derivedFrom":[makeQuery(id+"F3.boolean.opBoolean","MERGE",FACE,{"derivedFrom":[makeQuery(id+"F1.opExtrude","SWEPT_FACE",FACE,{"disambiguationData":[OSD([subQ215])]}),makeQuery(id+"F3.opExtrude","SWEPT_FACE",FACE,{"disambiguationData":[OSD([sQuery(id+"F2.wireOp",EDGE,"E83.bottom")])]})]}),makeQuery(id+"F11.opExtrude","SWEPT_FACE",FACE,{"disambiguationData":[OSD([subQ111])]})]})})}),makeQuery(id+"F45.opExtrude","SWEPT_FACE",FACE,{"disambiguationData":[OSD([sQuery(id+"F44.wireOp",EDGE,"E501")])]})]});}
            var sketch = newSketch(context, id + "F50", { "sketchPlane" : qUnion([Q0])});
            skLineSegment(sketch, "E511.0", {"start": v(4900, 2400) * mm, "end": v(4900, 400) * mm});
            skLineSegment(sketch, "E512.0", {"start": v(4900, 2400) * mm, "end": v(7050, 2400) * mm});
            skLineSegment(sketch, "E513.0", {"start": v(7050, 2400) * mm, "end": v(7050, 400) * mm});
            skLineSegment(sketch, "E514.0", {"start": v(4900, 400) * mm, "end": v(7050, 400) * mm});
            skSolve(sketch);
        }
        {
            var Q0;
            Q0 = qSketchRegion(id + "F50", true);
            extrude(context, id + "F51", {"entities" : qUnion([Q0]), "operationType" : NewBodyOperationType.REMOVE, "oppositeDirection" : true, "depth" : 1000 * mm, "offsetDistance" : 25 * mm});
        }
        {
            var Q0;
            Q0=makeQuery(id+"F45.boolean.opBoolean","MERGE",FACE,{"derivedFrom":[makeQuery(id+"F13.boolean.opBoolean","MERGE",FACE,{"derivedFrom":[makeQuery(id+"F11.opExtrude","SWEPT_FACE",FACE,{"disambiguationData":[OSD([sQuery(id+"F10.wireOp",EDGE,"E266.right")])]}),makeQuery(id+"F13.opExtrude","CAP_FACE",FACE,{"disambiguationData":[OSD([sQuery(id+"F12.wireOp",EDGE,"E271"),sQuery(id+"F12.wireOp",EDGE,"E274"),sQuery(id+"F12.wireOp",EDGE,"E275"),sQuery(id+"F12.wireOp",EDGE,"E276"),sQuery(id+"F12.wireOp",EDGE,"E277"),sQuery(id+"F12.wireOp",EDGE,"E278"),sQuery(id+"F12.wireOp",EDGE,"E279"),sQuery(id+"F12.wireOp",EDGE,"E280"),sQuery(id+"F12.wireOp",EDGE,"E281"),sQuery(id+"F12.wireOp",EDGE,"E282"),sQuery(id+"F12.wireOp",EDGE,"E283"),sQuery(id+"F12.wireOp",EDGE,"E284"),sQuery(id+"F12.wireOp",EDGE,"E285"),sQuery(id+"F12.wireOp",EDGE,"E286"),sQuery(id+"F12.wireOp",EDGE,"E287"),sQuery(id+"F12.wireOp",EDGE,"E288"),sQuery(id+"F12.wireOp",EDGE,"E289"),sQuery(id+"F12.wireOp",EDGE,"E290"),sQuery(id+"F12.wireOp",EDGE,"E291"),sQuery(id+"F12.wireOp",EDGE,"E292"),sQuery(id+"F12.wireOp",EDGE,"E293"),sQuery(id+"F12.wireOp",EDGE,"E294"),sQuery(id+"F12.wireOp",EDGE,"E295"),sQuery(id+"F12.wireOp",EDGE,"E296"),sQuery(id+"F12.wireOp",EDGE,"E297"),sQuery(id+"F12.wireOp",EDGE,"E298"),sQuery(id+"F12.wireOp",EDGE,"E299"),sQuery(id+"F12.wireOp",EDGE,"E300"),sQuery(id+"F12.wireOp",EDGE,"E301"),sQuery(id+"F12.wireOp",EDGE,"E302"),sQuery(id+"F12.wireOp",EDGE,"E303"),sQuery(id+"F12.wireOp",EDGE,"E304"),sQuery(id+"F12.wireOp",EDGE,"E305"),sQuery(id+"F12.wireOp",EDGE,"E306"),sQuery(id+"F12.wireOp",EDGE,"E307"),sQuery(id+"F12.wireOp",EDGE,"E308"),sQuery(id+"F12.wireOp",EDGE,"E309"),sQuery(id+"F12.wireOp",EDGE,"E310"),sQuery(id+"F12.wireOp",EDGE,"E311"),sQuery(id+"F12.wireOp",EDGE,"E312"),sQuery(id+"F12.wireOp",EDGE,"E313"),sQuery(id+"F12.wireOp",EDGE,"E314"),sQuery(id+"F12.wireOp",EDGE,"E315"),sQuery(id+"F12.wireOp",EDGE,"E316"),sQuery(id+"F12.wireOp",EDGE,"E317"),sQuery(id+"F12.wireOp",EDGE,"E318"),sQuery(id+"F12.wireOp",EDGE,"E319"),sQuery(id+"F12.wireOp",EDGE,"E320.MirrorCS"),sQuery(id+"F12.wireOp",EDGE,"E321.MirrorCS"),sQuery(id+"F12.wireOp",EDGE,"E322.MirrorCS"),sQuery(id+"F12.wireOp",EDGE,"E323.MirrorCS"),sQuery(id+"F12.wireOp",EDGE,"E324.MirrorCS"),sQuery(id+"F12.wireOp",EDGE,"E325.MirrorCS"),sQuery(id+"F12.wireOp",EDGE,"E326.MirrorCS"),sQuery(id+"F12.wireOp",EDGE,"E327.MirrorCS"),sQuery(id+"F12.wireOp",EDGE,"E328.MirrorCS"),sQuery(id+"F12.wireOp",EDGE,"E329.MirrorCS"),sQuery(id+"F12.wireOp",EDGE,"E330.MirrorCS"),sQuery(id+"F12.wireOp",EDGE,"E331.MirrorCS"),sQuery(id+"F12.wireOp",EDGE,"E332.MirrorCS"),sQuery(id+"F12.wireOp",EDGE,"E333.MirrorCS"),sQuery(id+"F12.wireOp",EDGE,"E334.MirrorCS"),sQuery(id+"F12.wireOp",EDGE,"E335.MirrorCS"),sQuery(id+"F12.wireOp",EDGE,"E336.MirrorCS"),sQuery(id+"F12.wireOp",EDGE,"E337.MirrorCS"),sQuery(id+"F12.wireOp",EDGE,"E338.MirrorCS"),sQuery(id+"F12.wireOp",EDGE,"E339.MirrorCS"),sQuery(id+"F12.wireOp",EDGE,"E340.MirrorCS"),sQuery(id+"F12.wireOp",EDGE,"E341.MirrorCS"),sQuery(id+"F12.wireOp",EDGE,"E342.MirrorCS"),sQuery(id+"F12.wireOp",EDGE,"E343.MirrorCS"),sQuery(id+"F12.wireOp",EDGE,"E344.MirrorCS"),sQuery(id+"F12.wireOp",EDGE,"E345.MirrorCS"),sQuery(id+"F12.wireOp",EDGE,"E346.MirrorCS"),sQuery(id+"F12.wireOp",EDGE,"E347.MirrorCS"),sQuery(id+"F12.wireOp",EDGE,"E348.MirrorCS"),sQuery(id+"F12.wireOp",EDGE,"E349.MirrorCS"),sQuery(id+"F12.wireOp",EDGE,"E350.MirrorCS"),sQuery(id+"F12.wireOp",EDGE,"E351.MirrorCS"),sQuery(id+"F12.wireOp",EDGE,"E352.MirrorCS"),sQuery(id+"F12.wireOp",EDGE,"E353.MirrorCS"),sQuery(id+"F12.wireOp",EDGE,"E354.MirrorCS"),sQuery(id+"F12.wireOp",EDGE,"E355.MirrorCS"),sQuery(id+"F12.wireOp",EDGE,"E356.MirrorCS"),sQuery(id+"F12.wireOp",EDGE,"E357.MirrorCS"),sQuery(id+"F12.wireOp",EDGE,"E358.MirrorCS"),sQuery(id+"F12.wireOp",EDGE,"E359.MirrorCS"),sQuery(id+"F12.wireOp",EDGE,"E360.MirrorCS"),sQuery(id+"F12.wireOp",EDGE,"E361.MirrorCS"),sQuery(id+"F12.wireOp",EDGE,"E362.MirrorCS"),sQuery(id+"F12.wireOp",EDGE,"E363.MirrorCS"),sQuery(id+"F12.wireOp",EDGE,"E364.MirrorCS"),sQuery(id+"F12.wireOp",EDGE,"E365.MirrorCS")])],"isStart":true})]}),makeQuery(id+"F45.opExtrude","CAP_FACE",FACE,{"disambiguationData":[OSD([sQuery(id+"F44.wireOp",EDGE,"E501"),sQuery(id+"F44.wireOp",EDGE,"E502"),sQuery(id+"F44.wireOp",EDGE,"E503")])],"isStart":true})]});
            var sketch = newSketch(context, id + "F52", { "sketchPlane" : qUnion([Q0])});
            skLineSegment(sketch, "E515", {"start": v(8780, 233.12) * mm, "end": v(9080, 233.12) * mm});
            skLineSegment(sketch, "E516", {"start": v(9080, 233.12) * mm, "end": v(9080, -16.88) * mm});
            skLineSegment(sketch, "E517", {"start": v(9080, -16.88) * mm, "end": v(9380, -16.88) * mm});
            skLineSegment(sketch, "E518", {"start": v(9380, -16.88) * mm, "end": v(9380, -266.88) * mm});
            skLineSegment(sketch, "E519", {"start": v(9380, -266.88) * mm, "end": v(9680, -266.88) * mm});
            skLineSegment(sketch, "E520", {"start": v(9680, -266.88) * mm, "end": v(9680, -516.88) * mm});
            skLineSegment(sketch, "E521", {"start": v(9680, -516.88) * mm, "end": v(8780, -460.14) * mm});
            skLineSegment(sketch, "E522", {"start": v(8780, -460.14) * mm, "end": v(8780, 233.12) * mm});
            skSolve(sketch);
        }
        {
            var Q0;
            Q0 = qSketchRegion(id + "F52", true);
            extrude(context, id + "F53", {"entities" : qUnion([Q0]), "operationType" : NewBodyOperationType.ADD, "oppositeDirection" : true, "depth" : 2000 * mm, "offsetDistance" : 25 * mm});
        }
        {
            var Q0;
            Q0=qCreatedBy(makeId("Top.planeOp"),FACE);
            var sketch = newSketch(context, id + "F54", { "sketchPlane" : qUnion([Q0])});
            skCircle(sketch, "E523", {"center": v(-4049.45, -8898.2) * mm, "radius": 436 * mm});
            skSolve(sketch);
        }
        {
            var Q0;
            Q0=qCreatedBy(makeId("Front.planeOp"),FACE);
            var Q1;
            Q1=sQuery(id+"F54.wireOp",VERTEX,"E523.center");
            cPlane(context, id + "F55", {"entities" : qUnion([Q0, Q1]), "cplaneType" : CPlaneType.PLANE_POINT, "offset" : 25 * mm, "width" : 150 * mm, "height" : 150 * mm});
        }
        {
            var Q0;
            Q0=makeQuery(id+"F13.opExtrude","CAP_VERTEX",VERTEX,{"disambiguationData":[OSD([sQuery(id+"F12.wireOp",EDGE,"E318"),sQuery(id+"F12.wireOp",EDGE,"E319")])],"isStart":true});
            var Q1;
            Q1=makeQuery(id+"F13.opExtrude","CAP_VERTEX",VERTEX,{"disambiguationData":[OSD([sQuery(id+"F12.wireOp",EDGE,"E274"),sQuery(id+"F12.wireOp",EDGE,"E351.MirrorCS")])],"isStart":false});
            var Q2;
            Q2=makeQuery(id+"F13.opExtrude","CAP_VERTEX",VERTEX,{"disambiguationData":[OSD([sQuery(id+"F12.wireOp",EDGE,"E274"),sQuery(id+"F12.wireOp",EDGE,"E351.MirrorCS")])],"isStart":true});
            cPlane(context, id + "F56", {"entities" : qUnion([Q0, Q1, Q2]), "cplaneType" : CPlaneType.THREE_POINT, "offset" : 0 * mm, "width" : 150 * mm, "height" : 150 * mm});
        }
        {
            var Q0;
            Q0=qCreatedBy(id+"F56.planeOp",FACE);
            var sketch = newSketch(context, id + "F57", { "sketchPlane" : qUnion([Q0])});
            skLineSegment(sketch, "E524.bottom", {"start": v(600, 2588.84) * mm, "end": v(1300, 2588.84) * mm});
            skLineSegment(sketch, "E524.top", {"start": v(600, 1388.84) * mm, "end": v(1300, 1388.84) * mm});
            skLineSegment(sketch, "E524.left", {"start": v(600, 2588.84) * mm, "end": v(600, 1388.84) * mm});
            skLineSegment(sketch, "E524.right", {"start": v(1300, 2588.84) * mm, "end": v(1300, 1388.84) * mm});
            skLineSegment(sketch, "E525.bottom", {"start": v(700, 2488.84) * mm, "end": v(1200, 2488.84) * mm});
            skLineSegment(sketch, "E525.top", {"start": v(700, 1488.84) * mm, "end": v(1200, 1488.84) * mm});
            skLineSegment(sketch, "E525.left", {"start": v(700, 2488.84) * mm, "end": v(700, 1488.84) * mm});
            skLineSegment(sketch, "E525.right", {"start": v(1200, 2488.84) * mm, "end": v(1200, 1488.84) * mm});
            skSolve(sketch);
        }
        {
            var Q0;
            Q0 = qSketchRegion(id + "F57", true);
            extrude(context, id + "F58", {"entities" : qUnion([Q0]), "operationType" : NewBodyOperationType.ADD, "depth" : 25 * mm, "offsetDistance" : 25 * mm, "hasSecondDirection" : true, "secondDirectionOppositeDirection" : true, "secondDirectionDepth" : 25 * mm});
        }
        {
            var Q0;
            Q0=makeQuery(id+"F58.opExtrude","CAP_FACE",FACE,{"disambiguationData":[OSD([sQuery(id+"F57.wireOp",EDGE,"E524.bottom"),sQuery(id+"F57.wireOp",EDGE,"E524.top"),sQuery(id+"F57.wireOp",EDGE,"E524.left"),sQuery(id+"F57.wireOp",EDGE,"E524.right"),sQuery(id+"F57.wireOp",EDGE,"E525.bottom"),sQuery(id+"F57.wireOp",EDGE,"E525.top"),sQuery(id+"F57.wireOp",EDGE,"E525.left"),sQuery(id+"F57.wireOp",EDGE,"E525.right")])],"isStart":false});
            var sketch = newSketch(context, id + "F59", { "sketchPlane" : qUnion([Q0])});
            skLineSegment(sketch, "E526.0", {"start": v(700, 2488.84) * mm, "end": v(700, 1488.84) * mm});
            skLineSegment(sketch, "E527.0", {"start": v(700, 2488.84) * mm, "end": v(1200, 2488.84) * mm});
            skLineSegment(sketch, "E528.0", {"start": v(1200, 2488.84) * mm, "end": v(1200, 1488.84) * mm});
            skLineSegment(sketch, "E529.0", {"start": v(700, 1488.84) * mm, "end": v(1200, 1488.84) * mm});
            skSolve(sketch);
        }
        {
            var Q0;
            {var subQ1=sQuery(id+"F2.wireOp",EDGE,"E83.right");var subQ2=sQuery(id+"F0.wireOp",EDGE,"E75");var subQ3=sQuery(id+"F0.wireOp",EDGE,"E77.trimOffspring");var subQ4=sQuery(id+"F0.wireOp",EDGE,"E5");Q0=makeQuery(id+"F13.boolean.opBoolean","SPLIT",FACE,{"disambiguationData":[TD([makeQuery(id+"F1.opExtrude","SWEPT_FACE",FACE,{"disambiguationData":[OSD([subQ2])]})])],"derivedFrom":makeQuery(id+"F9.boolean.opBoolean","MERGE",FACE,{"derivedFrom":[makeQuery(id+"F3.boolean.opBoolean","MERGE",FACE,{"derivedFrom":[makeQuery(id+"F1.opExtrude","SWEPT_FACE",FACE,{"disambiguationData":[OSD([subQ4])]}),makeQuery(id+"F1.opExtrude","SWEPT_FACE",FACE,{"disambiguationData":[OSD([subQ3])]}),makeQuery(id+"F3.opExtrude","SWEPT_FACE",FACE,{"disambiguationData":[OSD([subQ1])]})]}),makeQuery(id+"F9.opExtrude","CAP_FACE",FACE,{"disambiguationData":[OSD([sQuery(id+"F8.wireOp",EDGE,"E167"),sQuery(id+"F8.wireOp",EDGE,"E170"),sQuery(id+"F8.wireOp",EDGE,"E171"),sQuery(id+"F8.wireOp",EDGE,"E172"),sQuery(id+"F8.wireOp",EDGE,"E173"),sQuery(id+"F8.wireOp",EDGE,"E174"),sQuery(id+"F8.wireOp",EDGE,"E175"),sQuery(id+"F8.wireOp",EDGE,"E176"),sQuery(id+"F8.wireOp",EDGE,"E177"),sQuery(id+"F8.wireOp",EDGE,"E178"),sQuery(id+"F8.wireOp",EDGE,"E179"),sQuery(id+"F8.wireOp",EDGE,"E180"),sQuery(id+"F8.wireOp",EDGE,"E181"),sQuery(id+"F8.wireOp",EDGE,"E182"),sQuery(id+"F8.wireOp",EDGE,"E183"),sQuery(id+"F8.wireOp",EDGE,"E184"),sQuery(id+"F8.wireOp",EDGE,"E185"),sQuery(id+"F8.wireOp",EDGE,"E186"),sQuery(id+"F8.wireOp",EDGE,"E187"),sQuery(id+"F8.wireOp",EDGE,"E188"),sQuery(id+"F8.wireOp",EDGE,"E189"),sQuery(id+"F8.wireOp",EDGE,"E190"),sQuery(id+"F8.wireOp",EDGE,"E191"),sQuery(id+"F8.wireOp",EDGE,"E192"),sQuery(id+"F8.wireOp",EDGE,"E193"),sQuery(id+"F8.wireOp",EDGE,"E194"),sQuery(id+"F8.wireOp",EDGE,"E195"),sQuery(id+"F8.wireOp",EDGE,"E196"),sQuery(id+"F8.wireOp",EDGE,"E197"),sQuery(id+"F8.wireOp",EDGE,"E198"),sQuery(id+"F8.wireOp",EDGE,"E199"),sQuery(id+"F8.wireOp",EDGE,"E200"),sQuery(id+"F8.wireOp",EDGE,"E201"),sQuery(id+"F8.wireOp",EDGE,"E202"),sQuery(id+"F8.wireOp",EDGE,"E203"),sQuery(id+"F8.wireOp",EDGE,"E204"),sQuery(id+"F8.wireOp",EDGE,"E205"),sQuery(id+"F8.wireOp",EDGE,"E206"),sQuery(id+"F8.wireOp",EDGE,"E207"),sQuery(id+"F8.wireOp",EDGE,"E208"),sQuery(id+"F8.wireOp",EDGE,"E209"),sQuery(id+"F8.wireOp",EDGE,"E210"),sQuery(id+"F8.wireOp",EDGE,"E211"),sQuery(id+"F8.wireOp",EDGE,"E212"),sQuery(id+"F8.wireOp",EDGE,"E213"),sQuery(id+"F8.wireOp",EDGE,"E214"),sQuery(id+"F8.wireOp",EDGE,"E215"),sQuery(id+"F8.wireOp",EDGE,"E216"),sQuery(id+"F8.wireOp",EDGE,"E217"),sQuery(id+"F8.wireOp",EDGE,"E218.MirrorCS"),sQuery(id+"F8.wireOp",EDGE,"E219.MirrorCS"),sQuery(id+"F8.wireOp",EDGE,"E220.MirrorCS"),sQuery(id+"F8.wireOp",EDGE,"E221.MirrorCS"),sQuery(id+"F8.wireOp",EDGE,"E222.MirrorCS"),sQuery(id+"F8.wireOp",EDGE,"E223.MirrorCS"),sQuery(id+"F8.wireOp",EDGE,"E224.MirrorCS"),sQuery(id+"F8.wireOp",EDGE,"E225.MirrorCS"),sQuery(id+"F8.wireOp",EDGE,"E226.MirrorCS"),sQuery(id+"F8.wireOp",EDGE,"E227.MirrorCS"),sQuery(id+"F8.wireOp",EDGE,"E228.MirrorCS"),sQuery(id+"F8.wireOp",EDGE,"E229.MirrorCS"),sQuery(id+"F8.wireOp",EDGE,"E230.MirrorCS"),sQuery(id+"F8.wireOp",EDGE,"E231.MirrorCS"),sQuery(id+"F8.wireOp",EDGE,"E232.MirrorCS"),sQuery(id+"F8.wireOp",EDGE,"E233.MirrorCS"),sQuery(id+"F8.wireOp",EDGE,"E234.MirrorCS"),sQuery(id+"F8.wireOp",EDGE,"E235.MirrorCS"),sQuery(id+"F8.wireOp",EDGE,"E236.MirrorCS"),sQuery(id+"F8.wireOp",EDGE,"E237.MirrorCS"),sQuery(id+"F8.wireOp",EDGE,"E238.MirrorCS"),sQuery(id+"F8.wireOp",EDGE,"E239.MirrorCS"),sQuery(id+"F8.wireOp",EDGE,"E240.MirrorCS"),sQuery(id+"F8.wireOp",EDGE,"E241.MirrorCS"),sQuery(id+"F8.wireOp",EDGE,"E242.MirrorCS"),sQuery(id+"F8.wireOp",EDGE,"E243.MirrorCS"),sQuery(id+"F8.wireOp",EDGE,"E244.MirrorCS"),sQuery(id+"F8.wireOp",EDGE,"E245.MirrorCS"),sQuery(id+"F8.wireOp",EDGE,"E246.MirrorCS"),sQuery(id+"F8.wireOp",EDGE,"E247.MirrorCS"),sQuery(id+"F8.wireOp",EDGE,"E248.MirrorCS"),sQuery(id+"F8.wireOp",EDGE,"E249.MirrorCS"),sQuery(id+"F8.wireOp",EDGE,"E250.MirrorCS"),sQuery(id+"F8.wireOp",EDGE,"E251.MirrorCS"),sQuery(id+"F8.wireOp",EDGE,"E252.MirrorCS"),sQuery(id+"F8.wireOp",EDGE,"E253.MirrorCS"),sQuery(id+"F8.wireOp",EDGE,"E254.MirrorCS"),sQuery(id+"F8.wireOp",EDGE,"E255.MirrorCS"),sQuery(id+"F8.wireOp",EDGE,"E256.MirrorCS"),sQuery(id+"F8.wireOp",EDGE,"E257.MirrorCS"),sQuery(id+"F8.wireOp",EDGE,"E258.MirrorCS"),sQuery(id+"F8.wireOp",EDGE,"E259.MirrorCS"),sQuery(id+"F8.wireOp",EDGE,"E260.MirrorCS"),sQuery(id+"F8.wireOp",EDGE,"E261.MirrorCS"),sQuery(id+"F8.wireOp",EDGE,"E262.MirrorCS"),sQuery(id+"F8.wireOp",EDGE,"E263.MirrorCS"),sQuery(id+"F8.wireOp",EDGE,"E264.MirrorCS"),sQuery(id+"F8.wireOp",EDGE,"E265.MirrorCS")])],"isStart":true})]})});}
            var sketch = newSketch(context, id + "F60", { "sketchPlane" : qUnion([Q0])});
            skLineSegment(sketch, "E530", {"start": v(250, 2750) * mm, "end": v(250, 3000) * mm});
            skLineSegment(sketch, "E531", {"start": v(250, 3000) * mm, "end": v(4400, 4510.48) * mm});
            skLineSegment(sketch, "E532", {"start": v(4400, 4510.48) * mm, "end": v(4400, 2750) * mm});
            skLineSegment(sketch, "E533", {"start": v(4400, 2750) * mm, "end": v(250, 2750) * mm});
            skSolve(sketch);
        }
        {
            var Q0;
            Q0 = qSketchRegion(id + "F60", true);
            extrude(context, id + "F61", {"entities" : qUnion([Q0]), "operationType" : NewBodyOperationType.REMOVE, "depth" : 1750 * mm, "offsetDistance" : 25 * mm});
        }
        {
            var Q0;
            Q0=makeQuery(id+"F33.opExtrude","SWEPT_FACE",FACE,{"disambiguationData":[OSD([sQuery(id+"F32.wireOp",EDGE,"E482.bottom")])]});
            var sketch = newSketch(context, id + "F62", { "sketchPlane" : qUnion([Q0])});
            skLineSegment(sketch, "E534.bottom", {"start": v(0, 3655.24) * mm, "end": v(1900, 3655.24) * mm});
            skLineSegment(sketch, "E534.top", {"start": v(0, 2300) * mm, "end": v(1900, 2300) * mm});
            skLineSegment(sketch, "E534.left", {"start": v(0, 3655.24) * mm, "end": v(0, 2300) * mm});
            skLineSegment(sketch, "E534.right", {"start": v(1900, 3655.24) * mm, "end": v(1900, 2300) * mm});
            skSolve(sketch);
        }
        {
            var Q0;
            Q0 = qSketchRegion(id + "F62", true);
            extrude(context, id + "F63", {"entities" : qUnion([Q0]), "operationType" : NewBodyOperationType.ADD, "oppositeDirection" : true, "depth" : 100 * mm, "offsetDistance" : 25 * mm});
        }
        {
            var Q0;
            Q0 = qSketchRegion(id + "F59", true);
            extrude(context, id + "F64", {"entities" : qUnion([Q0]), "operationType" : NewBodyOperationType.REMOVE, "oppositeDirection" : true, "depth" : 1000 * mm, "offsetDistance" : 25 * mm, "hasSecondDirection" : true, "secondDirectionOppositeDirection" : false, "secondDirectionDepth" : 1000 * mm});
        }
        {
            var Q0;
            Q0=makeQuery(id+"F15.boolean.opBoolean","SPLIT",FACE,{"disambiguationData":[TD([makeQuery(id+"F15.opExtrude","SWEPT_FACE",FACE,{"disambiguationData":[OSD([sQuery(id+"F14.wireOp",EDGE,"E382.bottom")])]})])],"derivedFrom":makeQuery(id+"F11.boolean.opBoolean","MERGE",FACE,{"derivedFrom":[makeQuery(id+"F3.boolean.opBoolean","MERGE",FACE,{"derivedFrom":[makeQuery(id+"F1.opExtrude","SWEPT_FACE",FACE,{"disambiguationData":[OSD([sQuery(id+"F0.wireOp",EDGE,"E4")])]}),makeQuery(id+"F3.opExtrude","SWEPT_FACE",FACE,{"disambiguationData":[OSD([sQuery(id+"F2.wireOp",EDGE,"E83.top")])]})]}),makeQuery(id+"F11.opExtrude","SWEPT_FACE",FACE,{"disambiguationData":[OSD([sQuery(id+"F10.wireOp",EDGE,"E266.bottom")])]})]})});
            var sketch = newSketch(context, id + "F65", { "sketchPlane" : qUnion([Q0])});
            skLineSegment(sketch, "E535.bottom", {"start": v(300, 2200) * mm, "end": v(1600, 2200) * mm});
            skLineSegment(sketch, "E535.top", {"start": v(300, 1400) * mm, "end": v(1600, 1400) * mm});
            skLineSegment(sketch, "E535.left", {"start": v(300, 2200) * mm, "end": v(300, 1400) * mm});
            skLineSegment(sketch, "E535.right", {"start": v(1600, 2200) * mm, "end": v(1600, 1400) * mm});
            skLineSegment(sketch, "E536.bottom", {"start": v(-199.5, 1400) * mm, "end": v(197.93, 1400) * mm});
            skLineSegment(sketch, "E536.top", {"start": v(-199.5, 1800.48) * mm, "end": v(197.93, 1800.48) * mm});
            skLineSegment(sketch, "E536.left", {"start": v(-199.5, 1400) * mm, "end": v(-199.5, 1800.48) * mm});
            skLineSegment(sketch, "E536.right", {"start": v(197.93, 1400) * mm, "end": v(197.93, 1800.48) * mm});
            skLineSegment(sketch, "E537.bottom", {"start": v(-199.5, 2200) * mm, "end": v(205.6, 2200) * mm});
            skLineSegment(sketch, "E537.top", {"start": v(-199.5, 1893.6) * mm, "end": v(205.6, 1893.6) * mm});
            skLineSegment(sketch, "E537.left", {"start": v(-199.5, 2200) * mm, "end": v(-199.5, 1893.6) * mm});
            skLineSegment(sketch, "E537.right", {"start": v(205.6, 2200) * mm, "end": v(205.6, 1893.6) * mm});
            skSolve(sketch);
        }
        {
            var Q0;
            Q0 = qSketchRegion(id + "F65", true);
            extrude(context, id + "F66", {"entities" : qUnion([Q0]), "operationType" : NewBodyOperationType.REMOVE, "oppositeDirection" : true, "depth" : 1000 * mm, "offsetDistance" : 25 * mm});
        }
        {
            var Q0;
            Q0=makeQuery(id+"F19.boolean.opBoolean","SPLIT",FACE,{"disambiguationData":[TD([makeQuery(id+"F19.opExtrude","SWEPT_FACE",FACE,{"disambiguationData":[OSD([sQuery(id+"F18.wireOp",EDGE,"E417.bottom")])]})])],"derivedFrom":makeQuery(id+"F11.boolean.opBoolean","MERGE",FACE,{"derivedFrom":[makeQuery(id+"F3.boolean.opBoolean","MERGE",FACE,{"derivedFrom":[makeQuery(id+"F1.opExtrude","SWEPT_FACE",FACE,{"disambiguationData":[OSD([sQuery(id+"F0.wireOp",EDGE,"E6")])]}),makeQuery(id+"F3.opExtrude","SWEPT_FACE",FACE,{"disambiguationData":[OSD([sQuery(id+"F2.wireOp",EDGE,"E83.bottom")])]})]}),makeQuery(id+"F11.opExtrude","SWEPT_FACE",FACE,{"disambiguationData":[OSD([sQuery(id+"F10.wireOp",EDGE,"E266.top")])]})]})});
            var sketch = newSketch(context, id + "F67", { "sketchPlane" : qUnion([Q0])});
            skLineSegment(sketch, "E538.bottom", {"start": v(900, 2400) * mm, "end": v(2040, 2400) * mm});
            skLineSegment(sketch, "E538.top", {"start": v(900, 1450) * mm, "end": v(2040, 1450) * mm});
            skLineSegment(sketch, "E538.left", {"start": v(900, 2400) * mm, "end": v(900, 1450) * mm});
            skLineSegment(sketch, "E538.right", {"start": v(2040, 2400) * mm, "end": v(2040, 1450) * mm});
            skLineSegment(sketch, "E539.bottom", {"start": v(2146.98, 2100.31) * mm, "end": v(2533.94, 2100.31) * mm});
            skLineSegment(sketch, "E539.top", {"start": v(2146.98, 1450) * mm, "end": v(2533.94, 1450) * mm});
            skLineSegment(sketch, "E539.left", {"start": v(2146.98, 2100.31) * mm, "end": v(2146.98, 1450) * mm});
            skLineSegment(sketch, "E539.right", {"start": v(2533.94, 2100.31) * mm, "end": v(2533.94, 1450) * mm});
            skLineSegment(sketch, "E540.bottom", {"start": v(2141.53, 2400) * mm, "end": v(2539.4, 2400) * mm});
            skLineSegment(sketch, "E540.top", {"start": v(2141.53, 2198.42) * mm, "end": v(2539.4, 2198.42) * mm});
            skLineSegment(sketch, "E540.left", {"start": v(2141.53, 2400) * mm, "end": v(2141.53, 2198.42) * mm});
            skLineSegment(sketch, "E540.right", {"start": v(2539.4, 2400) * mm, "end": v(2539.4, 2198.42) * mm});
            skLineSegment(sketch, "E541.bottom", {"start": v(402.93, 2400) * mm, "end": v(800.79, 2400) * mm});
            skLineSegment(sketch, "E541.top", {"start": v(402.93, 2203.87) * mm, "end": v(800.79, 2203.87) * mm});
            skLineSegment(sketch, "E541.left", {"start": v(402.93, 2400) * mm, "end": v(402.93, 2203.87) * mm});
            skLineSegment(sketch, "E541.right", {"start": v(800.79, 2400) * mm, "end": v(800.79, 2203.87) * mm});
            skLineSegment(sketch, "E542.bottom", {"start": v(402.93, 2105.76) * mm, "end": v(800.79, 2105.76) * mm});
            skLineSegment(sketch, "E542.top", {"start": v(402.93, 1450) * mm, "end": v(800.79, 1450) * mm});
            skLineSegment(sketch, "E542.left", {"start": v(402.93, 2105.76) * mm, "end": v(402.93, 1450) * mm});
            skLineSegment(sketch, "E542.right", {"start": v(800.79, 2105.76) * mm, "end": v(800.79, 1450) * mm});
            skSolve(sketch);
        }
        {
            var Q0;
            Q0 = qSketchRegion(id + "F67", true);
            extrude(context, id + "F68", {"entities" : qUnion([Q0]), "operationType" : NewBodyOperationType.REMOVE, "oppositeDirection" : true, "depth" : 1000 * mm, "offsetDistance" : 25 * mm});
        }
        {
            var Q0;
            Q0=makeQuery(id+"F21.boolean.opBoolean","MERGE",FACE,{"derivedFrom":[makeQuery(id+"F1.opExtrude","SWEPT_FACE",FACE,{"disambiguationData":[OSD([sQuery(id+"F0.wireOp",EDGE,"E26"),sQuery(id+"F0.wireOp",EDGE,"E34"),sQuery(id+"F0.wireOp",EDGE,"E82")])]}),makeQuery(id+"F21.opExtrude","SWEPT_FACE",FACE,{"disambiguationData":[OSD([sQuery(id+"F20.wireOp",EDGE,"E422.left")])]})]});
            var sketch = newSketch(context, id + "F69", { "sketchPlane" : qUnion([Q0])});
            skLineSegment(sketch, "E543", {"start": v(-3302.49, 300) * mm, "end": v(-1850, 300) * mm});
            skLineSegment(sketch, "E544", {"start": v(-1850, 300) * mm, "end": v(-1850, 500) * mm});
            skLineSegment(sketch, "E545", {"start": v(-1850, 500) * mm, "end": v(-2100, 500) * mm});
            skLineSegment(sketch, "E546", {"start": v(-2100, 500) * mm, "end": v(-2100, 700) * mm});
            skLineSegment(sketch, "E547", {"start": v(-2100, 700) * mm, "end": v(-2350, 700) * mm});
            skLineSegment(sketch, "E548", {"start": v(-3600, 1900) * mm, "end": v(-3850, 1900) * mm});
            skLineSegment(sketch, "E549", {"start": v(-3850, 1900) * mm, "end": v(-3850, 2100) * mm});
            skLineSegment(sketch, "E550", {"start": v(-3850, 2100) * mm, "end": v(-4100, 2100) * mm});
            skLineSegment(sketch, "E551", {"start": v(-4100, 2100) * mm, "end": v(-4100, 2300) * mm});
            skLineSegment(sketch, "E552", {"start": v(-4100, 2300) * mm, "end": v(-4350, 2300) * mm});
            skLineSegment(sketch, "E553", {"start": v(-4350, 2300) * mm, "end": v(-4350, 2500) * mm});
            skLineSegment(sketch, "E554", {"start": v(-4350, 2500) * mm, "end": v(-4600, 2500) * mm});
            skLineSegment(sketch, "E555", {"start": v(-4600, 2500) * mm, "end": v(-4600, 2700) * mm});
            skLineSegment(sketch, "E556", {"start": v(-4600, 2700) * mm, "end": v(-4850, 2700) * mm});
            skLineSegment(sketch, "E557", {"start": v(-4850, 2700) * mm, "end": v(-4850, 2598.7) * mm});
            skLineSegment(sketch, "E558", {"start": v(-3600, 1900) * mm, "end": v(-3600, 1700) * mm});
            skLineSegment(sketch, "E559", {"start": v(-3600, 1700) * mm, "end": v(-3350, 1700) * mm});
            skLineSegment(sketch, "E560", {"start": v(-3350, 1700) * mm, "end": v(-3350, 1500) * mm});
            skLineSegment(sketch, "E561", {"start": v(-3350, 1500) * mm, "end": v(-3100, 1500) * mm});
            skLineSegment(sketch, "E562", {"start": v(-3100, 1500) * mm, "end": v(-3100, 1300) * mm});
            skLineSegment(sketch, "E563", {"start": v(-3100, 1300) * mm, "end": v(-2850, 1300) * mm});
            skLineSegment(sketch, "E564", {"start": v(-2850, 1300) * mm, "end": v(-2850, 1100) * mm});
            skLineSegment(sketch, "E565", {"start": v(-2850, 1100) * mm, "end": v(-2600, 1100) * mm});
            skLineSegment(sketch, "E566", {"start": v(-2600, 1100) * mm, "end": v(-2600, 900) * mm});
            skLineSegment(sketch, "E567", {"start": v(-2600, 900) * mm, "end": v(-2350, 900) * mm});
            skLineSegment(sketch, "E568", {"start": v(-2350, 900) * mm, "end": v(-2350, 700) * mm});
            skLineSegment(sketch, "E569", {"start": v(-3302.49, 300) * mm, "end": v(-3302.49, 1373.62) * mm});
            skLineSegment(sketch, "E570", {"start": v(-3302.49, 1373.62) * mm, "end": v(-4850, 2598.7) * mm});
            skSolve(sketch);
        }
        {
            var Q0;
            Q0 = qSketchRegion(id + "F69", true);
            extrude(context, id + "F70", {"entities" : qUnion([Q0]), "depth" : 1000 * mm, "offsetDistance" : 25 * mm});
        }
    });
